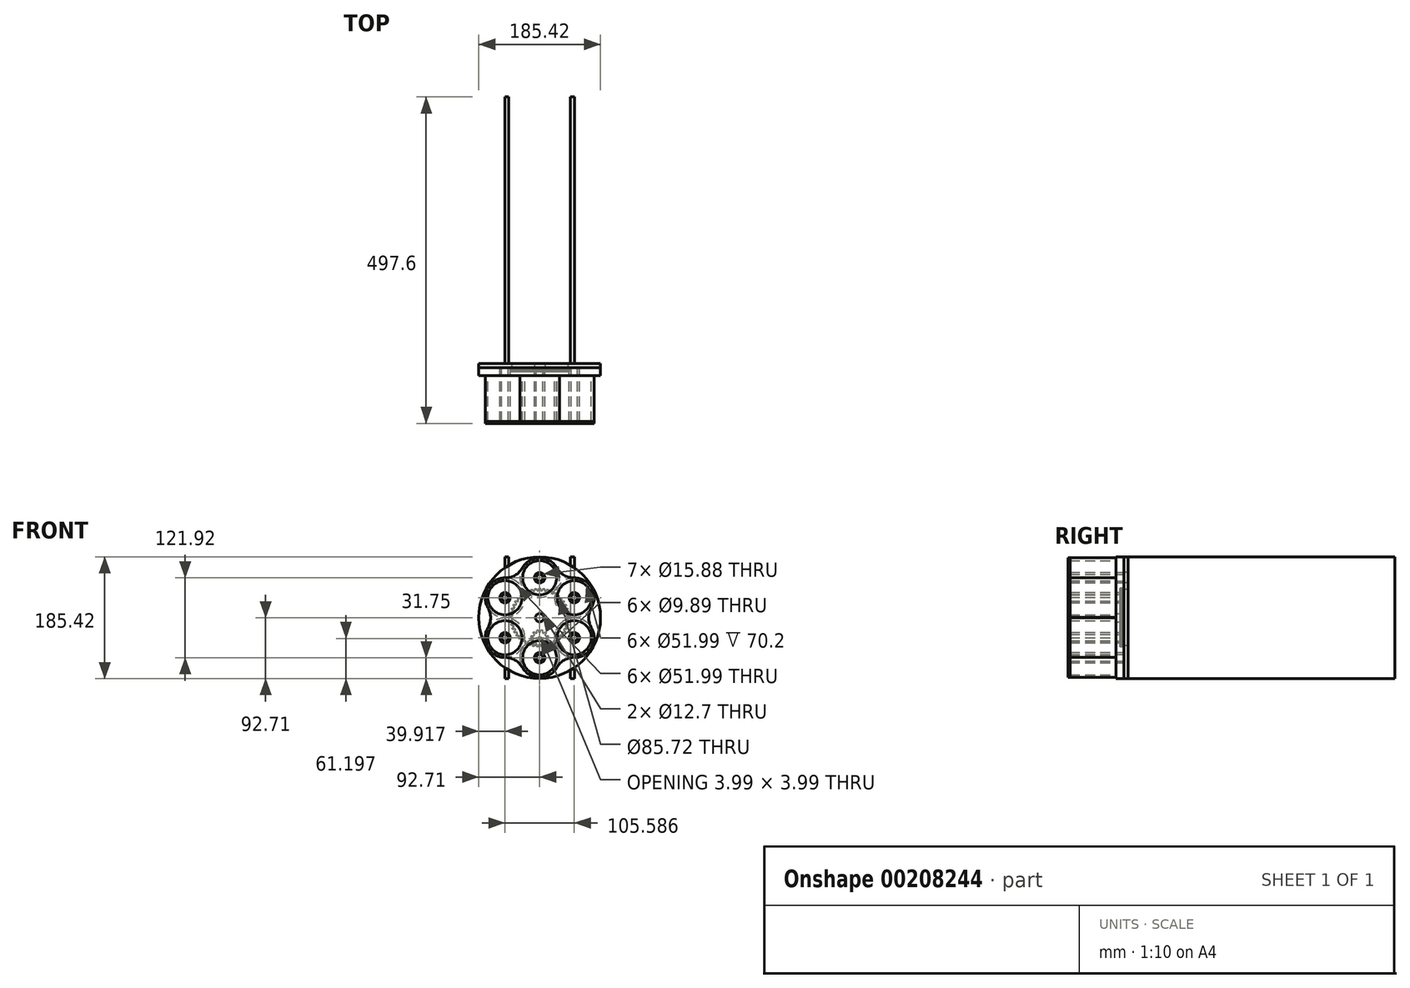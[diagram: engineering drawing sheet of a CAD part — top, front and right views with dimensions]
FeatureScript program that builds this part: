
annotation { "Feature Type Name" : "Feature", "Feature Type Description" : "" }
export const myFeature = defineFeature(function(context is Context, id is Id, definition is map)
    precondition{}
    {
        {
            var Q0;
            Q0=qCreatedBy(makeId("Front.planeOp"),FACE);
            var sketch = newSketch(context, id + "F0", { "sketchPlane" : qUnion([Q0])});
            skCircle(sketch, "E0", {"center": v(0, 0) * mm, "radius": 92.71 * mm});
            skCircle(sketch, "E1", {"center": v(0, 60.96) * mm, "radius": 26.67 * mm});
            skCircle(sketch, "E2", {"center": v(0, 60.96) * mm, "radius": 7.94 * mm});
            skCircle(sketch, "E3", {"center": v(0, 0) * mm, "radius": 60.96 * mm, "construction": true});
            skCircle(sketch, "E4.1.0", {"center": v(-52.8, 30.48) * mm, "radius": 26.67 * mm});
            skCircle(sketch, "E4.2.0", {"center": v(-52.8, -30.48) * mm, "radius": 26.67 * mm});
            skCircle(sketch, "E4.3.0", {"center": v(0, -60.96) * mm, "radius": 26.67 * mm});
            skCircle(sketch, "E4.4.0", {"center": v(52.8, -30.48) * mm, "radius": 26.67 * mm});
            skCircle(sketch, "E4.5.0", {"center": v(52.8, 30.48) * mm, "radius": 26.67 * mm});
            skCircle(sketch, "E5", {"center": v(0, 0) * mm, "radius": 6.35 * mm});
            skCircle(sketch, "E6.1.0", {"center": v(-52.8, 30.48) * mm, "radius": 7.94 * mm});
            skCircle(sketch, "E6.2.0", {"center": v(-52.8, -30.48) * mm, "radius": 7.94 * mm});
            skCircle(sketch, "E6.3.0", {"center": v(0, -60.96) * mm, "radius": 7.94 * mm});
            skCircle(sketch, "E6.4.0", {"center": v(52.8, -30.48) * mm, "radius": 7.94 * mm});
            skCircle(sketch, "E6.5.0", {"center": v(52.8, 30.48) * mm, "radius": 7.94 * mm});
            skSolve(sketch);
        }
        {
            var Q0;
            Q0=qCreatedBy(makeId("Front.planeOp"),FACE);
            var sketch = newSketch(context, id + "F1", { "sketchPlane" : qUnion([Q0])});
            skCircle(sketch, "E7.0", {"center": v(0, 0) * mm, "radius": 92.71 * mm});
            skCircle(sketch, "E8.0", {"center": v(0, 60.96) * mm, "radius": 7.94 * mm});
            skCircle(sketch, "E9.0", {"center": v(0, 0) * mm, "radius": 6.35 * mm});
            skCircle(sketch, "E10.0", {"center": v(52.8, 30.48) * mm, "radius": 7.94 * mm});
            skCircle(sketch, "E10.1", {"center": v(52.8, -30.48) * mm, "radius": 7.94 * mm});
            skCircle(sketch, "E10.2", {"center": v(0, -60.96) * mm, "radius": 7.94 * mm});
            skCircle(sketch, "E10.3", {"center": v(-52.8, -30.48) * mm, "radius": 7.94 * mm});
            skCircle(sketch, "E10.4", {"center": v(-52.8, 30.48) * mm, "radius": 7.94 * mm});
            skSolve(sketch);
        }
        {
            var Q0;
            Q0 = qSketchRegion(id + "F1", true);
            extrude(context, id + "F2", {"entities" : qUnion([Q0]), "depth" : 6 * mm});
        }
        {
            var Q0;
            Q0=qCreatedBy(makeId("Front.planeOp"),FACE);
            var sketch = newSketch(context, id + "F3", { "sketchPlane" : qUnion([Q0])});
            skLineSegment(sketch, "E11", {"start": v(0, 52.57) * mm, "end": v(-10.93, 51.42) * mm});
            skLineSegment(sketch, "E12", {"start": v(-10.93, 51.42) * mm, "end": v(-21.38, 48.03) * mm});
            skLineSegment(sketch, "E13", {"start": v(-21.38, 48.03) * mm, "end": v(-30.9, 42.53) * mm});
            skLineSegment(sketch, "E14", {"start": v(-30.9, 42.53) * mm, "end": v(-39.07, 35.18) * mm});
            skLineSegment(sketch, "E15", {"start": v(-39.07, 35.18) * mm, "end": v(-45.53, 26.29) * mm});
            skLineSegment(sketch, "E16", {"start": v(-45.53, 26.29) * mm, "end": v(-50, 16.25) * mm});
            skLineSegment(sketch, "E17", {"start": v(-50, 16.25) * mm, "end": v(-52.28, 5.5) * mm});
            skLineSegment(sketch, "E18", {"start": v(-52.28, 5.5) * mm, "end": v(-52.28, -5.5) * mm});
            skLineSegment(sketch, "E19", {"start": v(-52.28, -5.5) * mm, "end": v(-50, -16.25) * mm});
            skLineSegment(sketch, "E20", {"start": v(-50, -16.25) * mm, "end": v(-45.53, -26.29) * mm});
            skLineSegment(sketch, "E21", {"start": v(-45.53, -26.29) * mm, "end": v(-39.07, -35.18) * mm});
            skLineSegment(sketch, "E22", {"start": v(-39.07, -35.18) * mm, "end": v(-30.9, -42.53) * mm});
            skLineSegment(sketch, "E23", {"start": v(-30.9, -42.53) * mm, "end": v(-21.38, -48.03) * mm});
            skLineSegment(sketch, "E24", {"start": v(-21.38, -48.03) * mm, "end": v(-10.93, -51.42) * mm});
            skLineSegment(sketch, "E25", {"start": v(-10.93, -51.42) * mm, "end": v(0, -52.57) * mm});
            skLineSegment(sketch, "E26", {"start": v(0, -52.57) * mm, "end": v(10.93, -51.42) * mm});
            skLineSegment(sketch, "E27", {"start": v(10.93, -51.42) * mm, "end": v(21.38, -48.03) * mm});
            skLineSegment(sketch, "E28", {"start": v(21.38, -48.03) * mm, "end": v(30.9, -42.53) * mm});
            skLineSegment(sketch, "E29", {"start": v(30.9, -42.53) * mm, "end": v(39.07, -35.18) * mm});
            skLineSegment(sketch, "E30", {"start": v(39.07, -35.18) * mm, "end": v(45.53, -26.29) * mm});
            skLineSegment(sketch, "E31", {"start": v(45.53, -26.29) * mm, "end": v(50, -16.25) * mm});
            skLineSegment(sketch, "E32", {"start": v(50, -16.25) * mm, "end": v(52.28, -5.5) * mm});
            skLineSegment(sketch, "E33", {"start": v(52.28, -5.5) * mm, "end": v(52.28, 5.5) * mm});
            skLineSegment(sketch, "E34", {"start": v(52.28, 5.5) * mm, "end": v(50, 16.25) * mm});
            skLineSegment(sketch, "E35", {"start": v(50, 16.25) * mm, "end": v(45.53, 26.29) * mm});
            skLineSegment(sketch, "E36", {"start": v(45.53, 26.29) * mm, "end": v(39.07, 35.18) * mm});
            skLineSegment(sketch, "E37", {"start": v(39.07, 35.18) * mm, "end": v(30.9, 42.53) * mm});
            skLineSegment(sketch, "E38", {"start": v(30.9, 42.53) * mm, "end": v(21.38, 48.03) * mm});
            skLineSegment(sketch, "E39", {"start": v(21.38, 48.03) * mm, "end": v(10.93, 51.42) * mm});
            skLineSegment(sketch, "E40", {"start": v(10.93, 51.42) * mm, "end": v(0, 52.57) * mm});
            skLineSegment(sketch, "E41", {"start": v(-3, -44.75) * mm, "end": v(-3.13, -44.73) * mm});
            skLineSegment(sketch, "E42", {"start": v(-3.13, -44.73) * mm, "end": v(-3.25, -44.73) * mm});
            skLineSegment(sketch, "E43", {"start": v(-3.25, -44.73) * mm, "end": v(-3.7, -44.68) * mm});
            skLineSegment(sketch, "E44", {"start": v(-3.7, -44.68) * mm, "end": v(-3.92, -44.58) * mm});
            skLineSegment(sketch, "E45", {"start": v(-3.92, -44.58) * mm, "end": v(-4.13, -44.16) * mm});
            skLineSegment(sketch, "E46", {"start": v(-4.13, -44.16) * mm, "end": v(-4.38, -43.31) * mm});
            skLineSegment(sketch, "E47", {"start": v(-4.38, -43.31) * mm, "end": v(-4.43, -43.13) * mm});
            skLineSegment(sketch, "E48", {"start": v(-4.43, -43.13) * mm, "end": v(-4.55, -42.6) * mm});
            skLineSegment(sketch, "E49", {"start": v(-4.55, -42.6) * mm, "end": v(-4.56, -42.54) * mm});
            skLineSegment(sketch, "E50", {"start": v(-4.56, -42.54) * mm, "end": v(-4.64, -42.15) * mm});
            skLineSegment(sketch, "E51", {"start": v(-4.64, -42.15) * mm, "end": v(-4.64, -42.07) * mm});
            skLineSegment(sketch, "E52", {"start": v(-4.64, -42.07) * mm, "end": v(-4.69, -41.85) * mm});
            skLineSegment(sketch, "E53", {"start": v(-4.69, -41.85) * mm, "end": v(-4.7, -41.78) * mm});
            skLineSegment(sketch, "E54", {"start": v(-4.7, -41.78) * mm, "end": v(-4.7, -41.66) * mm});
            skLineSegment(sketch, "E55", {"start": v(-4.7, -41.66) * mm, "end": v(-4.8, -41.02) * mm});
            skLineSegment(sketch, "E56", {"start": v(-4.8, -41.02) * mm, "end": v(-4.84, -40.92) * mm});
            skLineSegment(sketch, "E57", {"start": v(-4.84, -40.92) * mm, "end": v(-4.86, -40.88) * mm});
            skLineSegment(sketch, "E58", {"start": v(-4.86, -40.88) * mm, "end": v(-4.9, -40.83) * mm});
            skLineSegment(sketch, "E59", {"start": v(-4.9, -40.83) * mm, "end": v(-6.54, -40.6) * mm});
            skLineSegment(sketch, "E60", {"start": v(-6.54, -40.6) * mm, "end": v(-6.6, -40.63) * mm});
            skLineSegment(sketch, "E61", {"start": v(-6.6, -40.63) * mm, "end": v(-6.63, -40.67) * mm});
            skLineSegment(sketch, "E62", {"start": v(-6.63, -40.67) * mm, "end": v(-6.69, -40.75) * mm});
            skLineSegment(sketch, "E63", {"start": v(-6.69, -40.75) * mm, "end": v(-6.97, -41.34) * mm});
            skLineSegment(sketch, "E64", {"start": v(-6.97, -41.34) * mm, "end": v(-7, -41.45) * mm});
            skLineSegment(sketch, "E65", {"start": v(-7, -41.45) * mm, "end": v(-7.03, -41.52) * mm});
            skLineSegment(sketch, "E66", {"start": v(-7.03, -41.52) * mm, "end": v(-7.14, -41.72) * mm});
            skLineSegment(sketch, "E67", {"start": v(-7.14, -41.72) * mm, "end": v(-7.16, -41.8) * mm});
            skLineSegment(sketch, "E68", {"start": v(-7.16, -41.8) * mm, "end": v(-7.34, -42.15) * mm});
            skLineSegment(sketch, "E69", {"start": v(-7.34, -42.15) * mm, "end": v(-7.37, -42.2) * mm});
            skLineSegment(sketch, "E70", {"start": v(-7.37, -42.2) * mm, "end": v(-7.63, -42.68) * mm});
            skLineSegment(sketch, "E71", {"start": v(-7.63, -42.68) * mm, "end": v(-7.73, -42.84) * mm});
            skLineSegment(sketch, "E72", {"start": v(-7.73, -42.84) * mm, "end": v(-8.2, -43.59) * mm});
            skLineSegment(sketch, "E73", {"start": v(-8.2, -43.59) * mm, "end": v(-8.51, -43.93) * mm});
            skLineSegment(sketch, "E74", {"start": v(-8.51, -43.93) * mm, "end": v(-8.76, -43.97) * mm});
            skLineSegment(sketch, "E75", {"start": v(-8.76, -43.97) * mm, "end": v(-9.2, -43.9) * mm});
            skLineSegment(sketch, "E76", {"start": v(-9.2, -43.9) * mm, "end": v(-9.32, -43.86) * mm});
            skLineSegment(sketch, "E77", {"start": v(-9.32, -43.86) * mm, "end": v(-9.44, -43.84) * mm});
            skLineSegment(sketch, "E78", {"start": v(-9.44, -43.84) * mm, "end": v(-9.88, -43.73) * mm});
            skLineSegment(sketch, "E79", {"start": v(-9.88, -43.73) * mm, "end": v(-10.1, -43.6) * mm});
            skLineSegment(sketch, "E80", {"start": v(-10.1, -43.6) * mm, "end": v(-10.24, -43.15) * mm});
            skLineSegment(sketch, "E81", {"start": v(-10.24, -43.15) * mm, "end": v(-10.36, -42.28) * mm});
            skLineSegment(sketch, "E82", {"start": v(-10.36, -42.28) * mm, "end": v(-10.39, -42.1) * mm});
            skLineSegment(sketch, "E83", {"start": v(-10.39, -42.1) * mm, "end": v(-10.44, -41.55) * mm});
            skLineSegment(sketch, "E84", {"start": v(-10.44, -41.55) * mm, "end": v(-10.44, -41.5) * mm});
            skLineSegment(sketch, "E85", {"start": v(-10.44, -41.5) * mm, "end": v(-10.46, -41.1) * mm});
            skLineSegment(sketch, "E86", {"start": v(-10.46, -41.1) * mm, "end": v(-10.45, -41.02) * mm});
            skLineSegment(sketch, "E87", {"start": v(-10.45, -41.02) * mm, "end": v(-10.47, -40.8) * mm});
            skLineSegment(sketch, "E88", {"start": v(-10.47, -40.8) * mm, "end": v(-10.47, -40.72) * mm});
            skLineSegment(sketch, "E89", {"start": v(-10.47, -40.72) * mm, "end": v(-10.45, -40.6) * mm});
            skLineSegment(sketch, "E90", {"start": v(-10.45, -40.6) * mm, "end": v(-10.47, -39.95) * mm});
            skLineSegment(sketch, "E91", {"start": v(-10.47, -39.95) * mm, "end": v(-10.48, -39.85) * mm});
            skLineSegment(sketch, "E92", {"start": v(-10.48, -39.85) * mm, "end": v(-10.5, -39.8) * mm});
            skLineSegment(sketch, "E93", {"start": v(-10.5, -39.8) * mm, "end": v(-10.54, -39.75) * mm});
            skLineSegment(sketch, "E94", {"start": v(-10.54, -39.75) * mm, "end": v(-12.13, -39.3) * mm});
            skLineSegment(sketch, "E95", {"start": v(-12.13, -39.3) * mm, "end": v(-12.18, -39.32) * mm});
            skLineSegment(sketch, "E96", {"start": v(-12.18, -39.32) * mm, "end": v(-12.23, -39.35) * mm});
            skLineSegment(sketch, "E97", {"start": v(-12.23, -39.35) * mm, "end": v(-12.3, -39.43) * mm});
            skLineSegment(sketch, "E98", {"start": v(-12.3, -39.43) * mm, "end": v(-12.65, -39.97) * mm});
            skLineSegment(sketch, "E99", {"start": v(-12.65, -39.97) * mm, "end": v(-12.7, -40.08) * mm});
            skLineSegment(sketch, "E100", {"start": v(-12.7, -40.08) * mm, "end": v(-12.74, -40.14) * mm});
            skLineSegment(sketch, "E101", {"start": v(-12.74, -40.14) * mm, "end": v(-12.87, -40.32) * mm});
            skLineSegment(sketch, "E102", {"start": v(-12.87, -40.32) * mm, "end": v(-12.9, -40.39) * mm});
            skLineSegment(sketch, "E103", {"start": v(-12.9, -40.39) * mm, "end": v(-13.14, -40.72) * mm});
            skLineSegment(sketch, "E104", {"start": v(-13.14, -40.72) * mm, "end": v(-13.17, -40.77) * mm});
            skLineSegment(sketch, "E105", {"start": v(-13.17, -40.77) * mm, "end": v(-13.5, -41.2) * mm});
            skLineSegment(sketch, "E106", {"start": v(-13.5, -41.2) * mm, "end": v(-13.62, -41.35) * mm});
            skLineSegment(sketch, "E107", {"start": v(-13.62, -41.35) * mm, "end": v(-14.19, -42.02) * mm});
            skLineSegment(sketch, "E108", {"start": v(-14.19, -42.02) * mm, "end": v(-14.55, -42.32) * mm});
            skLineSegment(sketch, "E109", {"start": v(-14.55, -42.32) * mm, "end": v(-14.8, -42.32) * mm});
            skLineSegment(sketch, "E110", {"start": v(-14.8, -42.32) * mm, "end": v(-15.22, -42.18) * mm});
            skLineSegment(sketch, "E111", {"start": v(-15.22, -42.18) * mm, "end": v(-15.34, -42.14) * mm});
            skLineSegment(sketch, "E112", {"start": v(-15.34, -42.14) * mm, "end": v(-15.45, -42.1) * mm});
            skLineSegment(sketch, "E113", {"start": v(-15.45, -42.1) * mm, "end": v(-15.87, -41.93) * mm});
            skLineSegment(sketch, "E114", {"start": v(-15.87, -41.93) * mm, "end": v(-16.06, -41.77) * mm});
            skLineSegment(sketch, "E115", {"start": v(-16.06, -41.77) * mm, "end": v(-16.14, -41.3) * mm});
            skLineSegment(sketch, "E116", {"start": v(-16.14, -41.3) * mm, "end": v(-16.15, -40.43) * mm});
            skLineSegment(sketch, "E117", {"start": v(-16.15, -40.43) * mm, "end": v(-16.15, -40.24) * mm});
            skLineSegment(sketch, "E118", {"start": v(-16.15, -40.24) * mm, "end": v(-16.12, -39.7) * mm});
            skLineSegment(sketch, "E119", {"start": v(-16.12, -39.7) * mm, "end": v(-16.11, -39.64) * mm});
            skLineSegment(sketch, "E120", {"start": v(-16.11, -39.64) * mm, "end": v(-16.08, -39.23) * mm});
            skLineSegment(sketch, "E121", {"start": v(-16.08, -39.23) * mm, "end": v(-16.06, -39.16) * mm});
            skLineSegment(sketch, "E122", {"start": v(-16.06, -39.16) * mm, "end": v(-16.04, -38.94) * mm});
            skLineSegment(sketch, "E123", {"start": v(-16.04, -38.94) * mm, "end": v(-16.03, -38.86) * mm});
            skLineSegment(sketch, "E124", {"start": v(-16.03, -38.86) * mm, "end": v(-16, -38.75) * mm});
            skLineSegment(sketch, "E125", {"start": v(-16, -38.75) * mm, "end": v(-15.93, -38.1) * mm});
            skLineSegment(sketch, "E126", {"start": v(-15.93, -38.1) * mm, "end": v(-15.93, -38) * mm});
            skLineSegment(sketch, "E127", {"start": v(-15.93, -38) * mm, "end": v(-15.94, -37.95) * mm});
            skLineSegment(sketch, "E128", {"start": v(-15.94, -37.95) * mm, "end": v(-15.97, -37.9) * mm});
            skLineSegment(sketch, "E129", {"start": v(-15.97, -37.9) * mm, "end": v(-17.48, -37.22) * mm});
            skLineSegment(sketch, "E130", {"start": v(-17.48, -37.22) * mm, "end": v(-17.54, -37.24) * mm});
            skLineSegment(sketch, "E131", {"start": v(-17.54, -37.24) * mm, "end": v(-17.58, -37.26) * mm});
            skLineSegment(sketch, "E132", {"start": v(-17.58, -37.26) * mm, "end": v(-17.66, -37.33) * mm});
            skLineSegment(sketch, "E133", {"start": v(-17.66, -37.33) * mm, "end": v(-18.1, -37.81) * mm});
            skLineSegment(sketch, "E134", {"start": v(-18.1, -37.81) * mm, "end": v(-18.15, -37.92) * mm});
            skLineSegment(sketch, "E135", {"start": v(-18.15, -37.92) * mm, "end": v(-18.2, -37.98) * mm});
            skLineSegment(sketch, "E136", {"start": v(-18.2, -37.98) * mm, "end": v(-18.36, -38.14) * mm});
            skLineSegment(sketch, "E137", {"start": v(-18.36, -38.14) * mm, "end": v(-18.4, -38.2) * mm});
            skLineSegment(sketch, "E138", {"start": v(-18.4, -38.2) * mm, "end": v(-18.68, -38.5) * mm});
            skLineSegment(sketch, "E139", {"start": v(-18.68, -38.5) * mm, "end": v(-18.71, -38.54) * mm});
            skLineSegment(sketch, "E140", {"start": v(-18.71, -38.54) * mm, "end": v(-19.1, -38.93) * mm});
            skLineSegment(sketch, "E141", {"start": v(-19.1, -38.93) * mm, "end": v(-19.24, -39.05) * mm});
            skLineSegment(sketch, "E142", {"start": v(-19.24, -39.05) * mm, "end": v(-19.9, -39.64) * mm});
            skLineSegment(sketch, "E143", {"start": v(-19.9, -39.64) * mm, "end": v(-20.3, -39.88) * mm});
            skLineSegment(sketch, "E144", {"start": v(-20.3, -39.88) * mm, "end": v(-20.54, -39.85) * mm});
            skLineSegment(sketch, "E145", {"start": v(-20.54, -39.85) * mm, "end": v(-20.95, -39.65) * mm});
            skLineSegment(sketch, "E146", {"start": v(-20.95, -39.65) * mm, "end": v(-21.05, -39.6) * mm});
            skLineSegment(sketch, "E147", {"start": v(-21.05, -39.6) * mm, "end": v(-21.16, -39.54) * mm});
            skLineSegment(sketch, "E148", {"start": v(-21.16, -39.54) * mm, "end": v(-21.55, -39.31) * mm});
            skLineSegment(sketch, "E149", {"start": v(-21.55, -39.31) * mm, "end": v(-21.72, -39.13) * mm});
            skLineSegment(sketch, "E150", {"start": v(-21.72, -39.13) * mm, "end": v(-21.73, -38.66) * mm});
            skLineSegment(sketch, "E151", {"start": v(-21.73, -38.66) * mm, "end": v(-21.62, -37.79) * mm});
            skLineSegment(sketch, "E152", {"start": v(-21.62, -37.79) * mm, "end": v(-21.59, -37.6) * mm});
            skLineSegment(sketch, "E153", {"start": v(-21.59, -37.6) * mm, "end": v(-21.48, -37.06) * mm});
            skLineSegment(sketch, "E154", {"start": v(-21.48, -37.06) * mm, "end": v(-21.47, -37) * mm});
            skLineSegment(sketch, "E155", {"start": v(-21.47, -37) * mm, "end": v(-21.38, -36.62) * mm});
            skLineSegment(sketch, "E156", {"start": v(-21.38, -36.62) * mm, "end": v(-21.35, -36.55) * mm});
            skLineSegment(sketch, "E157", {"start": v(-21.35, -36.55) * mm, "end": v(-21.3, -36.33) * mm});
            skLineSegment(sketch, "E158", {"start": v(-21.3, -36.33) * mm, "end": v(-21.28, -36.25) * mm});
            skLineSegment(sketch, "E159", {"start": v(-21.28, -36.25) * mm, "end": v(-21.23, -36.15) * mm});
            skLineSegment(sketch, "E160", {"start": v(-21.23, -36.15) * mm, "end": v(-21.07, -35.52) * mm});
            skLineSegment(sketch, "E161", {"start": v(-21.07, -35.52) * mm, "end": v(-21.06, -35.41) * mm});
            skLineSegment(sketch, "E162", {"start": v(-21.06, -35.41) * mm, "end": v(-21.07, -35.36) * mm});
            skLineSegment(sketch, "E163", {"start": v(-21.07, -35.36) * mm, "end": v(-21.08, -35.3) * mm});
            skLineSegment(sketch, "E164", {"start": v(-21.08, -35.3) * mm, "end": v(-22.49, -34.43) * mm});
            skLineSegment(sketch, "E165", {"start": v(-22.49, -34.43) * mm, "end": v(-22.55, -34.44) * mm});
            skLineSegment(sketch, "E166", {"start": v(-22.55, -34.44) * mm, "end": v(-22.6, -34.45) * mm});
            skLineSegment(sketch, "E167", {"start": v(-22.6, -34.45) * mm, "end": v(-22.68, -34.51) * mm});
            skLineSegment(sketch, "E168", {"start": v(-22.68, -34.51) * mm, "end": v(-23.18, -34.93) * mm});
            skLineSegment(sketch, "E169", {"start": v(-23.18, -34.93) * mm, "end": v(-23.26, -35.02) * mm});
            skLineSegment(sketch, "E170", {"start": v(-23.26, -35.02) * mm, "end": v(-23.31, -35.07) * mm});
            skLineSegment(sketch, "E171", {"start": v(-23.31, -35.07) * mm, "end": v(-23.49, -35.21) * mm});
            skLineSegment(sketch, "E172", {"start": v(-23.49, -35.21) * mm, "end": v(-23.54, -35.27) * mm});
            skLineSegment(sketch, "E173", {"start": v(-23.54, -35.27) * mm, "end": v(-23.85, -35.52) * mm});
            skLineSegment(sketch, "E174", {"start": v(-23.85, -35.52) * mm, "end": v(-23.9, -35.56) * mm});
            skLineSegment(sketch, "E175", {"start": v(-23.9, -35.56) * mm, "end": v(-24.33, -35.89) * mm});
            skLineSegment(sketch, "E176", {"start": v(-24.33, -35.89) * mm, "end": v(-24.49, -36) * mm});
            skLineSegment(sketch, "E177", {"start": v(-24.49, -36) * mm, "end": v(-25.22, -36.48) * mm});
            skLineSegment(sketch, "E178", {"start": v(-25.22, -36.48) * mm, "end": v(-25.65, -36.67) * mm});
            skLineSegment(sketch, "E179", {"start": v(-25.65, -36.67) * mm, "end": v(-25.89, -36.6) * mm});
            skLineSegment(sketch, "E180", {"start": v(-25.89, -36.6) * mm, "end": v(-26.26, -36.35) * mm});
            skLineSegment(sketch, "E181", {"start": v(-26.26, -36.35) * mm, "end": v(-26.36, -36.28) * mm});
            skLineSegment(sketch, "E182", {"start": v(-26.36, -36.28) * mm, "end": v(-26.46, -36.2) * mm});
            skLineSegment(sketch, "E183", {"start": v(-26.46, -36.2) * mm, "end": v(-26.81, -35.93) * mm});
            skLineSegment(sketch, "E184", {"start": v(-26.81, -35.93) * mm, "end": v(-26.95, -35.72) * mm});
            skLineSegment(sketch, "E185", {"start": v(-26.95, -35.72) * mm, "end": v(-26.9, -35.26) * mm});
            skLineSegment(sketch, "E186", {"start": v(-26.9, -35.26) * mm, "end": v(-26.67, -34.41) * mm});
            skLineSegment(sketch, "E187", {"start": v(-26.67, -34.41) * mm, "end": v(-26.61, -34.23) * mm});
            skLineSegment(sketch, "E188", {"start": v(-26.61, -34.23) * mm, "end": v(-26.43, -33.71) * mm});
            skLineSegment(sketch, "E189", {"start": v(-26.43, -33.71) * mm, "end": v(-26.41, -33.66) * mm});
            skLineSegment(sketch, "E190", {"start": v(-26.41, -33.66) * mm, "end": v(-26.27, -33.28) * mm});
            skLineSegment(sketch, "E191", {"start": v(-26.27, -33.28) * mm, "end": v(-26.23, -33.22) * mm});
            skLineSegment(sketch, "E192", {"start": v(-26.23, -33.22) * mm, "end": v(-26.15, -33) * mm});
            skLineSegment(sketch, "E193", {"start": v(-26.15, -33) * mm, "end": v(-26.12, -32.94) * mm});
            skLineSegment(sketch, "E194", {"start": v(-26.12, -32.94) * mm, "end": v(-26.06, -32.84) * mm});
            skLineSegment(sketch, "E195", {"start": v(-26.06, -32.84) * mm, "end": v(-25.81, -32.24) * mm});
            skLineSegment(sketch, "E196", {"start": v(-25.81, -32.24) * mm, "end": v(-25.79, -32.14) * mm});
            skLineSegment(sketch, "E197", {"start": v(-25.79, -32.14) * mm, "end": v(-25.78, -32.09) * mm});
            skLineSegment(sketch, "E198", {"start": v(-25.78, -32.09) * mm, "end": v(-25.8, -32.03) * mm});
            skLineSegment(sketch, "E199", {"start": v(-25.8, -32.03) * mm, "end": v(-27.06, -30.96) * mm});
            skLineSegment(sketch, "E200", {"start": v(-27.06, -30.96) * mm, "end": v(-27.12, -30.97) * mm});
            skLineSegment(sketch, "E201", {"start": v(-27.12, -30.97) * mm, "end": v(-27.17, -30.97) * mm});
            skLineSegment(sketch, "E202", {"start": v(-27.17, -30.97) * mm, "end": v(-27.27, -31.02) * mm});
            skLineSegment(sketch, "E203", {"start": v(-27.27, -31.02) * mm, "end": v(-27.82, -31.36) * mm});
            skLineSegment(sketch, "E204", {"start": v(-27.82, -31.36) * mm, "end": v(-27.9, -31.45) * mm});
            skLineSegment(sketch, "E205", {"start": v(-27.9, -31.45) * mm, "end": v(-27.96, -31.49) * mm});
            skLineSegment(sketch, "E206", {"start": v(-27.96, -31.49) * mm, "end": v(-28.16, -31.6) * mm});
            skLineSegment(sketch, "E207", {"start": v(-28.16, -31.6) * mm, "end": v(-28.22, -31.65) * mm});
            skLineSegment(sketch, "E208", {"start": v(-28.22, -31.65) * mm, "end": v(-28.56, -31.86) * mm});
            skLineSegment(sketch, "E209", {"start": v(-28.56, -31.86) * mm, "end": v(-28.61, -31.89) * mm});
            skLineSegment(sketch, "E210", {"start": v(-28.61, -31.89) * mm, "end": v(-29.1, -32.15) * mm});
            skLineSegment(sketch, "E211", {"start": v(-29.1, -32.15) * mm, "end": v(-29.26, -32.24) * mm});
            skLineSegment(sketch, "E212", {"start": v(-29.26, -32.24) * mm, "end": v(-30.05, -32.62) * mm});
            skLineSegment(sketch, "E213", {"start": v(-30.05, -32.62) * mm, "end": v(-30.5, -32.74) * mm});
            skLineSegment(sketch, "E214", {"start": v(-30.5, -32.74) * mm, "end": v(-30.73, -32.64) * mm});
            skLineSegment(sketch, "E215", {"start": v(-30.73, -32.64) * mm, "end": v(-31.06, -32.34) * mm});
            skLineSegment(sketch, "E216", {"start": v(-31.06, -32.34) * mm, "end": v(-31.15, -32.26) * mm});
            skLineSegment(sketch, "E217", {"start": v(-31.15, -32.26) * mm, "end": v(-31.24, -32.17) * mm});
            skLineSegment(sketch, "E218", {"start": v(-31.24, -32.17) * mm, "end": v(-31.55, -31.85) * mm});
            skLineSegment(sketch, "E219", {"start": v(-31.55, -31.85) * mm, "end": v(-31.66, -31.62) * mm});
            skLineSegment(sketch, "E220", {"start": v(-31.66, -31.62) * mm, "end": v(-31.55, -31.17) * mm});
            skLineSegment(sketch, "E221", {"start": v(-31.55, -31.17) * mm, "end": v(-31.2, -30.37) * mm});
            skLineSegment(sketch, "E222", {"start": v(-31.2, -30.37) * mm, "end": v(-31.12, -30.2) * mm});
            skLineSegment(sketch, "E223", {"start": v(-31.12, -30.2) * mm, "end": v(-30.87, -29.7) * mm});
            skLineSegment(sketch, "E224", {"start": v(-30.87, -29.7) * mm, "end": v(-30.84, -29.66) * mm});
            skLineSegment(sketch, "E225", {"start": v(-30.84, -29.66) * mm, "end": v(-30.64, -29.3) * mm});
            skLineSegment(sketch, "E226", {"start": v(-30.64, -29.3) * mm, "end": v(-30.6, -29.25) * mm});
            skLineSegment(sketch, "E227", {"start": v(-30.6, -29.25) * mm, "end": v(-30.5, -29.05) * mm});
            skLineSegment(sketch, "E228", {"start": v(-30.5, -29.05) * mm, "end": v(-30.45, -28.98) * mm});
            skLineSegment(sketch, "E229", {"start": v(-30.45, -28.98) * mm, "end": v(-30.37, -28.9) * mm});
            skLineSegment(sketch, "E230", {"start": v(-30.37, -28.9) * mm, "end": v(-30.05, -28.33) * mm});
            skLineSegment(sketch, "E231", {"start": v(-30.05, -28.33) * mm, "end": v(-30, -28.24) * mm});
            skLineSegment(sketch, "E232", {"start": v(-30, -28.24) * mm, "end": v(-30, -28.19) * mm});
            skLineSegment(sketch, "E233", {"start": v(-30, -28.19) * mm, "end": v(-30, -28.12) * mm});
            skLineSegment(sketch, "E234", {"start": v(-30, -28.12) * mm, "end": v(-31.1, -26.9) * mm});
            skLineSegment(sketch, "E235", {"start": v(-31.1, -26.9) * mm, "end": v(-31.17, -26.89) * mm});
            skLineSegment(sketch, "E236", {"start": v(-31.17, -26.89) * mm, "end": v(-31.22, -26.9) * mm});
            skLineSegment(sketch, "E237", {"start": v(-31.22, -26.9) * mm, "end": v(-31.32, -26.92) * mm});
            skLineSegment(sketch, "E238", {"start": v(-31.32, -26.92) * mm, "end": v(-31.9, -27.19) * mm});
            skLineSegment(sketch, "E239", {"start": v(-31.9, -27.19) * mm, "end": v(-32, -27.26) * mm});
            skLineSegment(sketch, "E240", {"start": v(-32, -27.26) * mm, "end": v(-32.07, -27.29) * mm});
            skLineSegment(sketch, "E241", {"start": v(-32.07, -27.29) * mm, "end": v(-32.28, -27.37) * mm});
            skLineSegment(sketch, "E242", {"start": v(-32.28, -27.37) * mm, "end": v(-32.35, -27.41) * mm});
            skLineSegment(sketch, "E243", {"start": v(-32.35, -27.41) * mm, "end": v(-32.72, -27.57) * mm});
            skLineSegment(sketch, "E244", {"start": v(-32.72, -27.57) * mm, "end": v(-32.77, -27.6) * mm});
            skLineSegment(sketch, "E245", {"start": v(-32.77, -27.6) * mm, "end": v(-33.28, -27.8) * mm});
            skLineSegment(sketch, "E246", {"start": v(-33.28, -27.8) * mm, "end": v(-33.46, -27.85) * mm});
            skLineSegment(sketch, "E247", {"start": v(-33.46, -27.85) * mm, "end": v(-34.3, -28.12) * mm});
            skLineSegment(sketch, "E248", {"start": v(-34.3, -28.12) * mm, "end": v(-34.76, -28.18) * mm});
            skLineSegment(sketch, "E249", {"start": v(-34.76, -28.18) * mm, "end": v(-34.98, -28.05) * mm});
            skLineSegment(sketch, "E250", {"start": v(-34.98, -28.05) * mm, "end": v(-35.26, -27.7) * mm});
            skLineSegment(sketch, "E251", {"start": v(-35.26, -27.7) * mm, "end": v(-35.34, -27.6) * mm});
            skLineSegment(sketch, "E252", {"start": v(-35.34, -27.6) * mm, "end": v(-35.41, -27.51) * mm});
            skLineSegment(sketch, "E253", {"start": v(-35.41, -27.51) * mm, "end": v(-35.68, -27.15) * mm});
            skLineSegment(sketch, "E254", {"start": v(-35.68, -27.15) * mm, "end": v(-35.75, -26.91) * mm});
            skLineSegment(sketch, "E255", {"start": v(-35.75, -26.91) * mm, "end": v(-35.58, -26.48) * mm});
            skLineSegment(sketch, "E256", {"start": v(-35.58, -26.48) * mm, "end": v(-35.12, -25.73) * mm});
            skLineSegment(sketch, "E257", {"start": v(-35.12, -25.73) * mm, "end": v(-35.02, -25.57) * mm});
            skLineSegment(sketch, "E258", {"start": v(-35.02, -25.57) * mm, "end": v(-34.7, -25.12) * mm});
            skLineSegment(sketch, "E259", {"start": v(-34.7, -25.12) * mm, "end": v(-34.67, -25.08) * mm});
            skLineSegment(sketch, "E260", {"start": v(-34.67, -25.08) * mm, "end": v(-34.42, -24.75) * mm});
            skLineSegment(sketch, "E261", {"start": v(-34.42, -24.75) * mm, "end": v(-34.37, -24.7) * mm});
            skLineSegment(sketch, "E262", {"start": v(-34.37, -24.7) * mm, "end": v(-34.24, -24.52) * mm});
            skLineSegment(sketch, "E263", {"start": v(-34.24, -24.52) * mm, "end": v(-34.2, -24.46) * mm});
            skLineSegment(sketch, "E264", {"start": v(-34.2, -24.46) * mm, "end": v(-34.1, -24.39) * mm});
            skLineSegment(sketch, "E265", {"start": v(-34.1, -24.39) * mm, "end": v(-33.7, -23.87) * mm});
            skLineSegment(sketch, "E266", {"start": v(-33.7, -23.87) * mm, "end": v(-33.64, -23.79) * mm});
            skLineSegment(sketch, "E267", {"start": v(-33.64, -23.79) * mm, "end": v(-33.63, -23.74) * mm});
            skLineSegment(sketch, "E268", {"start": v(-33.63, -23.74) * mm, "end": v(-33.62, -23.68) * mm});
            skLineSegment(sketch, "E269", {"start": v(-33.62, -23.68) * mm, "end": v(-34.55, -22.3) * mm});
            skLineSegment(sketch, "E270", {"start": v(-34.55, -22.3) * mm, "end": v(-34.6, -22.29) * mm});
            skLineSegment(sketch, "E271", {"start": v(-34.6, -22.29) * mm, "end": v(-34.66, -22.28) * mm});
            skLineSegment(sketch, "E272", {"start": v(-34.66, -22.28) * mm, "end": v(-34.76, -22.3) * mm});
            skLineSegment(sketch, "E273", {"start": v(-34.76, -22.3) * mm, "end": v(-35.38, -22.48) * mm});
            skLineSegment(sketch, "E274", {"start": v(-35.38, -22.48) * mm, "end": v(-35.5, -22.54) * mm});
            skLineSegment(sketch, "E275", {"start": v(-35.5, -22.54) * mm, "end": v(-35.56, -22.56) * mm});
            skLineSegment(sketch, "E276", {"start": v(-35.56, -22.56) * mm, "end": v(-35.78, -22.61) * mm});
            skLineSegment(sketch, "E277", {"start": v(-35.78, -22.61) * mm, "end": v(-35.85, -22.65) * mm});
            skLineSegment(sketch, "E278", {"start": v(-35.85, -22.65) * mm, "end": v(-36.24, -22.75) * mm});
            skLineSegment(sketch, "E279", {"start": v(-36.24, -22.75) * mm, "end": v(-36.3, -22.77) * mm});
            skLineSegment(sketch, "E280", {"start": v(-36.3, -22.77) * mm, "end": v(-36.83, -22.89) * mm});
            skLineSegment(sketch, "E281", {"start": v(-36.83, -22.89) * mm, "end": v(-37.01, -22.92) * mm});
            skLineSegment(sketch, "E282", {"start": v(-37.01, -22.92) * mm, "end": v(-37.88, -23.07) * mm});
            skLineSegment(sketch, "E283", {"start": v(-37.88, -23.07) * mm, "end": v(-38.34, -23.07) * mm});
            skLineSegment(sketch, "E284", {"start": v(-38.34, -23.07) * mm, "end": v(-38.54, -22.9) * mm});
            skLineSegment(sketch, "E285", {"start": v(-38.54, -22.9) * mm, "end": v(-38.78, -22.53) * mm});
            skLineSegment(sketch, "E286", {"start": v(-38.78, -22.53) * mm, "end": v(-38.84, -22.42) * mm});
            skLineSegment(sketch, "E287", {"start": v(-38.84, -22.42) * mm, "end": v(-38.9, -22.32) * mm});
            skLineSegment(sketch, "E288", {"start": v(-38.9, -22.32) * mm, "end": v(-39.1, -21.92) * mm});
            skLineSegment(sketch, "E289", {"start": v(-39.1, -21.92) * mm, "end": v(-39.15, -21.67) * mm});
            skLineSegment(sketch, "E290", {"start": v(-39.15, -21.67) * mm, "end": v(-38.92, -21.27) * mm});
            skLineSegment(sketch, "E291", {"start": v(-38.92, -21.27) * mm, "end": v(-38.36, -20.6) * mm});
            skLineSegment(sketch, "E292", {"start": v(-38.36, -20.6) * mm, "end": v(-38.24, -20.45) * mm});
            skLineSegment(sketch, "E293", {"start": v(-38.24, -20.45) * mm, "end": v(-37.86, -20.05) * mm});
            skLineSegment(sketch, "E294", {"start": v(-37.86, -20.05) * mm, "end": v(-37.82, -20) * mm});
            skLineSegment(sketch, "E295", {"start": v(-37.82, -20) * mm, "end": v(-37.53, -19.72) * mm});
            skLineSegment(sketch, "E296", {"start": v(-37.53, -19.72) * mm, "end": v(-37.47, -19.68) * mm});
            skLineSegment(sketch, "E297", {"start": v(-37.47, -19.68) * mm, "end": v(-37.32, -19.52) * mm});
            skLineSegment(sketch, "E298", {"start": v(-37.32, -19.52) * mm, "end": v(-37.26, -19.47) * mm});
            skLineSegment(sketch, "E299", {"start": v(-37.26, -19.47) * mm, "end": v(-37.16, -19.4) * mm});
            skLineSegment(sketch, "E300", {"start": v(-37.16, -19.4) * mm, "end": v(-36.7, -18.95) * mm});
            skLineSegment(sketch, "E301", {"start": v(-36.7, -18.95) * mm, "end": v(-36.63, -18.87) * mm});
            skLineSegment(sketch, "E302", {"start": v(-36.63, -18.87) * mm, "end": v(-36.6, -18.83) * mm});
            skLineSegment(sketch, "E303", {"start": v(-36.6, -18.83) * mm, "end": v(-36.59, -18.77) * mm});
            skLineSegment(sketch, "E304", {"start": v(-36.59, -18.77) * mm, "end": v(-37.31, -17.28) * mm});
            skLineSegment(sketch, "E305", {"start": v(-37.31, -17.28) * mm, "end": v(-37.37, -17.26) * mm});
            skLineSegment(sketch, "E306", {"start": v(-37.37, -17.26) * mm, "end": v(-37.42, -17.24) * mm});
            skLineSegment(sketch, "E307", {"start": v(-37.42, -17.24) * mm, "end": v(-37.53, -17.25) * mm});
            skLineSegment(sketch, "E308", {"start": v(-37.53, -17.25) * mm, "end": v(-38.17, -17.34) * mm});
            skLineSegment(sketch, "E309", {"start": v(-38.17, -17.34) * mm, "end": v(-38.28, -17.38) * mm});
            skLineSegment(sketch, "E310", {"start": v(-38.28, -17.38) * mm, "end": v(-38.35, -17.4) * mm});
            skLineSegment(sketch, "E311", {"start": v(-38.35, -17.4) * mm, "end": v(-38.58, -17.41) * mm});
            skLineSegment(sketch, "E312", {"start": v(-38.58, -17.41) * mm, "end": v(-38.65, -17.44) * mm});
            skLineSegment(sketch, "E313", {"start": v(-38.65, -17.44) * mm, "end": v(-39.05, -17.49) * mm});
            skLineSegment(sketch, "E314", {"start": v(-39.05, -17.49) * mm, "end": v(-39.1, -17.5) * mm});
            skLineSegment(sketch, "E315", {"start": v(-39.1, -17.5) * mm, "end": v(-39.65, -17.54) * mm});
            skLineSegment(sketch, "E316", {"start": v(-39.65, -17.54) * mm, "end": v(-39.84, -17.55) * mm});
            skLineSegment(sketch, "E317", {"start": v(-39.84, -17.55) * mm, "end": v(-40.72, -17.57) * mm});
            skLineSegment(sketch, "E318", {"start": v(-40.72, -17.57) * mm, "end": v(-41.18, -17.5) * mm});
            skLineSegment(sketch, "E319", {"start": v(-41.18, -17.5) * mm, "end": v(-41.35, -17.32) * mm});
            skLineSegment(sketch, "E320", {"start": v(-41.35, -17.32) * mm, "end": v(-41.53, -16.91) * mm});
            skLineSegment(sketch, "E321", {"start": v(-41.53, -16.91) * mm, "end": v(-41.58, -16.8) * mm});
            skLineSegment(sketch, "E322", {"start": v(-41.58, -16.8) * mm, "end": v(-41.63, -16.69) * mm});
            skLineSegment(sketch, "E323", {"start": v(-41.63, -16.69) * mm, "end": v(-41.78, -16.27) * mm});
            skLineSegment(sketch, "E324", {"start": v(-41.78, -16.27) * mm, "end": v(-41.79, -16.01) * mm});
            skLineSegment(sketch, "E325", {"start": v(-41.79, -16.01) * mm, "end": v(-41.5, -15.65) * mm});
            skLineSegment(sketch, "E326", {"start": v(-41.5, -15.65) * mm, "end": v(-40.85, -15.05) * mm});
            skLineSegment(sketch, "E327", {"start": v(-40.85, -15.05) * mm, "end": v(-40.7, -14.93) * mm});
            skLineSegment(sketch, "E328", {"start": v(-40.7, -14.93) * mm, "end": v(-40.28, -14.58) * mm});
            skLineSegment(sketch, "E329", {"start": v(-40.28, -14.58) * mm, "end": v(-40.24, -14.55) * mm});
            skLineSegment(sketch, "E330", {"start": v(-40.24, -14.55) * mm, "end": v(-39.91, -14.3) * mm});
            skLineSegment(sketch, "E331", {"start": v(-39.91, -14.3) * mm, "end": v(-39.85, -14.27) * mm});
            skLineSegment(sketch, "E332", {"start": v(-39.85, -14.27) * mm, "end": v(-39.67, -14.13) * mm});
            skLineSegment(sketch, "E333", {"start": v(-39.67, -14.13) * mm, "end": v(-39.6, -14.1) * mm});
            skLineSegment(sketch, "E334", {"start": v(-39.6, -14.1) * mm, "end": v(-39.5, -14.04) * mm});
            skLineSegment(sketch, "E335", {"start": v(-39.5, -14.04) * mm, "end": v(-38.97, -13.66) * mm});
            skLineSegment(sketch, "E336", {"start": v(-38.97, -13.66) * mm, "end": v(-38.9, -13.6) * mm});
            skLineSegment(sketch, "E337", {"start": v(-38.9, -13.6) * mm, "end": v(-38.87, -13.55) * mm});
            skLineSegment(sketch, "E338", {"start": v(-38.87, -13.55) * mm, "end": v(-38.84, -13.5) * mm});
            skLineSegment(sketch, "E339", {"start": v(-38.84, -13.5) * mm, "end": v(-39.36, -11.92) * mm});
            skLineSegment(sketch, "E340", {"start": v(-39.36, -11.92) * mm, "end": v(-39.4, -11.89) * mm});
            skLineSegment(sketch, "E341", {"start": v(-39.4, -11.89) * mm, "end": v(-39.46, -11.87) * mm});
            skLineSegment(sketch, "E342", {"start": v(-39.46, -11.87) * mm, "end": v(-39.56, -11.86) * mm});
            skLineSegment(sketch, "E343", {"start": v(-39.56, -11.86) * mm, "end": v(-40.2, -11.86) * mm});
            skLineSegment(sketch, "E344", {"start": v(-40.2, -11.86) * mm, "end": v(-40.33, -11.88) * mm});
            skLineSegment(sketch, "E345", {"start": v(-40.33, -11.88) * mm, "end": v(-40.4, -11.88) * mm});
            skLineSegment(sketch, "E346", {"start": v(-40.4, -11.88) * mm, "end": v(-40.63, -11.88) * mm});
            skLineSegment(sketch, "E347", {"start": v(-40.63, -11.88) * mm, "end": v(-40.7, -11.89) * mm});
            skLineSegment(sketch, "E348", {"start": v(-40.7, -11.89) * mm, "end": v(-41.1, -11.88) * mm});
            skLineSegment(sketch, "E349", {"start": v(-41.1, -11.88) * mm, "end": v(-41.16, -11.88) * mm});
            skLineSegment(sketch, "E350", {"start": v(-41.16, -11.88) * mm, "end": v(-41.7, -11.85) * mm});
            skLineSegment(sketch, "E351", {"start": v(-41.7, -11.85) * mm, "end": v(-41.9, -11.83) * mm});
            skLineSegment(sketch, "E352", {"start": v(-41.9, -11.83) * mm, "end": v(-42.77, -11.74) * mm});
            skLineSegment(sketch, "E353", {"start": v(-42.77, -11.74) * mm, "end": v(-43.22, -11.6) * mm});
            skLineSegment(sketch, "E354", {"start": v(-43.22, -11.6) * mm, "end": v(-43.36, -11.4) * mm});
            skLineSegment(sketch, "E355", {"start": v(-43.36, -11.4) * mm, "end": v(-43.48, -10.97) * mm});
            skLineSegment(sketch, "E356", {"start": v(-43.48, -10.97) * mm, "end": v(-43.51, -10.85) * mm});
            skLineSegment(sketch, "E357", {"start": v(-43.51, -10.85) * mm, "end": v(-43.54, -10.73) * mm});
            skLineSegment(sketch, "E358", {"start": v(-43.54, -10.73) * mm, "end": v(-43.64, -10.3) * mm});
            skLineSegment(sketch, "E359", {"start": v(-43.64, -10.3) * mm, "end": v(-43.6, -10.04) * mm});
            skLineSegment(sketch, "E360", {"start": v(-43.6, -10.04) * mm, "end": v(-43.27, -9.72) * mm});
            skLineSegment(sketch, "E361", {"start": v(-43.27, -9.72) * mm, "end": v(-42.55, -9.22) * mm});
            skLineSegment(sketch, "E362", {"start": v(-42.55, -9.22) * mm, "end": v(-42.4, -9.12) * mm});
            skLineSegment(sketch, "E363", {"start": v(-42.4, -9.12) * mm, "end": v(-41.92, -8.83) * mm});
            skLineSegment(sketch, "E364", {"start": v(-41.92, -8.83) * mm, "end": v(-41.87, -8.8) * mm});
            skLineSegment(sketch, "E365", {"start": v(-41.87, -8.8) * mm, "end": v(-41.52, -8.61) * mm});
            skLineSegment(sketch, "E366", {"start": v(-41.52, -8.61) * mm, "end": v(-41.45, -8.59) * mm});
            skLineSegment(sketch, "E367", {"start": v(-41.45, -8.59) * mm, "end": v(-41.25, -8.47) * mm});
            skLineSegment(sketch, "E368", {"start": v(-41.25, -8.47) * mm, "end": v(-41.19, -8.44) * mm});
            skLineSegment(sketch, "E369", {"start": v(-41.19, -8.44) * mm, "end": v(-41.07, -8.4) * mm});
            skLineSegment(sketch, "E370", {"start": v(-41.07, -8.4) * mm, "end": v(-40.5, -8.1) * mm});
            skLineSegment(sketch, "E371", {"start": v(-40.5, -8.1) * mm, "end": v(-40.41, -8.05) * mm});
            skLineSegment(sketch, "E372", {"start": v(-40.41, -8.05) * mm, "end": v(-40.38, -8) * mm});
            skLineSegment(sketch, "E373", {"start": v(-40.38, -8) * mm, "end": v(-40.34, -7.95) * mm});
            skLineSegment(sketch, "E374", {"start": v(-40.34, -7.95) * mm, "end": v(-40.63, -6.32) * mm});
            skLineSegment(sketch, "E375", {"start": v(-40.63, -6.32) * mm, "end": v(-40.68, -6.29) * mm});
            skLineSegment(sketch, "E376", {"start": v(-40.68, -6.29) * mm, "end": v(-40.73, -6.26) * mm});
            skLineSegment(sketch, "E377", {"start": v(-40.73, -6.26) * mm, "end": v(-40.83, -6.23) * mm});
            skLineSegment(sketch, "E378", {"start": v(-40.83, -6.23) * mm, "end": v(-41.47, -6.15) * mm});
            skLineSegment(sketch, "E379", {"start": v(-41.47, -6.15) * mm, "end": v(-41.59, -6.15) * mm});
            skLineSegment(sketch, "E380", {"start": v(-41.59, -6.15) * mm, "end": v(-41.66, -6.15) * mm});
            skLineSegment(sketch, "E381", {"start": v(-41.66, -6.15) * mm, "end": v(-41.88, -6.1) * mm});
            skLineSegment(sketch, "E382", {"start": v(-41.88, -6.1) * mm, "end": v(-41.96, -6.1) * mm});
            skLineSegment(sketch, "E383", {"start": v(-41.96, -6.1) * mm, "end": v(-42.36, -6.04) * mm});
            skLineSegment(sketch, "E384", {"start": v(-42.36, -6.04) * mm, "end": v(-42.41, -6.04) * mm});
            skLineSegment(sketch, "E385", {"start": v(-42.41, -6.04) * mm, "end": v(-42.95, -5.93) * mm});
            skLineSegment(sketch, "E386", {"start": v(-42.95, -5.93) * mm, "end": v(-43.13, -5.89) * mm});
            skLineSegment(sketch, "E387", {"start": v(-43.13, -5.89) * mm, "end": v(-43.99, -5.67) * mm});
            skLineSegment(sketch, "E388", {"start": v(-43.99, -5.67) * mm, "end": v(-44.41, -5.48) * mm});
            skLineSegment(sketch, "E389", {"start": v(-44.41, -5.48) * mm, "end": v(-44.52, -5.25) * mm});
            skLineSegment(sketch, "E390", {"start": v(-44.52, -5.25) * mm, "end": v(-44.59, -4.8) * mm});
            skLineSegment(sketch, "E391", {"start": v(-44.59, -4.8) * mm, "end": v(-44.6, -4.69) * mm});
            skLineSegment(sketch, "E392", {"start": v(-44.6, -4.69) * mm, "end": v(-44.61, -4.57) * mm});
            skLineSegment(sketch, "E393", {"start": v(-44.61, -4.57) * mm, "end": v(-44.64, -4.12) * mm});
            skLineSegment(sketch, "E394", {"start": v(-44.64, -4.12) * mm, "end": v(-44.58, -3.88) * mm});
            skLineSegment(sketch, "E395", {"start": v(-44.58, -3.88) * mm, "end": v(-44.2, -3.6) * mm});
            skLineSegment(sketch, "E396", {"start": v(-44.2, -3.6) * mm, "end": v(-43.42, -3.2) * mm});
            skLineSegment(sketch, "E397", {"start": v(-43.42, -3.2) * mm, "end": v(-43.25, -3.13) * mm});
            skLineSegment(sketch, "E398", {"start": v(-43.25, -3.13) * mm, "end": v(-42.74, -2.91) * mm});
            skLineSegment(sketch, "E399", {"start": v(-42.74, -2.91) * mm, "end": v(-42.69, -2.9) * mm});
            skLineSegment(sketch, "E400", {"start": v(-42.69, -2.9) * mm, "end": v(-42.31, -2.75) * mm});
            skLineSegment(sketch, "E401", {"start": v(-42.31, -2.75) * mm, "end": v(-42.24, -2.74) * mm});
            skLineSegment(sketch, "E402", {"start": v(-42.24, -2.74) * mm, "end": v(-42.03, -2.65) * mm});
            skLineSegment(sketch, "E403", {"start": v(-42.03, -2.65) * mm, "end": v(-41.96, -2.63) * mm});
            skLineSegment(sketch, "E404", {"start": v(-41.96, -2.63) * mm, "end": v(-41.84, -2.61) * mm});
            skLineSegment(sketch, "E405", {"start": v(-41.84, -2.61) * mm, "end": v(-41.23, -2.4) * mm});
            skLineSegment(sketch, "E406", {"start": v(-41.23, -2.4) * mm, "end": v(-41.14, -2.34) * mm});
            skLineSegment(sketch, "E407", {"start": v(-41.14, -2.34) * mm, "end": v(-41.1, -2.3) * mm});
            skLineSegment(sketch, "E408", {"start": v(-41.1, -2.3) * mm, "end": v(-41.06, -2.26) * mm});
            skLineSegment(sketch, "E409", {"start": v(-41.06, -2.26) * mm, "end": v(-41.12, -0.6) * mm});
            skLineSegment(sketch, "E410", {"start": v(-41.12, -0.6) * mm, "end": v(-41.16, -0.56) * mm});
            skLineSegment(sketch, "E411", {"start": v(-41.16, -0.56) * mm, "end": v(-41.2, -0.53) * mm});
            skLineSegment(sketch, "E412", {"start": v(-41.2, -0.53) * mm, "end": v(-41.3, -0.5) * mm});
            skLineSegment(sketch, "E413", {"start": v(-41.3, -0.5) * mm, "end": v(-41.92, -0.31) * mm});
            skLineSegment(sketch, "E414", {"start": v(-41.92, -0.31) * mm, "end": v(-42.04, -0.3) * mm});
            skLineSegment(sketch, "E415", {"start": v(-42.04, -0.3) * mm, "end": v(-42.11, -0.29) * mm});
            skLineSegment(sketch, "E416", {"start": v(-42.11, -0.29) * mm, "end": v(-42.33, -0.22) * mm});
            skLineSegment(sketch, "E417", {"start": v(-42.33, -0.22) * mm, "end": v(-42.4, -0.2) * mm});
            skLineSegment(sketch, "E418", {"start": v(-42.4, -0.2) * mm, "end": v(-42.79, -0.1) * mm});
            skLineSegment(sketch, "E419", {"start": v(-42.79, -0.1) * mm, "end": v(-42.84, -0.07) * mm});
            skLineSegment(sketch, "E420", {"start": v(-42.84, -0.07) * mm, "end": v(-43.36, 0.1) * mm});
            skLineSegment(sketch, "E421", {"start": v(-43.36, 0.1) * mm, "end": v(-43.53, 0.17) * mm});
            skLineSegment(sketch, "E422", {"start": v(-43.53, 0.17) * mm, "end": v(-44.35, 0.5) * mm});
            skLineSegment(sketch, "E423", {"start": v(-44.35, 0.5) * mm, "end": v(-44.74, 0.76) * mm});
            skLineSegment(sketch, "E424", {"start": v(-44.74, 0.76) * mm, "end": v(-44.82, 1) * mm});
            skLineSegment(sketch, "E425", {"start": v(-44.82, 1) * mm, "end": v(-44.82, 1.44) * mm});
            skLineSegment(sketch, "E426", {"start": v(-44.82, 1.44) * mm, "end": v(-44.82, 1.56) * mm});
            skLineSegment(sketch, "E427", {"start": v(-44.82, 1.56) * mm, "end": v(-44.81, 1.69) * mm});
            skLineSegment(sketch, "E428", {"start": v(-44.81, 1.69) * mm, "end": v(-44.78, 2.13) * mm});
            skLineSegment(sketch, "E429", {"start": v(-44.78, 2.13) * mm, "end": v(-44.69, 2.37) * mm});
            skLineSegment(sketch, "E430", {"start": v(-44.69, 2.37) * mm, "end": v(-44.28, 2.59) * mm});
            skLineSegment(sketch, "E431", {"start": v(-44.28, 2.59) * mm, "end": v(-43.44, 2.87) * mm});
            skLineSegment(sketch, "E432", {"start": v(-43.44, 2.87) * mm, "end": v(-43.26, 2.92) * mm});
            skLineSegment(sketch, "E433", {"start": v(-43.26, 2.92) * mm, "end": v(-42.73, 3.06) * mm});
            skLineSegment(sketch, "E434", {"start": v(-42.73, 3.06) * mm, "end": v(-42.68, 3.08) * mm});
            skLineSegment(sketch, "E435", {"start": v(-42.68, 3.08) * mm, "end": v(-42.28, 3.17) * mm});
            skLineSegment(sketch, "E436", {"start": v(-42.28, 3.17) * mm, "end": v(-42.2, 3.17) * mm});
            skLineSegment(sketch, "E437", {"start": v(-42.2, 3.17) * mm, "end": v(-41.99, 3.22) * mm});
            skLineSegment(sketch, "E438", {"start": v(-41.99, 3.22) * mm, "end": v(-41.92, 3.24) * mm});
            skLineSegment(sketch, "E439", {"start": v(-41.92, 3.24) * mm, "end": v(-41.8, 3.24) * mm});
            skLineSegment(sketch, "E440", {"start": v(-41.8, 3.24) * mm, "end": v(-41.16, 3.37) * mm});
            skLineSegment(sketch, "E441", {"start": v(-41.16, 3.37) * mm, "end": v(-41.06, 3.4) * mm});
            skLineSegment(sketch, "E442", {"start": v(-41.06, 3.4) * mm, "end": v(-41.02, 3.43) * mm});
            skLineSegment(sketch, "E443", {"start": v(-41.02, 3.43) * mm, "end": v(-40.97, 3.48) * mm});
            skLineSegment(sketch, "E444", {"start": v(-40.97, 3.48) * mm, "end": v(-40.8, 5.12) * mm});
            skLineSegment(sketch, "E445", {"start": v(-40.8, 5.12) * mm, "end": v(-40.84, 5.17) * mm});
            skLineSegment(sketch, "E446", {"start": v(-40.84, 5.17) * mm, "end": v(-40.87, 5.2) * mm});
            skLineSegment(sketch, "E447", {"start": v(-40.87, 5.2) * mm, "end": v(-40.96, 5.26) * mm});
            skLineSegment(sketch, "E448", {"start": v(-40.96, 5.26) * mm, "end": v(-41.56, 5.52) * mm});
            skLineSegment(sketch, "E449", {"start": v(-41.56, 5.52) * mm, "end": v(-41.67, 5.55) * mm});
            skLineSegment(sketch, "E450", {"start": v(-41.67, 5.55) * mm, "end": v(-41.74, 5.58) * mm});
            skLineSegment(sketch, "E451", {"start": v(-41.74, 5.58) * mm, "end": v(-41.94, 5.68) * mm});
            skLineSegment(sketch, "E452", {"start": v(-41.94, 5.68) * mm, "end": v(-42.02, 5.7) * mm});
            skLineSegment(sketch, "E453", {"start": v(-42.02, 5.7) * mm, "end": v(-42.38, 5.86) * mm});
            skLineSegment(sketch, "E454", {"start": v(-42.38, 5.86) * mm, "end": v(-42.43, 5.89) * mm});
            skLineSegment(sketch, "E455", {"start": v(-42.43, 5.89) * mm, "end": v(-42.92, 6.14) * mm});
            skLineSegment(sketch, "E456", {"start": v(-42.92, 6.14) * mm, "end": v(-43.09, 6.23) * mm});
            skLineSegment(sketch, "E457", {"start": v(-43.09, 6.23) * mm, "end": v(-43.85, 6.68) * mm});
            skLineSegment(sketch, "E458", {"start": v(-43.85, 6.68) * mm, "end": v(-44.2, 6.98) * mm});
            skLineSegment(sketch, "E459", {"start": v(-44.2, 6.98) * mm, "end": v(-44.25, 7.22) * mm});
            skLineSegment(sketch, "E460", {"start": v(-44.25, 7.22) * mm, "end": v(-44.19, 7.67) * mm});
            skLineSegment(sketch, "E461", {"start": v(-44.19, 7.67) * mm, "end": v(-44.16, 7.79) * mm});
            skLineSegment(sketch, "E462", {"start": v(-44.16, 7.79) * mm, "end": v(-44.14, 7.9) * mm});
            skLineSegment(sketch, "E463", {"start": v(-44.14, 7.9) * mm, "end": v(-44.05, 8.35) * mm});
            skLineSegment(sketch, "E464", {"start": v(-44.05, 8.35) * mm, "end": v(-43.92, 8.56) * mm});
            skLineSegment(sketch, "E465", {"start": v(-43.92, 8.56) * mm, "end": v(-43.48, 8.72) * mm});
            skLineSegment(sketch, "E466", {"start": v(-43.48, 8.72) * mm, "end": v(-42.62, 8.88) * mm});
            skLineSegment(sketch, "E467", {"start": v(-42.62, 8.88) * mm, "end": v(-42.43, 8.91) * mm});
            skLineSegment(sketch, "E468", {"start": v(-42.43, 8.91) * mm, "end": v(-41.89, 8.98) * mm});
            skLineSegment(sketch, "E469", {"start": v(-41.89, 8.98) * mm, "end": v(-41.83, 8.98) * mm});
            skLineSegment(sketch, "E470", {"start": v(-41.83, 8.98) * mm, "end": v(-41.43, 9.02) * mm});
            skLineSegment(sketch, "E471", {"start": v(-41.43, 9.02) * mm, "end": v(-41.36, 9.01) * mm});
            skLineSegment(sketch, "E472", {"start": v(-41.36, 9.01) * mm, "end": v(-41.13, 9.04) * mm});
            skLineSegment(sketch, "E473", {"start": v(-41.13, 9.04) * mm, "end": v(-41.06, 9.04) * mm});
            skLineSegment(sketch, "E474", {"start": v(-41.06, 9.04) * mm, "end": v(-40.94, 9.02) * mm});
            skLineSegment(sketch, "E475", {"start": v(-40.94, 9.02) * mm, "end": v(-40.3, 9.07) * mm});
            skLineSegment(sketch, "E476", {"start": v(-40.3, 9.07) * mm, "end": v(-40.19, 9.09) * mm});
            skLineSegment(sketch, "E477", {"start": v(-40.19, 9.09) * mm, "end": v(-40.14, 9.1) * mm});
            skLineSegment(sketch, "E478", {"start": v(-40.14, 9.1) * mm, "end": v(-40.1, 9.14) * mm});
            skLineSegment(sketch, "E479", {"start": v(-40.1, 9.14) * mm, "end": v(-39.7, 10.75) * mm});
            skLineSegment(sketch, "E480", {"start": v(-39.7, 10.75) * mm, "end": v(-39.72, 10.8) * mm});
            skLineSegment(sketch, "E481", {"start": v(-39.72, 10.8) * mm, "end": v(-39.75, 10.84) * mm});
            skLineSegment(sketch, "E482", {"start": v(-39.75, 10.84) * mm, "end": v(-39.83, 10.9) * mm});
            skLineSegment(sketch, "E483", {"start": v(-39.83, 10.9) * mm, "end": v(-40.38, 11.25) * mm});
            skLineSegment(sketch, "E484", {"start": v(-40.38, 11.25) * mm, "end": v(-40.5, 11.3) * mm});
            skLineSegment(sketch, "E485", {"start": v(-40.5, 11.3) * mm, "end": v(-40.56, 11.33) * mm});
            skLineSegment(sketch, "E486", {"start": v(-40.56, 11.33) * mm, "end": v(-40.75, 11.46) * mm});
            skLineSegment(sketch, "E487", {"start": v(-40.75, 11.46) * mm, "end": v(-40.81, 11.49) * mm});
            skLineSegment(sketch, "E488", {"start": v(-40.81, 11.49) * mm, "end": v(-41.15, 11.7) * mm});
            skLineSegment(sketch, "E489", {"start": v(-41.15, 11.7) * mm, "end": v(-41.2, 11.74) * mm});
            skLineSegment(sketch, "E490", {"start": v(-41.2, 11.74) * mm, "end": v(-41.65, 12.05) * mm});
            skLineSegment(sketch, "E491", {"start": v(-41.65, 12.05) * mm, "end": v(-41.8, 12.17) * mm});
            skLineSegment(sketch, "E492", {"start": v(-41.8, 12.17) * mm, "end": v(-42.5, 12.71) * mm});
            skLineSegment(sketch, "E493", {"start": v(-42.5, 12.71) * mm, "end": v(-42.8, 13.06) * mm});
            skLineSegment(sketch, "E494", {"start": v(-42.8, 13.06) * mm, "end": v(-42.81, 13.31) * mm});
            skLineSegment(sketch, "E495", {"start": v(-42.81, 13.31) * mm, "end": v(-42.69, 13.74) * mm});
            skLineSegment(sketch, "E496", {"start": v(-42.69, 13.74) * mm, "end": v(-42.65, 13.86) * mm});
            skLineSegment(sketch, "E497", {"start": v(-42.65, 13.86) * mm, "end": v(-42.61, 13.97) * mm});
            skLineSegment(sketch, "E498", {"start": v(-42.61, 13.97) * mm, "end": v(-42.46, 14.4) * mm});
            skLineSegment(sketch, "E499", {"start": v(-42.46, 14.4) * mm, "end": v(-42.3, 14.6) * mm});
            skLineSegment(sketch, "E500", {"start": v(-42.3, 14.6) * mm, "end": v(-41.85, 14.7) * mm});
            skLineSegment(sketch, "E501", {"start": v(-41.85, 14.7) * mm, "end": v(-40.97, 14.73) * mm});
            skLineSegment(sketch, "E502", {"start": v(-40.97, 14.73) * mm, "end": v(-40.78, 14.73) * mm});
            skLineSegment(sketch, "E503", {"start": v(-40.78, 14.73) * mm, "end": v(-40.23, 14.72) * mm});
            skLineSegment(sketch, "E504", {"start": v(-40.23, 14.72) * mm, "end": v(-40.18, 14.72) * mm});
            skLineSegment(sketch, "E505", {"start": v(-40.18, 14.72) * mm, "end": v(-39.77, 14.7) * mm});
            skLineSegment(sketch, "E506", {"start": v(-39.77, 14.7) * mm, "end": v(-39.7, 14.68) * mm});
            skLineSegment(sketch, "E507", {"start": v(-39.7, 14.68) * mm, "end": v(-39.47, 14.67) * mm});
            skLineSegment(sketch, "E508", {"start": v(-39.47, 14.67) * mm, "end": v(-39.4, 14.67) * mm});
            skLineSegment(sketch, "E509", {"start": v(-39.4, 14.67) * mm, "end": v(-39.28, 14.63) * mm});
            skLineSegment(sketch, "E510", {"start": v(-39.28, 14.63) * mm, "end": v(-38.64, 14.59) * mm});
            skLineSegment(sketch, "E511", {"start": v(-38.64, 14.59) * mm, "end": v(-38.53, 14.6) * mm});
            skLineSegment(sketch, "E512", {"start": v(-38.53, 14.6) * mm, "end": v(-38.48, 14.6) * mm});
            skLineSegment(sketch, "E513", {"start": v(-38.48, 14.6) * mm, "end": v(-38.43, 14.63) * mm});
            skLineSegment(sketch, "E514", {"start": v(-38.43, 14.63) * mm, "end": v(-37.8, 16.17) * mm});
            skLineSegment(sketch, "E515", {"start": v(-37.8, 16.17) * mm, "end": v(-37.83, 16.23) * mm});
            skLineSegment(sketch, "E516", {"start": v(-37.83, 16.23) * mm, "end": v(-37.86, 16.27) * mm});
            skLineSegment(sketch, "E517", {"start": v(-37.86, 16.27) * mm, "end": v(-37.93, 16.35) * mm});
            skLineSegment(sketch, "E518", {"start": v(-37.93, 16.35) * mm, "end": v(-38.42, 16.76) * mm});
            skLineSegment(sketch, "E519", {"start": v(-38.42, 16.76) * mm, "end": v(-38.53, 16.82) * mm});
            skLineSegment(sketch, "E520", {"start": v(-38.53, 16.82) * mm, "end": v(-38.59, 16.87) * mm});
            skLineSegment(sketch, "E521", {"start": v(-38.59, 16.87) * mm, "end": v(-38.76, 17.02) * mm});
            skLineSegment(sketch, "E522", {"start": v(-38.76, 17.02) * mm, "end": v(-38.82, 17.06) * mm});
            skLineSegment(sketch, "E523", {"start": v(-38.82, 17.06) * mm, "end": v(-39.13, 17.32) * mm});
            skLineSegment(sketch, "E524", {"start": v(-39.13, 17.32) * mm, "end": v(-39.17, 17.36) * mm});
            skLineSegment(sketch, "E525", {"start": v(-39.17, 17.36) * mm, "end": v(-39.57, 17.73) * mm});
            skLineSegment(sketch, "E526", {"start": v(-39.57, 17.73) * mm, "end": v(-39.7, 17.86) * mm});
            skLineSegment(sketch, "E527", {"start": v(-39.7, 17.86) * mm, "end": v(-40.3, 18.5) * mm});
            skLineSegment(sketch, "E528", {"start": v(-40.3, 18.5) * mm, "end": v(-40.57, 18.89) * mm});
            skLineSegment(sketch, "E529", {"start": v(-40.57, 18.89) * mm, "end": v(-40.54, 19.14) * mm});
            skLineSegment(sketch, "E530", {"start": v(-40.54, 19.14) * mm, "end": v(-40.36, 19.55) * mm});
            skLineSegment(sketch, "E531", {"start": v(-40.36, 19.55) * mm, "end": v(-40.3, 19.66) * mm});
            skLineSegment(sketch, "E532", {"start": v(-40.3, 19.66) * mm, "end": v(-40.25, 19.77) * mm});
            skLineSegment(sketch, "E533", {"start": v(-40.25, 19.77) * mm, "end": v(-40.04, 20.16) * mm});
            skLineSegment(sketch, "E534", {"start": v(-40.04, 20.16) * mm, "end": v(-39.86, 20.34) * mm});
            skLineSegment(sketch, "E535", {"start": v(-39.86, 20.34) * mm, "end": v(-39.4, 20.37) * mm});
            skLineSegment(sketch, "E536", {"start": v(-39.4, 20.37) * mm, "end": v(-38.52, 20.29) * mm});
            skLineSegment(sketch, "E537", {"start": v(-38.52, 20.29) * mm, "end": v(-38.33, 20.26) * mm});
            skLineSegment(sketch, "E538", {"start": v(-38.33, 20.26) * mm, "end": v(-37.8, 20.18) * mm});
            skLineSegment(sketch, "E539", {"start": v(-37.8, 20.18) * mm, "end": v(-37.74, 20.17) * mm});
            skLineSegment(sketch, "E540", {"start": v(-37.74, 20.17) * mm, "end": v(-37.34, 20.09) * mm});
            skLineSegment(sketch, "E541", {"start": v(-37.34, 20.09) * mm, "end": v(-37.27, 20.06) * mm});
            skLineSegment(sketch, "E542", {"start": v(-37.27, 20.06) * mm, "end": v(-37.05, 20.02) * mm});
            skLineSegment(sketch, "E543", {"start": v(-37.05, 20.02) * mm, "end": v(-36.98, 20) * mm});
            skLineSegment(sketch, "E544", {"start": v(-36.98, 20) * mm, "end": v(-36.86, 19.96) * mm});
            skLineSegment(sketch, "E545", {"start": v(-36.86, 19.96) * mm, "end": v(-36.23, 19.82) * mm});
            skLineSegment(sketch, "E546", {"start": v(-36.23, 19.82) * mm, "end": v(-36.13, 19.81) * mm});
            skLineSegment(sketch, "E547", {"start": v(-36.13, 19.81) * mm, "end": v(-36.08, 19.82) * mm});
            skLineSegment(sketch, "E548", {"start": v(-36.08, 19.82) * mm, "end": v(-36.02, 19.84) * mm});
            skLineSegment(sketch, "E549", {"start": v(-36.02, 19.84) * mm, "end": v(-35.2, 21.27) * mm});
            skLineSegment(sketch, "E550", {"start": v(-35.2, 21.27) * mm, "end": v(-35.2, 21.33) * mm});
            skLineSegment(sketch, "E551", {"start": v(-35.2, 21.33) * mm, "end": v(-35.22, 21.38) * mm});
            skLineSegment(sketch, "E552", {"start": v(-35.22, 21.38) * mm, "end": v(-35.28, 21.47) * mm});
            skLineSegment(sketch, "E553", {"start": v(-35.28, 21.47) * mm, "end": v(-35.72, 21.95) * mm});
            skLineSegment(sketch, "E554", {"start": v(-35.72, 21.95) * mm, "end": v(-35.81, 22.02) * mm});
            skLineSegment(sketch, "E555", {"start": v(-35.81, 22.02) * mm, "end": v(-35.87, 22.07) * mm});
            skLineSegment(sketch, "E556", {"start": v(-35.87, 22.07) * mm, "end": v(-36.01, 22.25) * mm});
            skLineSegment(sketch, "E557", {"start": v(-36.01, 22.25) * mm, "end": v(-36.07, 22.3) * mm});
            skLineSegment(sketch, "E558", {"start": v(-36.07, 22.3) * mm, "end": v(-36.33, 22.6) * mm});
            skLineSegment(sketch, "E559", {"start": v(-36.33, 22.6) * mm, "end": v(-36.37, 22.64) * mm});
            skLineSegment(sketch, "E560", {"start": v(-36.37, 22.64) * mm, "end": v(-36.72, 23.07) * mm});
            skLineSegment(sketch, "E561", {"start": v(-36.72, 23.07) * mm, "end": v(-36.83, 23.22) * mm});
            skLineSegment(sketch, "E562", {"start": v(-36.83, 23.22) * mm, "end": v(-37.34, 23.93) * mm});
            skLineSegment(sketch, "E563", {"start": v(-37.34, 23.93) * mm, "end": v(-37.54, 24.35) * mm});
            skLineSegment(sketch, "E564", {"start": v(-37.54, 24.35) * mm, "end": v(-37.48, 24.6) * mm});
            skLineSegment(sketch, "E565", {"start": v(-37.48, 24.6) * mm, "end": v(-37.25, 24.98) * mm});
            skLineSegment(sketch, "E566", {"start": v(-37.25, 24.98) * mm, "end": v(-37.18, 25.08) * mm});
            skLineSegment(sketch, "E567", {"start": v(-37.18, 25.08) * mm, "end": v(-37.11, 25.18) * mm});
            skLineSegment(sketch, "E568", {"start": v(-37.11, 25.18) * mm, "end": v(-36.85, 25.54) * mm});
            skLineSegment(sketch, "E569", {"start": v(-36.85, 25.54) * mm, "end": v(-36.64, 25.69) * mm});
            skLineSegment(sketch, "E570", {"start": v(-36.64, 25.69) * mm, "end": v(-36.18, 25.66) * mm});
            skLineSegment(sketch, "E571", {"start": v(-36.18, 25.66) * mm, "end": v(-35.32, 25.45) * mm});
            skLineSegment(sketch, "E572", {"start": v(-35.32, 25.45) * mm, "end": v(-35.14, 25.4) * mm});
            skLineSegment(sketch, "E573", {"start": v(-35.14, 25.4) * mm, "end": v(-34.62, 25.24) * mm});
            skLineSegment(sketch, "E574", {"start": v(-34.62, 25.24) * mm, "end": v(-34.56, 25.22) * mm});
            skLineSegment(sketch, "E575", {"start": v(-34.56, 25.22) * mm, "end": v(-34.18, 25.1) * mm});
            skLineSegment(sketch, "E576", {"start": v(-34.18, 25.1) * mm, "end": v(-34.12, 25.05) * mm});
            skLineSegment(sketch, "E577", {"start": v(-34.12, 25.05) * mm, "end": v(-33.9, 24.99) * mm});
            skLineSegment(sketch, "E578", {"start": v(-33.9, 24.99) * mm, "end": v(-33.83, 24.96) * mm});
            skLineSegment(sketch, "E579", {"start": v(-33.83, 24.96) * mm, "end": v(-33.73, 24.9) * mm});
            skLineSegment(sketch, "E580", {"start": v(-33.73, 24.9) * mm, "end": v(-33.12, 24.67) * mm});
            skLineSegment(sketch, "E581", {"start": v(-33.12, 24.67) * mm, "end": v(-33.02, 24.65) * mm});
            skLineSegment(sketch, "E582", {"start": v(-33.02, 24.65) * mm, "end": v(-32.97, 24.65) * mm});
            skLineSegment(sketch, "E583", {"start": v(-32.97, 24.65) * mm, "end": v(-32.9, 24.66) * mm});
            skLineSegment(sketch, "E584", {"start": v(-32.9, 24.66) * mm, "end": v(-31.89, 25.96) * mm});
            skLineSegment(sketch, "E585", {"start": v(-31.89, 25.96) * mm, "end": v(-31.9, 26.02) * mm});
            skLineSegment(sketch, "E586", {"start": v(-31.9, 26.02) * mm, "end": v(-31.9, 26.08) * mm});
            skLineSegment(sketch, "E587", {"start": v(-31.9, 26.08) * mm, "end": v(-31.95, 26.17) * mm});
            skLineSegment(sketch, "E588", {"start": v(-31.95, 26.17) * mm, "end": v(-32.31, 26.7) * mm});
            skLineSegment(sketch, "E589", {"start": v(-32.31, 26.7) * mm, "end": v(-32.4, 26.79) * mm});
            skLineSegment(sketch, "E590", {"start": v(-32.4, 26.79) * mm, "end": v(-32.44, 26.85) * mm});
            skLineSegment(sketch, "E591", {"start": v(-32.44, 26.85) * mm, "end": v(-32.56, 27.04) * mm});
            skLineSegment(sketch, "E592", {"start": v(-32.56, 27.04) * mm, "end": v(-32.61, 27.1) * mm});
            skLineSegment(sketch, "E593", {"start": v(-32.61, 27.1) * mm, "end": v(-32.84, 27.43) * mm});
            skLineSegment(sketch, "E594", {"start": v(-32.84, 27.43) * mm, "end": v(-32.87, 27.48) * mm});
            skLineSegment(sketch, "E595", {"start": v(-32.87, 27.48) * mm, "end": v(-33.15, 27.95) * mm});
            skLineSegment(sketch, "E596", {"start": v(-33.15, 27.95) * mm, "end": v(-33.24, 28.12) * mm});
            skLineSegment(sketch, "E597", {"start": v(-33.24, 28.12) * mm, "end": v(-33.65, 28.9) * mm});
            skLineSegment(sketch, "E598", {"start": v(-33.65, 28.9) * mm, "end": v(-33.79, 29.34) * mm});
            skLineSegment(sketch, "E599", {"start": v(-33.79, 29.34) * mm, "end": v(-33.7, 29.57) * mm});
            skLineSegment(sketch, "E600", {"start": v(-33.7, 29.57) * mm, "end": v(-33.4, 29.92) * mm});
            skLineSegment(sketch, "E601", {"start": v(-33.4, 29.92) * mm, "end": v(-33.32, 30) * mm});
            skLineSegment(sketch, "E602", {"start": v(-33.32, 30) * mm, "end": v(-33.25, 30.1) * mm});
            skLineSegment(sketch, "E603", {"start": v(-33.25, 30.1) * mm, "end": v(-32.93, 30.42) * mm});
            skLineSegment(sketch, "E604", {"start": v(-32.93, 30.42) * mm, "end": v(-32.71, 30.54) * mm});
            skLineSegment(sketch, "E605", {"start": v(-32.71, 30.54) * mm, "end": v(-32.25, 30.44) * mm});
            skLineSegment(sketch, "E606", {"start": v(-32.25, 30.44) * mm, "end": v(-31.44, 30.12) * mm});
            skLineSegment(sketch, "E607", {"start": v(-31.44, 30.12) * mm, "end": v(-31.26, 30.05) * mm});
            skLineSegment(sketch, "E608", {"start": v(-31.26, 30.05) * mm, "end": v(-30.77, 29.81) * mm});
            skLineSegment(sketch, "E609", {"start": v(-30.77, 29.81) * mm, "end": v(-30.72, 29.79) * mm});
            skLineSegment(sketch, "E610", {"start": v(-30.72, 29.79) * mm, "end": v(-30.36, 29.6) * mm});
            skLineSegment(sketch, "E611", {"start": v(-30.36, 29.6) * mm, "end": v(-30.3, 29.56) * mm});
            skLineSegment(sketch, "E612", {"start": v(-30.3, 29.56) * mm, "end": v(-30.1, 29.46) * mm});
            skLineSegment(sketch, "E613", {"start": v(-30.1, 29.46) * mm, "end": v(-30.03, 29.42) * mm});
            skLineSegment(sketch, "E614", {"start": v(-30.03, 29.42) * mm, "end": v(-29.94, 29.35) * mm});
            skLineSegment(sketch, "E615", {"start": v(-29.94, 29.35) * mm, "end": v(-29.36, 29.04) * mm});
            skLineSegment(sketch, "E616", {"start": v(-29.36, 29.04) * mm, "end": v(-29.27, 29) * mm});
            skLineSegment(sketch, "E617", {"start": v(-29.27, 29) * mm, "end": v(-29.22, 29) * mm});
            skLineSegment(sketch, "E618", {"start": v(-29.22, 29) * mm, "end": v(-29.15, 29) * mm});
            skLineSegment(sketch, "E619", {"start": v(-29.15, 29) * mm, "end": v(-27.96, 30.15) * mm});
            skLineSegment(sketch, "E620", {"start": v(-27.96, 30.15) * mm, "end": v(-27.96, 30.21) * mm});
            skLineSegment(sketch, "E621", {"start": v(-27.96, 30.21) * mm, "end": v(-27.96, 30.26) * mm});
            skLineSegment(sketch, "E622", {"start": v(-27.96, 30.26) * mm, "end": v(-28, 30.36) * mm});
            skLineSegment(sketch, "E623", {"start": v(-28, 30.36) * mm, "end": v(-28.28, 30.94) * mm});
            skLineSegment(sketch, "E624", {"start": v(-28.28, 30.94) * mm, "end": v(-28.36, 31.04) * mm});
            skLineSegment(sketch, "E625", {"start": v(-28.36, 31.04) * mm, "end": v(-28.4, 31.1) * mm});
            skLineSegment(sketch, "E626", {"start": v(-28.4, 31.1) * mm, "end": v(-28.48, 31.3) * mm});
            skLineSegment(sketch, "E627", {"start": v(-28.48, 31.3) * mm, "end": v(-28.53, 31.37) * mm});
            skLineSegment(sketch, "E628", {"start": v(-28.53, 31.37) * mm, "end": v(-28.7, 31.74) * mm});
            skLineSegment(sketch, "E629", {"start": v(-28.7, 31.74) * mm, "end": v(-28.72, 31.79) * mm});
            skLineSegment(sketch, "E630", {"start": v(-28.72, 31.79) * mm, "end": v(-28.94, 32.3) * mm});
            skLineSegment(sketch, "E631", {"start": v(-28.94, 32.3) * mm, "end": v(-29, 32.47) * mm});
            skLineSegment(sketch, "E632", {"start": v(-29, 32.47) * mm, "end": v(-29.3, 33.3) * mm});
            skLineSegment(sketch, "E633", {"start": v(-29.3, 33.3) * mm, "end": v(-29.38, 33.76) * mm});
            skLineSegment(sketch, "E634", {"start": v(-29.38, 33.76) * mm, "end": v(-29.25, 33.98) * mm});
            skLineSegment(sketch, "E635", {"start": v(-29.25, 33.98) * mm, "end": v(-28.92, 34.28) * mm});
            skLineSegment(sketch, "E636", {"start": v(-28.92, 34.28) * mm, "end": v(-28.82, 34.35) * mm});
            skLineSegment(sketch, "E637", {"start": v(-28.82, 34.35) * mm, "end": v(-28.73, 34.43) * mm});
            skLineSegment(sketch, "E638", {"start": v(-28.73, 34.43) * mm, "end": v(-28.38, 34.7) * mm});
            skLineSegment(sketch, "E639", {"start": v(-28.38, 34.7) * mm, "end": v(-28.14, 34.8) * mm});
            skLineSegment(sketch, "E640", {"start": v(-28.14, 34.8) * mm, "end": v(-27.7, 34.63) * mm});
            skLineSegment(sketch, "E641", {"start": v(-27.7, 34.63) * mm, "end": v(-26.94, 34.2) * mm});
            skLineSegment(sketch, "E642", {"start": v(-26.94, 34.2) * mm, "end": v(-26.78, 34.1) * mm});
            skLineSegment(sketch, "E643", {"start": v(-26.78, 34.1) * mm, "end": v(-26.32, 33.8) * mm});
            skLineSegment(sketch, "E644", {"start": v(-26.32, 33.8) * mm, "end": v(-26.27, 33.77) * mm});
            skLineSegment(sketch, "E645", {"start": v(-26.27, 33.77) * mm, "end": v(-25.94, 33.54) * mm});
            skLineSegment(sketch, "E646", {"start": v(-25.94, 33.54) * mm, "end": v(-25.89, 33.49) * mm});
            skLineSegment(sketch, "E647", {"start": v(-25.89, 33.49) * mm, "end": v(-25.7, 33.36) * mm});
            skLineSegment(sketch, "E648", {"start": v(-25.7, 33.36) * mm, "end": v(-25.64, 33.32) * mm});
            skLineSegment(sketch, "E649", {"start": v(-25.64, 33.32) * mm, "end": v(-25.56, 33.23) * mm});
            skLineSegment(sketch, "E650", {"start": v(-25.56, 33.23) * mm, "end": v(-25.04, 32.84) * mm});
            skLineSegment(sketch, "E651", {"start": v(-25.04, 32.84) * mm, "end": v(-24.95, 32.8) * mm});
            skLineSegment(sketch, "E652", {"start": v(-24.95, 32.8) * mm, "end": v(-24.9, 32.78) * mm});
            skLineSegment(sketch, "E653", {"start": v(-24.9, 32.78) * mm, "end": v(-24.83, 32.77) * mm});
            skLineSegment(sketch, "E654", {"start": v(-24.83, 32.77) * mm, "end": v(-23.5, 33.75) * mm});
            skLineSegment(sketch, "E655", {"start": v(-23.5, 33.75) * mm, "end": v(-23.48, 33.8) * mm});
            skLineSegment(sketch, "E656", {"start": v(-23.48, 33.8) * mm, "end": v(-23.48, 33.86) * mm});
            skLineSegment(sketch, "E657", {"start": v(-23.48, 33.86) * mm, "end": v(-23.5, 33.96) * mm});
            skLineSegment(sketch, "E658", {"start": v(-23.5, 33.96) * mm, "end": v(-23.7, 34.58) * mm});
            skLineSegment(sketch, "E659", {"start": v(-23.7, 34.58) * mm, "end": v(-23.76, 34.68) * mm});
            skLineSegment(sketch, "E660", {"start": v(-23.76, 34.68) * mm, "end": v(-23.79, 34.75) * mm});
            skLineSegment(sketch, "E661", {"start": v(-23.79, 34.75) * mm, "end": v(-23.85, 34.97) * mm});
            skLineSegment(sketch, "E662", {"start": v(-23.85, 34.97) * mm, "end": v(-23.88, 35.03) * mm});
            skLineSegment(sketch, "E663", {"start": v(-23.88, 35.03) * mm, "end": v(-24, 35.42) * mm});
            skLineSegment(sketch, "E664", {"start": v(-24, 35.42) * mm, "end": v(-24.02, 35.48) * mm});
            skLineSegment(sketch, "E665", {"start": v(-24.02, 35.48) * mm, "end": v(-24.16, 36) * mm});
            skLineSegment(sketch, "E666", {"start": v(-24.16, 36) * mm, "end": v(-24.2, 36.19) * mm});
            skLineSegment(sketch, "E667", {"start": v(-24.2, 36.19) * mm, "end": v(-24.38, 37.05) * mm});
            skLineSegment(sketch, "E668", {"start": v(-24.38, 37.05) * mm, "end": v(-24.4, 37.52) * mm});
            skLineSegment(sketch, "E669", {"start": v(-24.4, 37.52) * mm, "end": v(-24.24, 37.72) * mm});
            skLineSegment(sketch, "E670", {"start": v(-24.24, 37.72) * mm, "end": v(-23.87, 37.97) * mm});
            skLineSegment(sketch, "E671", {"start": v(-23.87, 37.97) * mm, "end": v(-23.76, 38.03) * mm});
            skLineSegment(sketch, "E672", {"start": v(-23.76, 38.03) * mm, "end": v(-23.66, 38.1) * mm});
            skLineSegment(sketch, "E673", {"start": v(-23.66, 38.1) * mm, "end": v(-23.27, 38.32) * mm});
            skLineSegment(sketch, "E674", {"start": v(-23.27, 38.32) * mm, "end": v(-23.03, 38.37) * mm});
            skLineSegment(sketch, "E675", {"start": v(-23.03, 38.37) * mm, "end": v(-22.61, 38.15) * mm});
            skLineSegment(sketch, "E676", {"start": v(-22.61, 38.15) * mm, "end": v(-21.92, 37.62) * mm});
            skLineSegment(sketch, "E677", {"start": v(-21.92, 37.62) * mm, "end": v(-21.77, 37.5) * mm});
            skLineSegment(sketch, "E678", {"start": v(-21.77, 37.5) * mm, "end": v(-21.36, 37.14) * mm});
            skLineSegment(sketch, "E679", {"start": v(-21.36, 37.14) * mm, "end": v(-21.32, 37.1) * mm});
            skLineSegment(sketch, "E680", {"start": v(-21.32, 37.1) * mm, "end": v(-21.02, 36.82) * mm});
            skLineSegment(sketch, "E681", {"start": v(-21.02, 36.82) * mm, "end": v(-20.98, 36.76) * mm});
            skLineSegment(sketch, "E682", {"start": v(-20.98, 36.76) * mm, "end": v(-20.8, 36.61) * mm});
            skLineSegment(sketch, "E683", {"start": v(-20.8, 36.61) * mm, "end": v(-20.76, 36.56) * mm});
            skLineSegment(sketch, "E684", {"start": v(-20.76, 36.56) * mm, "end": v(-20.69, 36.46) * mm});
            skLineSegment(sketch, "E685", {"start": v(-20.69, 36.46) * mm, "end": v(-20.22, 36) * mm});
            skLineSegment(sketch, "E686", {"start": v(-20.22, 36) * mm, "end": v(-20.14, 35.95) * mm});
            skLineSegment(sketch, "E687", {"start": v(-20.14, 35.95) * mm, "end": v(-20.1, 35.93) * mm});
            skLineSegment(sketch, "E688", {"start": v(-20.1, 35.93) * mm, "end": v(-20.03, 35.91) * mm});
            skLineSegment(sketch, "E689", {"start": v(-20.03, 35.91) * mm, "end": v(-18.57, 36.69) * mm});
            skLineSegment(sketch, "E690", {"start": v(-18.57, 36.69) * mm, "end": v(-18.55, 36.75) * mm});
            skLineSegment(sketch, "E691", {"start": v(-18.55, 36.75) * mm, "end": v(-18.54, 36.8) * mm});
            skLineSegment(sketch, "E692", {"start": v(-18.54, 36.8) * mm, "end": v(-18.54, 36.9) * mm});
            skLineSegment(sketch, "E693", {"start": v(-18.54, 36.9) * mm, "end": v(-18.66, 37.54) * mm});
            skLineSegment(sketch, "E694", {"start": v(-18.66, 37.54) * mm, "end": v(-18.7, 37.65) * mm});
            skLineSegment(sketch, "E695", {"start": v(-18.7, 37.65) * mm, "end": v(-18.72, 37.72) * mm});
            skLineSegment(sketch, "E696", {"start": v(-18.72, 37.72) * mm, "end": v(-18.75, 37.95) * mm});
            skLineSegment(sketch, "E697", {"start": v(-18.75, 37.95) * mm, "end": v(-18.77, 38.02) * mm});
            skLineSegment(sketch, "E698", {"start": v(-18.77, 38.02) * mm, "end": v(-18.84, 38.42) * mm});
            skLineSegment(sketch, "E699", {"start": v(-18.84, 38.42) * mm, "end": v(-18.85, 38.47) * mm});
            skLineSegment(sketch, "E700", {"start": v(-18.85, 38.47) * mm, "end": v(-18.91, 39.02) * mm});
            skLineSegment(sketch, "E701", {"start": v(-18.91, 39.02) * mm, "end": v(-18.93, 39.2) * mm});
            skLineSegment(sketch, "E702", {"start": v(-18.93, 39.2) * mm, "end": v(-18.98, 40.08) * mm});
            skLineSegment(sketch, "E703", {"start": v(-18.98, 40.08) * mm, "end": v(-18.93, 40.55) * mm});
            skLineSegment(sketch, "E704", {"start": v(-18.93, 40.55) * mm, "end": v(-18.75, 40.72) * mm});
            skLineSegment(sketch, "E705", {"start": v(-18.75, 40.72) * mm, "end": v(-18.35, 40.92) * mm});
            skLineSegment(sketch, "E706", {"start": v(-18.35, 40.92) * mm, "end": v(-18.24, 40.97) * mm});
            skLineSegment(sketch, "E707", {"start": v(-18.24, 40.97) * mm, "end": v(-18.13, 41.02) * mm});
            skLineSegment(sketch, "E708", {"start": v(-18.13, 41.02) * mm, "end": v(-17.71, 41.19) * mm});
            skLineSegment(sketch, "E709", {"start": v(-17.71, 41.19) * mm, "end": v(-17.46, 41.2) * mm});
            skLineSegment(sketch, "E710", {"start": v(-17.46, 41.2) * mm, "end": v(-17.08, 40.93) * mm});
            skLineSegment(sketch, "E711", {"start": v(-17.08, 40.93) * mm, "end": v(-16.47, 40.3) * mm});
            skLineSegment(sketch, "E712", {"start": v(-16.47, 40.3) * mm, "end": v(-16.34, 40.16) * mm});
            skLineSegment(sketch, "E713", {"start": v(-16.34, 40.16) * mm, "end": v(-15.98, 39.75) * mm});
            skLineSegment(sketch, "E714", {"start": v(-15.98, 39.75) * mm, "end": v(-15.94, 39.7) * mm});
            skLineSegment(sketch, "E715", {"start": v(-15.94, 39.7) * mm, "end": v(-15.7, 39.4) * mm});
            skLineSegment(sketch, "E716", {"start": v(-15.7, 39.4) * mm, "end": v(-15.65, 39.33) * mm});
            skLineSegment(sketch, "E717", {"start": v(-15.65, 39.33) * mm, "end": v(-15.5, 39.15) * mm});
            skLineSegment(sketch, "E718", {"start": v(-15.5, 39.15) * mm, "end": v(-15.46, 39.1) * mm});
            skLineSegment(sketch, "E719", {"start": v(-15.46, 39.1) * mm, "end": v(-15.41, 38.98) * mm});
            skLineSegment(sketch, "E720", {"start": v(-15.41, 38.98) * mm, "end": v(-15.01, 38.47) * mm});
            skLineSegment(sketch, "E721", {"start": v(-15.01, 38.47) * mm, "end": v(-14.94, 38.4) * mm});
            skLineSegment(sketch, "E722", {"start": v(-14.94, 38.4) * mm, "end": v(-14.9, 38.37) * mm});
            skLineSegment(sketch, "E723", {"start": v(-14.9, 38.37) * mm, "end": v(-14.84, 38.35) * mm});
            skLineSegment(sketch, "E724", {"start": v(-14.84, 38.35) * mm, "end": v(-13.28, 38.92) * mm});
            skLineSegment(sketch, "E725", {"start": v(-13.28, 38.92) * mm, "end": v(-13.26, 38.97) * mm});
            skLineSegment(sketch, "E726", {"start": v(-13.26, 38.97) * mm, "end": v(-13.24, 39.02) * mm});
            skLineSegment(sketch, "E727", {"start": v(-13.24, 39.02) * mm, "end": v(-13.23, 39.12) * mm});
            skLineSegment(sketch, "E728", {"start": v(-13.23, 39.12) * mm, "end": v(-13.25, 39.77) * mm});
            skLineSegment(sketch, "E729", {"start": v(-13.25, 39.77) * mm, "end": v(-13.28, 39.89) * mm});
            skLineSegment(sketch, "E730", {"start": v(-13.28, 39.89) * mm, "end": v(-13.29, 39.96) * mm});
            skLineSegment(sketch, "E731", {"start": v(-13.29, 39.96) * mm, "end": v(-13.29, 40.19) * mm});
            skLineSegment(sketch, "E732", {"start": v(-13.29, 40.19) * mm, "end": v(-13.3, 40.26) * mm});
            skLineSegment(sketch, "E733", {"start": v(-13.3, 40.26) * mm, "end": v(-13.3, 40.67) * mm});
            skLineSegment(sketch, "E734", {"start": v(-13.3, 40.67) * mm, "end": v(-13.3, 40.72) * mm});
            skLineSegment(sketch, "E735", {"start": v(-13.3, 40.72) * mm, "end": v(-13.3, 41.27) * mm});
            skLineSegment(sketch, "E736", {"start": v(-13.3, 41.27) * mm, "end": v(-13.29, 41.46) * mm});
            skLineSegment(sketch, "E737", {"start": v(-13.29, 41.46) * mm, "end": v(-13.22, 42.33) * mm});
            skLineSegment(sketch, "E738", {"start": v(-13.22, 42.33) * mm, "end": v(-13.1, 42.79) * mm});
            skLineSegment(sketch, "E739", {"start": v(-13.1, 42.79) * mm, "end": v(-12.9, 42.94) * mm});
            skLineSegment(sketch, "E740", {"start": v(-12.9, 42.94) * mm, "end": v(-12.48, 43.07) * mm});
            skLineSegment(sketch, "E741", {"start": v(-12.48, 43.07) * mm, "end": v(-12.36, 43.1) * mm});
            skLineSegment(sketch, "E742", {"start": v(-12.36, 43.1) * mm, "end": v(-12.24, 43.14) * mm});
            skLineSegment(sketch, "E743", {"start": v(-12.24, 43.14) * mm, "end": v(-11.8, 43.25) * mm});
            skLineSegment(sketch, "E744", {"start": v(-11.8, 43.25) * mm, "end": v(-11.56, 43.23) * mm});
            skLineSegment(sketch, "E745", {"start": v(-11.56, 43.23) * mm, "end": v(-11.22, 42.9) * mm});
            skLineSegment(sketch, "E746", {"start": v(-11.22, 42.9) * mm, "end": v(-10.7, 42.2) * mm});
            skLineSegment(sketch, "E747", {"start": v(-10.7, 42.2) * mm, "end": v(-10.6, 42.05) * mm});
            skLineSegment(sketch, "E748", {"start": v(-10.6, 42.05) * mm, "end": v(-10.3, 41.59) * mm});
            skLineSegment(sketch, "E749", {"start": v(-10.3, 41.59) * mm, "end": v(-10.26, 41.54) * mm});
            skLineSegment(sketch, "E750", {"start": v(-10.26, 41.54) * mm, "end": v(-10.06, 41.2) * mm});
            skLineSegment(sketch, "E751", {"start": v(-10.06, 41.2) * mm, "end": v(-10.03, 41.12) * mm});
            skLineSegment(sketch, "E752", {"start": v(-10.03, 41.12) * mm, "end": v(-9.9, 40.93) * mm});
            skLineSegment(sketch, "E753", {"start": v(-9.9, 40.93) * mm, "end": v(-9.87, 40.87) * mm});
            skLineSegment(sketch, "E754", {"start": v(-9.87, 40.87) * mm, "end": v(-9.84, 40.75) * mm});
            skLineSegment(sketch, "E755", {"start": v(-9.84, 40.75) * mm, "end": v(-9.51, 40.19) * mm});
            skLineSegment(sketch, "E756", {"start": v(-9.51, 40.19) * mm, "end": v(-9.45, 40.1) * mm});
            skLineSegment(sketch, "E757", {"start": v(-9.45, 40.1) * mm, "end": v(-9.41, 40.07) * mm});
            skLineSegment(sketch, "E758", {"start": v(-9.41, 40.07) * mm, "end": v(-9.36, 40.04) * mm});
            skLineSegment(sketch, "E759", {"start": v(-9.36, 40.04) * mm, "end": v(-7.74, 40.39) * mm});
            skLineSegment(sketch, "E760", {"start": v(-7.74, 40.39) * mm, "end": v(-7.7, 40.44) * mm});
            skLineSegment(sketch, "E761", {"start": v(-7.7, 40.44) * mm, "end": v(-7.68, 40.48) * mm});
            skLineSegment(sketch, "E762", {"start": v(-7.68, 40.48) * mm, "end": v(-7.66, 40.58) * mm});
            skLineSegment(sketch, "E763", {"start": v(-7.66, 40.58) * mm, "end": v(-7.59, 41.23) * mm});
            skLineSegment(sketch, "E764", {"start": v(-7.59, 41.23) * mm, "end": v(-7.6, 41.35) * mm});
            skLineSegment(sketch, "E765", {"start": v(-7.6, 41.35) * mm, "end": v(-7.6, 41.42) * mm});
            skLineSegment(sketch, "E766", {"start": v(-7.6, 41.42) * mm, "end": v(-7.56, 41.65) * mm});
            skLineSegment(sketch, "E767", {"start": v(-7.56, 41.65) * mm, "end": v(-7.57, 41.72) * mm});
            skLineSegment(sketch, "E768", {"start": v(-7.57, 41.72) * mm, "end": v(-7.52, 42.12) * mm});
            skLineSegment(sketch, "E769", {"start": v(-7.52, 42.12) * mm, "end": v(-7.51, 42.18) * mm});
            skLineSegment(sketch, "E770", {"start": v(-7.51, 42.18) * mm, "end": v(-7.43, 42.72) * mm});
            skLineSegment(sketch, "E771", {"start": v(-7.43, 42.72) * mm, "end": v(-7.4, 42.9) * mm});
            skLineSegment(sketch, "E772", {"start": v(-7.4, 42.9) * mm, "end": v(-7.2, 43.76) * mm});
            skLineSegment(sketch, "E773", {"start": v(-7.2, 43.76) * mm, "end": v(-7.02, 44.2) * mm});
            skLineSegment(sketch, "E774", {"start": v(-7.02, 44.2) * mm, "end": v(-6.8, 44.31) * mm});
            skLineSegment(sketch, "E775", {"start": v(-6.8, 44.31) * mm, "end": v(-6.36, 44.4) * mm});
            skLineSegment(sketch, "E776", {"start": v(-6.36, 44.4) * mm, "end": v(-6.24, 44.4) * mm});
            skLineSegment(sketch, "E777", {"start": v(-6.24, 44.4) * mm, "end": v(-6.12, 44.43) * mm});
            skLineSegment(sketch, "E778", {"start": v(-6.12, 44.43) * mm, "end": v(-5.67, 44.47) * mm});
            skLineSegment(sketch, "E779", {"start": v(-5.67, 44.47) * mm, "end": v(-5.43, 44.42) * mm});
            skLineSegment(sketch, "E780", {"start": v(-5.43, 44.42) * mm, "end": v(-5.14, 44.05) * mm});
            skLineSegment(sketch, "E781", {"start": v(-5.14, 44.05) * mm, "end": v(-4.72, 43.28) * mm});
            skLineSegment(sketch, "E782", {"start": v(-4.72, 43.28) * mm, "end": v(-4.64, 43.11) * mm});
            skLineSegment(sketch, "E783", {"start": v(-4.64, 43.11) * mm, "end": v(-4.4, 42.61) * mm});
            skLineSegment(sketch, "E784", {"start": v(-4.4, 42.61) * mm, "end": v(-4.38, 42.56) * mm});
            skLineSegment(sketch, "E785", {"start": v(-4.38, 42.56) * mm, "end": v(-4.22, 42.19) * mm});
            skLineSegment(sketch, "E786", {"start": v(-4.22, 42.19) * mm, "end": v(-4.2, 42.12) * mm});
            skLineSegment(sketch, "E787", {"start": v(-4.2, 42.12) * mm, "end": v(-4.12, 41.91) * mm});
            skLineSegment(sketch, "E788", {"start": v(-4.12, 41.91) * mm, "end": v(-4.1, 41.84) * mm});
            skLineSegment(sketch, "E789", {"start": v(-4.1, 41.84) * mm, "end": v(-4.07, 41.72) * mm});
            skLineSegment(sketch, "E790", {"start": v(-4.07, 41.72) * mm, "end": v(-3.83, 41.12) * mm});
            skLineSegment(sketch, "E791", {"start": v(-3.83, 41.12) * mm, "end": v(-3.78, 41.03) * mm});
            skLineSegment(sketch, "E792", {"start": v(-3.78, 41.03) * mm, "end": v(-3.74, 41) * mm});
            skLineSegment(sketch, "E793", {"start": v(-3.74, 41) * mm, "end": v(-3.7, 40.95) * mm});
            skLineSegment(sketch, "E794", {"start": v(-3.7, 40.95) * mm, "end": v(-2.04, 41.07) * mm});
            skLineSegment(sketch, "E795", {"start": v(-2.04, 41.07) * mm, "end": v(-2, 41.12) * mm});
            skLineSegment(sketch, "E796", {"start": v(-2, 41.12) * mm, "end": v(-1.97, 41.16) * mm});
            skLineSegment(sketch, "E797", {"start": v(-1.97, 41.16) * mm, "end": v(-1.93, 41.25) * mm});
            skLineSegment(sketch, "E798", {"start": v(-1.93, 41.25) * mm, "end": v(-1.78, 41.88) * mm});
            skLineSegment(sketch, "E799", {"start": v(-1.78, 41.88) * mm, "end": v(-1.77, 42) * mm});
            skLineSegment(sketch, "E800", {"start": v(-1.77, 42) * mm, "end": v(-1.76, 42.08) * mm});
            skLineSegment(sketch, "E801", {"start": v(-1.76, 42.08) * mm, "end": v(-1.7, 42.3) * mm});
            skLineSegment(sketch, "E802", {"start": v(-1.7, 42.3) * mm, "end": v(-1.69, 42.37) * mm});
            skLineSegment(sketch, "E803", {"start": v(-1.69, 42.37) * mm, "end": v(-1.58, 42.76) * mm});
            skLineSegment(sketch, "E804", {"start": v(-1.58, 42.76) * mm, "end": v(-1.57, 42.81) * mm});
            skLineSegment(sketch, "E805", {"start": v(-1.57, 42.81) * mm, "end": v(-1.4, 43.34) * mm});
            skLineSegment(sketch, "E806", {"start": v(-1.4, 43.34) * mm, "end": v(-1.35, 43.51) * mm});
            skLineSegment(sketch, "E807", {"start": v(-1.35, 43.51) * mm, "end": v(-1.04, 44.34) * mm});
            skLineSegment(sketch, "E808", {"start": v(-1.04, 44.34) * mm, "end": v(-0.8, 44.74) * mm});
            skLineSegment(sketch, "E809", {"start": v(-0.8, 44.74) * mm, "end": v(-0.57, 44.83) * mm});
            skLineSegment(sketch, "E810", {"start": v(-0.57, 44.83) * mm, "end": v(-0.12, 44.85) * mm});
            skLineSegment(sketch, "E811", {"start": v(-0.12, 44.85) * mm, "end": v(0, 44.84) * mm});
            skLineSegment(sketch, "E812", {"start": v(0, 44.84) * mm, "end": v(0.12, 44.85) * mm});
            skLineSegment(sketch, "E813", {"start": v(0.12, 44.85) * mm, "end": v(0.57, 44.83) * mm});
            skLineSegment(sketch, "E814", {"start": v(0.57, 44.83) * mm, "end": v(0.8, 44.74) * mm});
            skLineSegment(sketch, "E815", {"start": v(0.8, 44.74) * mm, "end": v(1.04, 44.34) * mm});
            skLineSegment(sketch, "E816", {"start": v(1.04, 44.34) * mm, "end": v(1.35, 43.51) * mm});
            skLineSegment(sketch, "E817", {"start": v(1.35, 43.51) * mm, "end": v(1.4, 43.34) * mm});
            skLineSegment(sketch, "E818", {"start": v(1.4, 43.34) * mm, "end": v(1.57, 42.81) * mm});
            skLineSegment(sketch, "E819", {"start": v(1.57, 42.81) * mm, "end": v(1.58, 42.76) * mm});
            skLineSegment(sketch, "E820", {"start": v(1.58, 42.76) * mm, "end": v(1.69, 42.37) * mm});
            skLineSegment(sketch, "E821", {"start": v(1.69, 42.37) * mm, "end": v(1.7, 42.3) * mm});
            skLineSegment(sketch, "E822", {"start": v(1.7, 42.3) * mm, "end": v(1.76, 42.08) * mm});
            skLineSegment(sketch, "E823", {"start": v(1.76, 42.08) * mm, "end": v(1.77, 42) * mm});
            skLineSegment(sketch, "E824", {"start": v(1.77, 42) * mm, "end": v(1.78, 41.88) * mm});
            skLineSegment(sketch, "E825", {"start": v(1.78, 41.88) * mm, "end": v(1.93, 41.25) * mm});
            skLineSegment(sketch, "E826", {"start": v(1.93, 41.25) * mm, "end": v(1.97, 41.16) * mm});
            skLineSegment(sketch, "E827", {"start": v(1.97, 41.16) * mm, "end": v(2, 41.12) * mm});
            skLineSegment(sketch, "E828", {"start": v(2, 41.12) * mm, "end": v(2.04, 41.07) * mm});
            skLineSegment(sketch, "E829", {"start": v(2.04, 41.07) * mm, "end": v(3.7, 40.95) * mm});
            skLineSegment(sketch, "E830", {"start": v(3.7, 40.95) * mm, "end": v(3.74, 41) * mm});
            skLineSegment(sketch, "E831", {"start": v(3.74, 41) * mm, "end": v(3.78, 41.03) * mm});
            skLineSegment(sketch, "E832", {"start": v(3.78, 41.03) * mm, "end": v(3.83, 41.12) * mm});
            skLineSegment(sketch, "E833", {"start": v(3.83, 41.12) * mm, "end": v(4.07, 41.72) * mm});
            skLineSegment(sketch, "E834", {"start": v(4.07, 41.72) * mm, "end": v(4.1, 41.84) * mm});
            skLineSegment(sketch, "E835", {"start": v(4.1, 41.84) * mm, "end": v(4.12, 41.91) * mm});
            skLineSegment(sketch, "E836", {"start": v(4.12, 41.91) * mm, "end": v(4.2, 42.12) * mm});
            skLineSegment(sketch, "E837", {"start": v(4.2, 42.12) * mm, "end": v(4.22, 42.19) * mm});
            skLineSegment(sketch, "E838", {"start": v(4.22, 42.19) * mm, "end": v(4.38, 42.56) * mm});
            skLineSegment(sketch, "E839", {"start": v(4.38, 42.56) * mm, "end": v(4.4, 42.61) * mm});
            skLineSegment(sketch, "E840", {"start": v(4.4, 42.61) * mm, "end": v(4.64, 43.11) * mm});
            skLineSegment(sketch, "E841", {"start": v(4.64, 43.11) * mm, "end": v(4.72, 43.28) * mm});
            skLineSegment(sketch, "E842", {"start": v(4.72, 43.28) * mm, "end": v(5.14, 44.05) * mm});
            skLineSegment(sketch, "E843", {"start": v(5.14, 44.05) * mm, "end": v(5.43, 44.42) * mm});
            skLineSegment(sketch, "E844", {"start": v(5.43, 44.42) * mm, "end": v(5.67, 44.47) * mm});
            skLineSegment(sketch, "E845", {"start": v(5.67, 44.47) * mm, "end": v(6.12, 44.43) * mm});
            skLineSegment(sketch, "E846", {"start": v(6.12, 44.43) * mm, "end": v(6.24, 44.4) * mm});
            skLineSegment(sketch, "E847", {"start": v(6.24, 44.4) * mm, "end": v(6.36, 44.4) * mm});
            skLineSegment(sketch, "E848", {"start": v(6.36, 44.4) * mm, "end": v(6.8, 44.31) * mm});
            skLineSegment(sketch, "E849", {"start": v(6.8, 44.31) * mm, "end": v(7.02, 44.2) * mm});
            skLineSegment(sketch, "E850", {"start": v(7.02, 44.2) * mm, "end": v(7.2, 43.76) * mm});
            skLineSegment(sketch, "E851", {"start": v(7.2, 43.76) * mm, "end": v(7.4, 42.9) * mm});
            skLineSegment(sketch, "E852", {"start": v(7.4, 42.9) * mm, "end": v(7.43, 42.72) * mm});
            skLineSegment(sketch, "E853", {"start": v(7.43, 42.72) * mm, "end": v(7.51, 42.18) * mm});
            skLineSegment(sketch, "E854", {"start": v(7.51, 42.18) * mm, "end": v(7.52, 42.12) * mm});
            skLineSegment(sketch, "E855", {"start": v(7.52, 42.12) * mm, "end": v(7.57, 41.72) * mm});
            skLineSegment(sketch, "E856", {"start": v(7.57, 41.72) * mm, "end": v(7.56, 41.65) * mm});
            skLineSegment(sketch, "E857", {"start": v(7.56, 41.65) * mm, "end": v(7.6, 41.42) * mm});
            skLineSegment(sketch, "E858", {"start": v(7.6, 41.42) * mm, "end": v(7.6, 41.35) * mm});
            skLineSegment(sketch, "E859", {"start": v(7.6, 41.35) * mm, "end": v(7.59, 41.23) * mm});
            skLineSegment(sketch, "E860", {"start": v(7.59, 41.23) * mm, "end": v(7.66, 40.58) * mm});
            skLineSegment(sketch, "E861", {"start": v(7.66, 40.58) * mm, "end": v(7.68, 40.48) * mm});
            skLineSegment(sketch, "E862", {"start": v(7.68, 40.48) * mm, "end": v(7.7, 40.44) * mm});
            skLineSegment(sketch, "E863", {"start": v(7.7, 40.44) * mm, "end": v(7.74, 40.39) * mm});
            skLineSegment(sketch, "E864", {"start": v(7.74, 40.39) * mm, "end": v(9.36, 40.04) * mm});
            skLineSegment(sketch, "E865", {"start": v(9.36, 40.04) * mm, "end": v(9.41, 40.07) * mm});
            skLineSegment(sketch, "E866", {"start": v(9.41, 40.07) * mm, "end": v(9.45, 40.1) * mm});
            skLineSegment(sketch, "E867", {"start": v(9.45, 40.1) * mm, "end": v(9.51, 40.19) * mm});
            skLineSegment(sketch, "E868", {"start": v(9.51, 40.19) * mm, "end": v(9.84, 40.75) * mm});
            skLineSegment(sketch, "E869", {"start": v(9.84, 40.75) * mm, "end": v(9.87, 40.87) * mm});
            skLineSegment(sketch, "E870", {"start": v(9.87, 40.87) * mm, "end": v(9.9, 40.93) * mm});
            skLineSegment(sketch, "E871", {"start": v(9.9, 40.93) * mm, "end": v(10.03, 41.12) * mm});
            skLineSegment(sketch, "E872", {"start": v(10.03, 41.12) * mm, "end": v(10.06, 41.2) * mm});
            skLineSegment(sketch, "E873", {"start": v(10.06, 41.2) * mm, "end": v(10.26, 41.54) * mm});
            skLineSegment(sketch, "E874", {"start": v(10.26, 41.54) * mm, "end": v(10.3, 41.59) * mm});
            skLineSegment(sketch, "E875", {"start": v(10.3, 41.59) * mm, "end": v(10.6, 42.05) * mm});
            skLineSegment(sketch, "E876", {"start": v(10.6, 42.05) * mm, "end": v(10.7, 42.2) * mm});
            skLineSegment(sketch, "E877", {"start": v(10.7, 42.2) * mm, "end": v(11.22, 42.9) * mm});
            skLineSegment(sketch, "E878", {"start": v(11.22, 42.9) * mm, "end": v(11.56, 43.23) * mm});
            skLineSegment(sketch, "E879", {"start": v(11.56, 43.23) * mm, "end": v(11.8, 43.25) * mm});
            skLineSegment(sketch, "E880", {"start": v(11.8, 43.25) * mm, "end": v(12.24, 43.14) * mm});
            skLineSegment(sketch, "E881", {"start": v(12.24, 43.14) * mm, "end": v(12.36, 43.1) * mm});
            skLineSegment(sketch, "E882", {"start": v(12.36, 43.1) * mm, "end": v(12.48, 43.07) * mm});
            skLineSegment(sketch, "E883", {"start": v(12.48, 43.07) * mm, "end": v(12.9, 42.94) * mm});
            skLineSegment(sketch, "E884", {"start": v(12.9, 42.94) * mm, "end": v(13.1, 42.79) * mm});
            skLineSegment(sketch, "E885", {"start": v(13.1, 42.79) * mm, "end": v(13.22, 42.33) * mm});
            skLineSegment(sketch, "E886", {"start": v(13.22, 42.33) * mm, "end": v(13.29, 41.46) * mm});
            skLineSegment(sketch, "E887", {"start": v(13.29, 41.46) * mm, "end": v(13.3, 41.27) * mm});
            skLineSegment(sketch, "E888", {"start": v(13.3, 41.27) * mm, "end": v(13.3, 40.72) * mm});
            skLineSegment(sketch, "E889", {"start": v(13.3, 40.72) * mm, "end": v(13.3, 40.67) * mm});
            skLineSegment(sketch, "E890", {"start": v(13.3, 40.67) * mm, "end": v(13.3, 40.26) * mm});
            skLineSegment(sketch, "E891", {"start": v(13.3, 40.26) * mm, "end": v(13.29, 40.19) * mm});
            skLineSegment(sketch, "E892", {"start": v(13.29, 40.19) * mm, "end": v(13.29, 39.96) * mm});
            skLineSegment(sketch, "E893", {"start": v(13.29, 39.96) * mm, "end": v(13.28, 39.89) * mm});
            skLineSegment(sketch, "E894", {"start": v(13.28, 39.89) * mm, "end": v(13.25, 39.77) * mm});
            skLineSegment(sketch, "E895", {"start": v(13.25, 39.77) * mm, "end": v(13.23, 39.12) * mm});
            skLineSegment(sketch, "E896", {"start": v(13.23, 39.12) * mm, "end": v(13.24, 39.02) * mm});
            skLineSegment(sketch, "E897", {"start": v(13.24, 39.02) * mm, "end": v(13.26, 38.97) * mm});
            skLineSegment(sketch, "E898", {"start": v(13.26, 38.97) * mm, "end": v(13.28, 38.92) * mm});
            skLineSegment(sketch, "E899", {"start": v(13.28, 38.92) * mm, "end": v(14.84, 38.35) * mm});
            skLineSegment(sketch, "E900", {"start": v(14.84, 38.35) * mm, "end": v(14.9, 38.37) * mm});
            skLineSegment(sketch, "E901", {"start": v(14.9, 38.37) * mm, "end": v(14.94, 38.4) * mm});
            skLineSegment(sketch, "E902", {"start": v(14.94, 38.4) * mm, "end": v(15.01, 38.47) * mm});
            skLineSegment(sketch, "E903", {"start": v(15.01, 38.47) * mm, "end": v(15.41, 38.98) * mm});
            skLineSegment(sketch, "E904", {"start": v(15.41, 38.98) * mm, "end": v(15.46, 39.1) * mm});
            skLineSegment(sketch, "E905", {"start": v(15.46, 39.1) * mm, "end": v(15.5, 39.15) * mm});
            skLineSegment(sketch, "E906", {"start": v(15.5, 39.15) * mm, "end": v(15.65, 39.33) * mm});
            skLineSegment(sketch, "E907", {"start": v(15.65, 39.33) * mm, "end": v(15.7, 39.4) * mm});
            skLineSegment(sketch, "E908", {"start": v(15.7, 39.4) * mm, "end": v(15.94, 39.7) * mm});
            skLineSegment(sketch, "E909", {"start": v(15.94, 39.7) * mm, "end": v(15.98, 39.75) * mm});
            skLineSegment(sketch, "E910", {"start": v(15.98, 39.75) * mm, "end": v(16.34, 40.16) * mm});
            skLineSegment(sketch, "E911", {"start": v(16.34, 40.16) * mm, "end": v(16.47, 40.3) * mm});
            skLineSegment(sketch, "E912", {"start": v(16.47, 40.3) * mm, "end": v(17.08, 40.93) * mm});
            skLineSegment(sketch, "E913", {"start": v(17.08, 40.93) * mm, "end": v(17.46, 41.2) * mm});
            skLineSegment(sketch, "E914", {"start": v(17.46, 41.2) * mm, "end": v(17.71, 41.19) * mm});
            skLineSegment(sketch, "E915", {"start": v(17.71, 41.19) * mm, "end": v(18.13, 41.02) * mm});
            skLineSegment(sketch, "E916", {"start": v(18.13, 41.02) * mm, "end": v(18.24, 40.97) * mm});
            skLineSegment(sketch, "E917", {"start": v(18.24, 40.97) * mm, "end": v(18.35, 40.92) * mm});
            skLineSegment(sketch, "E918", {"start": v(18.35, 40.92) * mm, "end": v(18.75, 40.72) * mm});
            skLineSegment(sketch, "E919", {"start": v(18.75, 40.72) * mm, "end": v(18.93, 40.55) * mm});
            skLineSegment(sketch, "E920", {"start": v(18.93, 40.55) * mm, "end": v(18.98, 40.08) * mm});
            skLineSegment(sketch, "E921", {"start": v(18.98, 40.08) * mm, "end": v(18.93, 39.2) * mm});
            skLineSegment(sketch, "E922", {"start": v(18.93, 39.2) * mm, "end": v(18.91, 39.02) * mm});
            skLineSegment(sketch, "E923", {"start": v(18.91, 39.02) * mm, "end": v(18.85, 38.47) * mm});
            skLineSegment(sketch, "E924", {"start": v(18.85, 38.47) * mm, "end": v(18.84, 38.42) * mm});
            skLineSegment(sketch, "E925", {"start": v(18.84, 38.42) * mm, "end": v(18.77, 38.02) * mm});
            skLineSegment(sketch, "E926", {"start": v(18.77, 38.02) * mm, "end": v(18.75, 37.95) * mm});
            skLineSegment(sketch, "E927", {"start": v(18.75, 37.95) * mm, "end": v(18.72, 37.72) * mm});
            skLineSegment(sketch, "E928", {"start": v(18.72, 37.72) * mm, "end": v(18.7, 37.65) * mm});
            skLineSegment(sketch, "E929", {"start": v(18.7, 37.65) * mm, "end": v(18.66, 37.54) * mm});
            skLineSegment(sketch, "E930", {"start": v(18.66, 37.54) * mm, "end": v(18.54, 36.9) * mm});
            skLineSegment(sketch, "E931", {"start": v(18.54, 36.9) * mm, "end": v(18.54, 36.8) * mm});
            skLineSegment(sketch, "E932", {"start": v(18.54, 36.8) * mm, "end": v(18.55, 36.75) * mm});
            skLineSegment(sketch, "E933", {"start": v(18.55, 36.75) * mm, "end": v(18.57, 36.69) * mm});
            skLineSegment(sketch, "E934", {"start": v(18.57, 36.69) * mm, "end": v(20.03, 35.91) * mm});
            skLineSegment(sketch, "E935", {"start": v(20.03, 35.91) * mm, "end": v(20.1, 35.93) * mm});
            skLineSegment(sketch, "E936", {"start": v(20.1, 35.93) * mm, "end": v(20.14, 35.95) * mm});
            skLineSegment(sketch, "E937", {"start": v(20.14, 35.95) * mm, "end": v(20.22, 36) * mm});
            skLineSegment(sketch, "E938", {"start": v(20.22, 36) * mm, "end": v(20.69, 36.46) * mm});
            skLineSegment(sketch, "E939", {"start": v(20.69, 36.46) * mm, "end": v(20.76, 36.56) * mm});
            skLineSegment(sketch, "E940", {"start": v(20.76, 36.56) * mm, "end": v(20.8, 36.61) * mm});
            skLineSegment(sketch, "E941", {"start": v(20.8, 36.61) * mm, "end": v(20.98, 36.76) * mm});
            skLineSegment(sketch, "E942", {"start": v(20.98, 36.76) * mm, "end": v(21.02, 36.82) * mm});
            skLineSegment(sketch, "E943", {"start": v(21.02, 36.82) * mm, "end": v(21.32, 37.1) * mm});
            skLineSegment(sketch, "E944", {"start": v(21.32, 37.1) * mm, "end": v(21.36, 37.14) * mm});
            skLineSegment(sketch, "E945", {"start": v(21.36, 37.14) * mm, "end": v(21.77, 37.5) * mm});
            skLineSegment(sketch, "E946", {"start": v(21.77, 37.5) * mm, "end": v(21.92, 37.62) * mm});
            skLineSegment(sketch, "E947", {"start": v(21.92, 37.62) * mm, "end": v(22.61, 38.15) * mm});
            skLineSegment(sketch, "E948", {"start": v(22.61, 38.15) * mm, "end": v(23.03, 38.37) * mm});
            skLineSegment(sketch, "E949", {"start": v(23.03, 38.37) * mm, "end": v(23.27, 38.32) * mm});
            skLineSegment(sketch, "E950", {"start": v(23.27, 38.32) * mm, "end": v(23.66, 38.1) * mm});
            skLineSegment(sketch, "E951", {"start": v(23.66, 38.1) * mm, "end": v(23.76, 38.03) * mm});
            skLineSegment(sketch, "E952", {"start": v(23.76, 38.03) * mm, "end": v(23.87, 37.97) * mm});
            skLineSegment(sketch, "E953", {"start": v(23.87, 37.97) * mm, "end": v(24.24, 37.72) * mm});
            skLineSegment(sketch, "E954", {"start": v(24.24, 37.72) * mm, "end": v(24.4, 37.52) * mm});
            skLineSegment(sketch, "E955", {"start": v(24.4, 37.52) * mm, "end": v(24.38, 37.05) * mm});
            skLineSegment(sketch, "E956", {"start": v(24.38, 37.05) * mm, "end": v(24.2, 36.19) * mm});
            skLineSegment(sketch, "E957", {"start": v(24.2, 36.19) * mm, "end": v(24.16, 36) * mm});
            skLineSegment(sketch, "E958", {"start": v(24.16, 36) * mm, "end": v(24.02, 35.48) * mm});
            skLineSegment(sketch, "E959", {"start": v(24.02, 35.48) * mm, "end": v(24, 35.42) * mm});
            skLineSegment(sketch, "E960", {"start": v(24, 35.42) * mm, "end": v(23.88, 35.03) * mm});
            skLineSegment(sketch, "E961", {"start": v(23.88, 35.03) * mm, "end": v(23.85, 34.97) * mm});
            skLineSegment(sketch, "E962", {"start": v(23.85, 34.97) * mm, "end": v(23.79, 34.75) * mm});
            skLineSegment(sketch, "E963", {"start": v(23.79, 34.75) * mm, "end": v(23.76, 34.68) * mm});
            skLineSegment(sketch, "E964", {"start": v(23.76, 34.68) * mm, "end": v(23.7, 34.58) * mm});
            skLineSegment(sketch, "E965", {"start": v(23.7, 34.58) * mm, "end": v(23.5, 33.96) * mm});
            skLineSegment(sketch, "E966", {"start": v(23.5, 33.96) * mm, "end": v(23.48, 33.86) * mm});
            skLineSegment(sketch, "E967", {"start": v(23.48, 33.86) * mm, "end": v(23.48, 33.8) * mm});
            skLineSegment(sketch, "E968", {"start": v(23.48, 33.8) * mm, "end": v(23.5, 33.75) * mm});
            skLineSegment(sketch, "E969", {"start": v(23.5, 33.75) * mm, "end": v(24.83, 32.77) * mm});
            skLineSegment(sketch, "E970", {"start": v(24.83, 32.77) * mm, "end": v(24.9, 32.78) * mm});
            skLineSegment(sketch, "E971", {"start": v(24.9, 32.78) * mm, "end": v(24.95, 32.8) * mm});
            skLineSegment(sketch, "E972", {"start": v(24.95, 32.8) * mm, "end": v(25.04, 32.84) * mm});
            skLineSegment(sketch, "E973", {"start": v(25.04, 32.84) * mm, "end": v(25.56, 33.23) * mm});
            skLineSegment(sketch, "E974", {"start": v(25.56, 33.23) * mm, "end": v(25.64, 33.32) * mm});
            skLineSegment(sketch, "E975", {"start": v(25.64, 33.32) * mm, "end": v(25.7, 33.36) * mm});
            skLineSegment(sketch, "E976", {"start": v(25.7, 33.36) * mm, "end": v(25.89, 33.49) * mm});
            skLineSegment(sketch, "E977", {"start": v(25.89, 33.49) * mm, "end": v(25.94, 33.54) * mm});
            skLineSegment(sketch, "E978", {"start": v(25.94, 33.54) * mm, "end": v(26.27, 33.77) * mm});
            skLineSegment(sketch, "E979", {"start": v(26.27, 33.77) * mm, "end": v(26.32, 33.8) * mm});
            skLineSegment(sketch, "E980", {"start": v(26.32, 33.8) * mm, "end": v(26.78, 34.1) * mm});
            skLineSegment(sketch, "E981", {"start": v(26.78, 34.1) * mm, "end": v(26.94, 34.2) * mm});
            skLineSegment(sketch, "E982", {"start": v(26.94, 34.2) * mm, "end": v(27.7, 34.63) * mm});
            skLineSegment(sketch, "E983", {"start": v(27.7, 34.63) * mm, "end": v(28.14, 34.8) * mm});
            skLineSegment(sketch, "E984", {"start": v(28.14, 34.8) * mm, "end": v(28.38, 34.7) * mm});
            skLineSegment(sketch, "E985", {"start": v(28.38, 34.7) * mm, "end": v(28.73, 34.43) * mm});
            skLineSegment(sketch, "E986", {"start": v(28.73, 34.43) * mm, "end": v(28.82, 34.35) * mm});
            skLineSegment(sketch, "E987", {"start": v(28.82, 34.35) * mm, "end": v(28.92, 34.28) * mm});
            skLineSegment(sketch, "E988", {"start": v(28.92, 34.28) * mm, "end": v(29.25, 33.98) * mm});
            skLineSegment(sketch, "E989", {"start": v(29.25, 33.98) * mm, "end": v(29.38, 33.76) * mm});
            skLineSegment(sketch, "E990", {"start": v(29.38, 33.76) * mm, "end": v(29.3, 33.3) * mm});
            skLineSegment(sketch, "E991", {"start": v(29.3, 33.3) * mm, "end": v(29, 32.47) * mm});
            skLineSegment(sketch, "E992", {"start": v(29, 32.47) * mm, "end": v(28.94, 32.3) * mm});
            skLineSegment(sketch, "E993", {"start": v(28.94, 32.3) * mm, "end": v(28.72, 31.79) * mm});
            skLineSegment(sketch, "E994", {"start": v(28.72, 31.79) * mm, "end": v(28.7, 31.74) * mm});
            skLineSegment(sketch, "E995", {"start": v(28.7, 31.74) * mm, "end": v(28.53, 31.37) * mm});
            skLineSegment(sketch, "E996", {"start": v(28.53, 31.37) * mm, "end": v(28.48, 31.3) * mm});
            skLineSegment(sketch, "E997", {"start": v(28.48, 31.3) * mm, "end": v(28.4, 31.1) * mm});
            skLineSegment(sketch, "E998", {"start": v(28.4, 31.1) * mm, "end": v(28.36, 31.04) * mm});
            skLineSegment(sketch, "E999", {"start": v(28.36, 31.04) * mm, "end": v(28.28, 30.94) * mm});
            skLineSegment(sketch, "E1000", {"start": v(28.28, 30.94) * mm, "end": v(28, 30.36) * mm});
            skLineSegment(sketch, "E1001", {"start": v(28, 30.36) * mm, "end": v(27.96, 30.26) * mm});
            skLineSegment(sketch, "E1002", {"start": v(27.96, 30.26) * mm, "end": v(27.96, 30.21) * mm});
            skLineSegment(sketch, "E1003", {"start": v(27.96, 30.21) * mm, "end": v(27.96, 30.15) * mm});
            skLineSegment(sketch, "E1004", {"start": v(27.96, 30.15) * mm, "end": v(29.15, 29) * mm});
            skLineSegment(sketch, "E1005", {"start": v(29.15, 29) * mm, "end": v(29.22, 29) * mm});
            skLineSegment(sketch, "E1006", {"start": v(29.22, 29) * mm, "end": v(29.27, 29) * mm});
            skLineSegment(sketch, "E1007", {"start": v(29.27, 29) * mm, "end": v(29.36, 29.04) * mm});
            skLineSegment(sketch, "E1008", {"start": v(29.36, 29.04) * mm, "end": v(29.94, 29.35) * mm});
            skLineSegment(sketch, "E1009", {"start": v(29.94, 29.35) * mm, "end": v(30.03, 29.42) * mm});
            skLineSegment(sketch, "E1010", {"start": v(30.03, 29.42) * mm, "end": v(30.1, 29.46) * mm});
            skLineSegment(sketch, "E1011", {"start": v(30.1, 29.46) * mm, "end": v(30.3, 29.56) * mm});
            skLineSegment(sketch, "E1012", {"start": v(30.3, 29.56) * mm, "end": v(30.36, 29.6) * mm});
            skLineSegment(sketch, "E1013", {"start": v(30.36, 29.6) * mm, "end": v(30.72, 29.79) * mm});
            skLineSegment(sketch, "E1014", {"start": v(30.72, 29.79) * mm, "end": v(30.77, 29.81) * mm});
            skLineSegment(sketch, "E1015", {"start": v(30.77, 29.81) * mm, "end": v(31.26, 30.05) * mm});
            skLineSegment(sketch, "E1016", {"start": v(31.26, 30.05) * mm, "end": v(31.44, 30.12) * mm});
            skLineSegment(sketch, "E1017", {"start": v(31.44, 30.12) * mm, "end": v(32.25, 30.44) * mm});
            skLineSegment(sketch, "E1018", {"start": v(32.25, 30.44) * mm, "end": v(32.71, 30.54) * mm});
            skLineSegment(sketch, "E1019", {"start": v(32.71, 30.54) * mm, "end": v(32.93, 30.42) * mm});
            skLineSegment(sketch, "E1020", {"start": v(32.93, 30.42) * mm, "end": v(33.25, 30.1) * mm});
            skLineSegment(sketch, "E1021", {"start": v(33.25, 30.1) * mm, "end": v(33.32, 30) * mm});
            skLineSegment(sketch, "E1022", {"start": v(33.32, 30) * mm, "end": v(33.4, 29.92) * mm});
            skLineSegment(sketch, "E1023", {"start": v(33.4, 29.92) * mm, "end": v(33.7, 29.57) * mm});
            skLineSegment(sketch, "E1024", {"start": v(33.7, 29.57) * mm, "end": v(33.79, 29.34) * mm});
            skLineSegment(sketch, "E1025", {"start": v(33.79, 29.34) * mm, "end": v(33.65, 28.9) * mm});
            skLineSegment(sketch, "E1026", {"start": v(33.65, 28.9) * mm, "end": v(33.24, 28.12) * mm});
            skLineSegment(sketch, "E1027", {"start": v(33.24, 28.12) * mm, "end": v(33.15, 27.95) * mm});
            skLineSegment(sketch, "E1028", {"start": v(33.15, 27.95) * mm, "end": v(32.87, 27.48) * mm});
            skLineSegment(sketch, "E1029", {"start": v(32.87, 27.48) * mm, "end": v(32.84, 27.43) * mm});
            skLineSegment(sketch, "E1030", {"start": v(32.84, 27.43) * mm, "end": v(32.61, 27.1) * mm});
            skLineSegment(sketch, "E1031", {"start": v(32.61, 27.1) * mm, "end": v(32.56, 27.04) * mm});
            skLineSegment(sketch, "E1032", {"start": v(32.56, 27.04) * mm, "end": v(32.44, 26.85) * mm});
            skLineSegment(sketch, "E1033", {"start": v(32.44, 26.85) * mm, "end": v(32.4, 26.79) * mm});
            skLineSegment(sketch, "E1034", {"start": v(32.4, 26.79) * mm, "end": v(32.31, 26.7) * mm});
            skLineSegment(sketch, "E1035", {"start": v(32.31, 26.7) * mm, "end": v(31.95, 26.17) * mm});
            skLineSegment(sketch, "E1036", {"start": v(31.95, 26.17) * mm, "end": v(31.9, 26.08) * mm});
            skLineSegment(sketch, "E1037", {"start": v(31.9, 26.08) * mm, "end": v(31.9, 26.02) * mm});
            skLineSegment(sketch, "E1038", {"start": v(31.9, 26.02) * mm, "end": v(31.89, 25.96) * mm});
            skLineSegment(sketch, "E1039", {"start": v(31.89, 25.96) * mm, "end": v(32.9, 24.66) * mm});
            skLineSegment(sketch, "E1040", {"start": v(32.9, 24.66) * mm, "end": v(32.97, 24.65) * mm});
            skLineSegment(sketch, "E1041", {"start": v(32.97, 24.65) * mm, "end": v(33.02, 24.65) * mm});
            skLineSegment(sketch, "E1042", {"start": v(33.02, 24.65) * mm, "end": v(33.12, 24.67) * mm});
            skLineSegment(sketch, "E1043", {"start": v(33.12, 24.67) * mm, "end": v(33.73, 24.9) * mm});
            skLineSegment(sketch, "E1044", {"start": v(33.73, 24.9) * mm, "end": v(33.83, 24.96) * mm});
            skLineSegment(sketch, "E1045", {"start": v(33.83, 24.96) * mm, "end": v(33.9, 24.99) * mm});
            skLineSegment(sketch, "E1046", {"start": v(33.9, 24.99) * mm, "end": v(34.12, 25.05) * mm});
            skLineSegment(sketch, "E1047", {"start": v(34.12, 25.05) * mm, "end": v(34.18, 25.1) * mm});
            skLineSegment(sketch, "E1048", {"start": v(34.18, 25.1) * mm, "end": v(34.56, 25.22) * mm});
            skLineSegment(sketch, "E1049", {"start": v(34.56, 25.22) * mm, "end": v(34.62, 25.24) * mm});
            skLineSegment(sketch, "E1050", {"start": v(34.62, 25.24) * mm, "end": v(35.14, 25.4) * mm});
            skLineSegment(sketch, "E1051", {"start": v(35.14, 25.4) * mm, "end": v(35.32, 25.45) * mm});
            skLineSegment(sketch, "E1052", {"start": v(35.32, 25.45) * mm, "end": v(36.18, 25.66) * mm});
            skLineSegment(sketch, "E1053", {"start": v(36.18, 25.66) * mm, "end": v(36.64, 25.69) * mm});
            skLineSegment(sketch, "E1054", {"start": v(36.64, 25.69) * mm, "end": v(36.85, 25.54) * mm});
            skLineSegment(sketch, "E1055", {"start": v(36.85, 25.54) * mm, "end": v(37.11, 25.18) * mm});
            skLineSegment(sketch, "E1056", {"start": v(37.11, 25.18) * mm, "end": v(37.18, 25.08) * mm});
            skLineSegment(sketch, "E1057", {"start": v(37.18, 25.08) * mm, "end": v(37.25, 24.98) * mm});
            skLineSegment(sketch, "E1058", {"start": v(37.25, 24.98) * mm, "end": v(37.48, 24.6) * mm});
            skLineSegment(sketch, "E1059", {"start": v(37.48, 24.6) * mm, "end": v(37.54, 24.35) * mm});
            skLineSegment(sketch, "E1060", {"start": v(37.54, 24.35) * mm, "end": v(37.34, 23.93) * mm});
            skLineSegment(sketch, "E1061", {"start": v(37.34, 23.93) * mm, "end": v(36.83, 23.22) * mm});
            skLineSegment(sketch, "E1062", {"start": v(36.83, 23.22) * mm, "end": v(36.72, 23.07) * mm});
            skLineSegment(sketch, "E1063", {"start": v(36.72, 23.07) * mm, "end": v(36.37, 22.64) * mm});
            skLineSegment(sketch, "E1064", {"start": v(36.37, 22.64) * mm, "end": v(36.33, 22.6) * mm});
            skLineSegment(sketch, "E1065", {"start": v(36.33, 22.6) * mm, "end": v(36.07, 22.3) * mm});
            skLineSegment(sketch, "E1066", {"start": v(36.07, 22.3) * mm, "end": v(36.01, 22.25) * mm});
            skLineSegment(sketch, "E1067", {"start": v(36.01, 22.25) * mm, "end": v(35.87, 22.07) * mm});
            skLineSegment(sketch, "E1068", {"start": v(35.87, 22.07) * mm, "end": v(35.81, 22.02) * mm});
            skLineSegment(sketch, "E1069", {"start": v(35.81, 22.02) * mm, "end": v(35.72, 21.95) * mm});
            skLineSegment(sketch, "E1070", {"start": v(35.72, 21.95) * mm, "end": v(35.28, 21.47) * mm});
            skLineSegment(sketch, "E1071", {"start": v(35.28, 21.47) * mm, "end": v(35.22, 21.38) * mm});
            skLineSegment(sketch, "E1072", {"start": v(35.22, 21.38) * mm, "end": v(35.2, 21.33) * mm});
            skLineSegment(sketch, "E1073", {"start": v(35.2, 21.33) * mm, "end": v(35.2, 21.27) * mm});
            skLineSegment(sketch, "E1074", {"start": v(35.2, 21.27) * mm, "end": v(36.02, 19.84) * mm});
            skLineSegment(sketch, "E1075", {"start": v(36.02, 19.84) * mm, "end": v(36.08, 19.82) * mm});
            skLineSegment(sketch, "E1076", {"start": v(36.08, 19.82) * mm, "end": v(36.13, 19.81) * mm});
            skLineSegment(sketch, "E1077", {"start": v(36.13, 19.81) * mm, "end": v(36.23, 19.82) * mm});
            skLineSegment(sketch, "E1078", {"start": v(36.23, 19.82) * mm, "end": v(36.86, 19.96) * mm});
            skLineSegment(sketch, "E1079", {"start": v(36.86, 19.96) * mm, "end": v(36.98, 20) * mm});
            skLineSegment(sketch, "E1080", {"start": v(36.98, 20) * mm, "end": v(37.05, 20.02) * mm});
            skLineSegment(sketch, "E1081", {"start": v(37.05, 20.02) * mm, "end": v(37.27, 20.06) * mm});
            skLineSegment(sketch, "E1082", {"start": v(37.27, 20.06) * mm, "end": v(37.34, 20.09) * mm});
            skLineSegment(sketch, "E1083", {"start": v(37.34, 20.09) * mm, "end": v(37.74, 20.17) * mm});
            skLineSegment(sketch, "E1084", {"start": v(37.74, 20.17) * mm, "end": v(37.8, 20.18) * mm});
            skLineSegment(sketch, "E1085", {"start": v(37.8, 20.18) * mm, "end": v(38.33, 20.26) * mm});
            skLineSegment(sketch, "E1086", {"start": v(38.33, 20.26) * mm, "end": v(38.52, 20.29) * mm});
            skLineSegment(sketch, "E1087", {"start": v(38.52, 20.29) * mm, "end": v(39.4, 20.37) * mm});
            skLineSegment(sketch, "E1088", {"start": v(39.4, 20.37) * mm, "end": v(39.86, 20.34) * mm});
            skLineSegment(sketch, "E1089", {"start": v(39.86, 20.34) * mm, "end": v(40.04, 20.16) * mm});
            skLineSegment(sketch, "E1090", {"start": v(40.04, 20.16) * mm, "end": v(40.25, 19.77) * mm});
            skLineSegment(sketch, "E1091", {"start": v(40.25, 19.77) * mm, "end": v(40.3, 19.66) * mm});
            skLineSegment(sketch, "E1092", {"start": v(40.3, 19.66) * mm, "end": v(40.36, 19.55) * mm});
            skLineSegment(sketch, "E1093", {"start": v(40.36, 19.55) * mm, "end": v(40.54, 19.14) * mm});
            skLineSegment(sketch, "E1094", {"start": v(40.54, 19.14) * mm, "end": v(40.57, 18.89) * mm});
            skLineSegment(sketch, "E1095", {"start": v(40.57, 18.89) * mm, "end": v(40.3, 18.5) * mm});
            skLineSegment(sketch, "E1096", {"start": v(40.3, 18.5) * mm, "end": v(39.7, 17.86) * mm});
            skLineSegment(sketch, "E1097", {"start": v(39.7, 17.86) * mm, "end": v(39.57, 17.73) * mm});
            skLineSegment(sketch, "E1098", {"start": v(39.57, 17.73) * mm, "end": v(39.17, 17.36) * mm});
            skLineSegment(sketch, "E1099", {"start": v(39.17, 17.36) * mm, "end": v(39.13, 17.32) * mm});
            skLineSegment(sketch, "E1100", {"start": v(39.13, 17.32) * mm, "end": v(38.82, 17.06) * mm});
            skLineSegment(sketch, "E1101", {"start": v(38.82, 17.06) * mm, "end": v(38.76, 17.02) * mm});
            skLineSegment(sketch, "E1102", {"start": v(38.76, 17.02) * mm, "end": v(38.59, 16.87) * mm});
            skLineSegment(sketch, "E1103", {"start": v(38.59, 16.87) * mm, "end": v(38.53, 16.82) * mm});
            skLineSegment(sketch, "E1104", {"start": v(38.53, 16.82) * mm, "end": v(38.42, 16.76) * mm});
            skLineSegment(sketch, "E1105", {"start": v(38.42, 16.76) * mm, "end": v(37.93, 16.35) * mm});
            skLineSegment(sketch, "E1106", {"start": v(37.93, 16.35) * mm, "end": v(37.86, 16.27) * mm});
            skLineSegment(sketch, "E1107", {"start": v(37.86, 16.27) * mm, "end": v(37.83, 16.23) * mm});
            skLineSegment(sketch, "E1108", {"start": v(37.83, 16.23) * mm, "end": v(37.8, 16.17) * mm});
            skLineSegment(sketch, "E1109", {"start": v(37.8, 16.17) * mm, "end": v(38.43, 14.63) * mm});
            skLineSegment(sketch, "E1110", {"start": v(38.43, 14.63) * mm, "end": v(38.48, 14.6) * mm});
            skLineSegment(sketch, "E1111", {"start": v(38.48, 14.6) * mm, "end": v(38.53, 14.6) * mm});
            skLineSegment(sketch, "E1112", {"start": v(38.53, 14.6) * mm, "end": v(38.64, 14.59) * mm});
            skLineSegment(sketch, "E1113", {"start": v(38.64, 14.59) * mm, "end": v(39.28, 14.63) * mm});
            skLineSegment(sketch, "E1114", {"start": v(39.28, 14.63) * mm, "end": v(39.4, 14.67) * mm});
            skLineSegment(sketch, "E1115", {"start": v(39.4, 14.67) * mm, "end": v(39.47, 14.67) * mm});
            skLineSegment(sketch, "E1116", {"start": v(39.47, 14.67) * mm, "end": v(39.7, 14.68) * mm});
            skLineSegment(sketch, "E1117", {"start": v(39.7, 14.68) * mm, "end": v(39.77, 14.7) * mm});
            skLineSegment(sketch, "E1118", {"start": v(39.77, 14.7) * mm, "end": v(40.18, 14.72) * mm});
            skLineSegment(sketch, "E1119", {"start": v(40.18, 14.72) * mm, "end": v(40.23, 14.72) * mm});
            skLineSegment(sketch, "E1120", {"start": v(40.23, 14.72) * mm, "end": v(40.78, 14.73) * mm});
            skLineSegment(sketch, "E1121", {"start": v(40.78, 14.73) * mm, "end": v(40.97, 14.73) * mm});
            skLineSegment(sketch, "E1122", {"start": v(40.97, 14.73) * mm, "end": v(41.85, 14.7) * mm});
            skLineSegment(sketch, "E1123", {"start": v(41.85, 14.7) * mm, "end": v(42.3, 14.6) * mm});
            skLineSegment(sketch, "E1124", {"start": v(42.3, 14.6) * mm, "end": v(42.46, 14.4) * mm});
            skLineSegment(sketch, "E1125", {"start": v(42.46, 14.4) * mm, "end": v(42.61, 13.97) * mm});
            skLineSegment(sketch, "E1126", {"start": v(42.61, 13.97) * mm, "end": v(42.65, 13.86) * mm});
            skLineSegment(sketch, "E1127", {"start": v(42.65, 13.86) * mm, "end": v(42.69, 13.74) * mm});
            skLineSegment(sketch, "E1128", {"start": v(42.69, 13.74) * mm, "end": v(42.81, 13.31) * mm});
            skLineSegment(sketch, "E1129", {"start": v(42.81, 13.31) * mm, "end": v(42.8, 13.06) * mm});
            skLineSegment(sketch, "E1130", {"start": v(42.8, 13.06) * mm, "end": v(42.5, 12.71) * mm});
            skLineSegment(sketch, "E1131", {"start": v(42.5, 12.71) * mm, "end": v(41.8, 12.17) * mm});
            skLineSegment(sketch, "E1132", {"start": v(41.8, 12.17) * mm, "end": v(41.65, 12.05) * mm});
            skLineSegment(sketch, "E1133", {"start": v(41.65, 12.05) * mm, "end": v(41.2, 11.74) * mm});
            skLineSegment(sketch, "E1134", {"start": v(41.2, 11.74) * mm, "end": v(41.15, 11.7) * mm});
            skLineSegment(sketch, "E1135", {"start": v(41.15, 11.7) * mm, "end": v(40.81, 11.49) * mm});
            skLineSegment(sketch, "E1136", {"start": v(40.81, 11.49) * mm, "end": v(40.75, 11.46) * mm});
            skLineSegment(sketch, "E1137", {"start": v(40.75, 11.46) * mm, "end": v(40.56, 11.33) * mm});
            skLineSegment(sketch, "E1138", {"start": v(40.56, 11.33) * mm, "end": v(40.5, 11.3) * mm});
            skLineSegment(sketch, "E1139", {"start": v(40.5, 11.3) * mm, "end": v(40.38, 11.25) * mm});
            skLineSegment(sketch, "E1140", {"start": v(40.38, 11.25) * mm, "end": v(39.83, 10.9) * mm});
            skLineSegment(sketch, "E1141", {"start": v(39.83, 10.9) * mm, "end": v(39.75, 10.84) * mm});
            skLineSegment(sketch, "E1142", {"start": v(39.75, 10.84) * mm, "end": v(39.72, 10.8) * mm});
            skLineSegment(sketch, "E1143", {"start": v(39.72, 10.8) * mm, "end": v(39.7, 10.75) * mm});
            skLineSegment(sketch, "E1144", {"start": v(39.7, 10.75) * mm, "end": v(40.1, 9.14) * mm});
            skLineSegment(sketch, "E1145", {"start": v(40.1, 9.14) * mm, "end": v(40.14, 9.1) * mm});
            skLineSegment(sketch, "E1146", {"start": v(40.14, 9.1) * mm, "end": v(40.19, 9.09) * mm});
            skLineSegment(sketch, "E1147", {"start": v(40.19, 9.09) * mm, "end": v(40.3, 9.07) * mm});
            skLineSegment(sketch, "E1148", {"start": v(40.3, 9.07) * mm, "end": v(40.94, 9.02) * mm});
            skLineSegment(sketch, "E1149", {"start": v(40.94, 9.02) * mm, "end": v(41.06, 9.04) * mm});
            skLineSegment(sketch, "E1150", {"start": v(41.06, 9.04) * mm, "end": v(41.13, 9.04) * mm});
            skLineSegment(sketch, "E1151", {"start": v(41.13, 9.04) * mm, "end": v(41.36, 9.01) * mm});
            skLineSegment(sketch, "E1152", {"start": v(41.36, 9.01) * mm, "end": v(41.43, 9.02) * mm});
            skLineSegment(sketch, "E1153", {"start": v(41.43, 9.02) * mm, "end": v(41.83, 8.98) * mm});
            skLineSegment(sketch, "E1154", {"start": v(41.83, 8.98) * mm, "end": v(41.89, 8.98) * mm});
            skLineSegment(sketch, "E1155", {"start": v(41.89, 8.98) * mm, "end": v(42.43, 8.91) * mm});
            skLineSegment(sketch, "E1156", {"start": v(42.43, 8.91) * mm, "end": v(42.62, 8.88) * mm});
            skLineSegment(sketch, "E1157", {"start": v(42.62, 8.88) * mm, "end": v(43.48, 8.72) * mm});
            skLineSegment(sketch, "E1158", {"start": v(43.48, 8.72) * mm, "end": v(43.92, 8.56) * mm});
            skLineSegment(sketch, "E1159", {"start": v(43.92, 8.56) * mm, "end": v(44.05, 8.35) * mm});
            skLineSegment(sketch, "E1160", {"start": v(44.05, 8.35) * mm, "end": v(44.14, 7.9) * mm});
            skLineSegment(sketch, "E1161", {"start": v(44.14, 7.9) * mm, "end": v(44.16, 7.79) * mm});
            skLineSegment(sketch, "E1162", {"start": v(44.16, 7.79) * mm, "end": v(44.19, 7.67) * mm});
            skLineSegment(sketch, "E1163", {"start": v(44.19, 7.67) * mm, "end": v(44.25, 7.22) * mm});
            skLineSegment(sketch, "E1164", {"start": v(44.25, 7.22) * mm, "end": v(44.2, 6.98) * mm});
            skLineSegment(sketch, "E1165", {"start": v(44.2, 6.98) * mm, "end": v(43.85, 6.68) * mm});
            skLineSegment(sketch, "E1166", {"start": v(43.85, 6.68) * mm, "end": v(43.09, 6.23) * mm});
            skLineSegment(sketch, "E1167", {"start": v(43.09, 6.23) * mm, "end": v(42.92, 6.14) * mm});
            skLineSegment(sketch, "E1168", {"start": v(42.92, 6.14) * mm, "end": v(42.43, 5.89) * mm});
            skLineSegment(sketch, "E1169", {"start": v(42.43, 5.89) * mm, "end": v(42.38, 5.86) * mm});
            skLineSegment(sketch, "E1170", {"start": v(42.38, 5.86) * mm, "end": v(42.02, 5.7) * mm});
            skLineSegment(sketch, "E1171", {"start": v(42.02, 5.7) * mm, "end": v(41.94, 5.68) * mm});
            skLineSegment(sketch, "E1172", {"start": v(41.94, 5.68) * mm, "end": v(41.74, 5.58) * mm});
            skLineSegment(sketch, "E1173", {"start": v(41.74, 5.58) * mm, "end": v(41.67, 5.55) * mm});
            skLineSegment(sketch, "E1174", {"start": v(41.67, 5.55) * mm, "end": v(41.56, 5.52) * mm});
            skLineSegment(sketch, "E1175", {"start": v(41.56, 5.52) * mm, "end": v(40.96, 5.26) * mm});
            skLineSegment(sketch, "E1176", {"start": v(40.96, 5.26) * mm, "end": v(40.87, 5.2) * mm});
            skLineSegment(sketch, "E1177", {"start": v(40.87, 5.2) * mm, "end": v(40.84, 5.17) * mm});
            skLineSegment(sketch, "E1178", {"start": v(40.84, 5.17) * mm, "end": v(40.8, 5.12) * mm});
            skLineSegment(sketch, "E1179", {"start": v(40.8, 5.12) * mm, "end": v(40.97, 3.48) * mm});
            skLineSegment(sketch, "E1180", {"start": v(40.97, 3.48) * mm, "end": v(41.02, 3.43) * mm});
            skLineSegment(sketch, "E1181", {"start": v(41.02, 3.43) * mm, "end": v(41.06, 3.4) * mm});
            skLineSegment(sketch, "E1182", {"start": v(41.06, 3.4) * mm, "end": v(41.16, 3.37) * mm});
            skLineSegment(sketch, "E1183", {"start": v(41.16, 3.37) * mm, "end": v(41.8, 3.24) * mm});
            skLineSegment(sketch, "E1184", {"start": v(41.8, 3.24) * mm, "end": v(41.92, 3.24) * mm});
            skLineSegment(sketch, "E1185", {"start": v(41.92, 3.24) * mm, "end": v(41.99, 3.22) * mm});
            skLineSegment(sketch, "E1186", {"start": v(41.99, 3.22) * mm, "end": v(42.2, 3.17) * mm});
            skLineSegment(sketch, "E1187", {"start": v(42.2, 3.17) * mm, "end": v(42.28, 3.17) * mm});
            skLineSegment(sketch, "E1188", {"start": v(42.28, 3.17) * mm, "end": v(42.68, 3.08) * mm});
            skLineSegment(sketch, "E1189", {"start": v(42.68, 3.08) * mm, "end": v(42.73, 3.06) * mm});
            skLineSegment(sketch, "E1190", {"start": v(42.73, 3.06) * mm, "end": v(43.26, 2.92) * mm});
            skLineSegment(sketch, "E1191", {"start": v(43.26, 2.92) * mm, "end": v(43.44, 2.87) * mm});
            skLineSegment(sketch, "E1192", {"start": v(43.44, 2.87) * mm, "end": v(44.28, 2.59) * mm});
            skLineSegment(sketch, "E1193", {"start": v(44.28, 2.59) * mm, "end": v(44.69, 2.37) * mm});
            skLineSegment(sketch, "E1194", {"start": v(44.69, 2.37) * mm, "end": v(44.78, 2.13) * mm});
            skLineSegment(sketch, "E1195", {"start": v(44.78, 2.13) * mm, "end": v(44.81, 1.69) * mm});
            skLineSegment(sketch, "E1196", {"start": v(44.81, 1.69) * mm, "end": v(44.82, 1.56) * mm});
            skLineSegment(sketch, "E1197", {"start": v(44.82, 1.56) * mm, "end": v(44.82, 1.44) * mm});
            skLineSegment(sketch, "E1198", {"start": v(44.82, 1.44) * mm, "end": v(44.82, 1) * mm});
            skLineSegment(sketch, "E1199", {"start": v(44.82, 1) * mm, "end": v(44.74, 0.76) * mm});
            skLineSegment(sketch, "E1200", {"start": v(44.74, 0.76) * mm, "end": v(44.35, 0.5) * mm});
            skLineSegment(sketch, "E1201", {"start": v(44.35, 0.5) * mm, "end": v(43.53, 0.17) * mm});
            skLineSegment(sketch, "E1202", {"start": v(43.53, 0.17) * mm, "end": v(43.36, 0.1) * mm});
            skLineSegment(sketch, "E1203", {"start": v(43.36, 0.1) * mm, "end": v(42.84, -0.07) * mm});
            skLineSegment(sketch, "E1204", {"start": v(42.84, -0.07) * mm, "end": v(42.79, -0.1) * mm});
            skLineSegment(sketch, "E1205", {"start": v(42.79, -0.1) * mm, "end": v(42.4, -0.2) * mm});
            skLineSegment(sketch, "E1206", {"start": v(42.4, -0.2) * mm, "end": v(42.33, -0.22) * mm});
            skLineSegment(sketch, "E1207", {"start": v(42.33, -0.22) * mm, "end": v(42.11, -0.29) * mm});
            skLineSegment(sketch, "E1208", {"start": v(42.11, -0.29) * mm, "end": v(42.04, -0.3) * mm});
            skLineSegment(sketch, "E1209", {"start": v(42.04, -0.3) * mm, "end": v(41.92, -0.31) * mm});
            skLineSegment(sketch, "E1210", {"start": v(41.92, -0.31) * mm, "end": v(41.3, -0.5) * mm});
            skLineSegment(sketch, "E1211", {"start": v(41.3, -0.5) * mm, "end": v(41.2, -0.53) * mm});
            skLineSegment(sketch, "E1212", {"start": v(41.2, -0.53) * mm, "end": v(41.16, -0.56) * mm});
            skLineSegment(sketch, "E1213", {"start": v(41.16, -0.56) * mm, "end": v(41.12, -0.6) * mm});
            skLineSegment(sketch, "E1214", {"start": v(41.12, -0.6) * mm, "end": v(41.06, -2.26) * mm});
            skLineSegment(sketch, "E1215", {"start": v(41.06, -2.26) * mm, "end": v(41.1, -2.3) * mm});
            skLineSegment(sketch, "E1216", {"start": v(41.1, -2.3) * mm, "end": v(41.14, -2.34) * mm});
            skLineSegment(sketch, "E1217", {"start": v(41.14, -2.34) * mm, "end": v(41.23, -2.4) * mm});
            skLineSegment(sketch, "E1218", {"start": v(41.23, -2.4) * mm, "end": v(41.84, -2.61) * mm});
            skLineSegment(sketch, "E1219", {"start": v(41.84, -2.61) * mm, "end": v(41.96, -2.63) * mm});
            skLineSegment(sketch, "E1220", {"start": v(41.96, -2.63) * mm, "end": v(42.03, -2.65) * mm});
            skLineSegment(sketch, "E1221", {"start": v(42.03, -2.65) * mm, "end": v(42.24, -2.74) * mm});
            skLineSegment(sketch, "E1222", {"start": v(42.24, -2.74) * mm, "end": v(42.31, -2.75) * mm});
            skLineSegment(sketch, "E1223", {"start": v(42.31, -2.75) * mm, "end": v(42.69, -2.9) * mm});
            skLineSegment(sketch, "E1224", {"start": v(42.69, -2.9) * mm, "end": v(42.74, -2.91) * mm});
            skLineSegment(sketch, "E1225", {"start": v(42.74, -2.91) * mm, "end": v(43.25, -3.13) * mm});
            skLineSegment(sketch, "E1226", {"start": v(43.25, -3.13) * mm, "end": v(43.42, -3.2) * mm});
            skLineSegment(sketch, "E1227", {"start": v(43.42, -3.2) * mm, "end": v(44.2, -3.6) * mm});
            skLineSegment(sketch, "E1228", {"start": v(44.2, -3.6) * mm, "end": v(44.58, -3.88) * mm});
            skLineSegment(sketch, "E1229", {"start": v(44.58, -3.88) * mm, "end": v(44.64, -4.12) * mm});
            skLineSegment(sketch, "E1230", {"start": v(44.64, -4.12) * mm, "end": v(44.61, -4.57) * mm});
            skLineSegment(sketch, "E1231", {"start": v(44.61, -4.57) * mm, "end": v(44.6, -4.69) * mm});
            skLineSegment(sketch, "E1232", {"start": v(44.6, -4.69) * mm, "end": v(44.59, -4.8) * mm});
            skLineSegment(sketch, "E1233", {"start": v(44.59, -4.8) * mm, "end": v(44.52, -5.25) * mm});
            skLineSegment(sketch, "E1234", {"start": v(44.52, -5.25) * mm, "end": v(44.41, -5.48) * mm});
            skLineSegment(sketch, "E1235", {"start": v(44.41, -5.48) * mm, "end": v(43.99, -5.67) * mm});
            skLineSegment(sketch, "E1236", {"start": v(43.99, -5.67) * mm, "end": v(43.13, -5.89) * mm});
            skLineSegment(sketch, "E1237", {"start": v(43.13, -5.89) * mm, "end": v(42.95, -5.93) * mm});
            skLineSegment(sketch, "E1238", {"start": v(42.95, -5.93) * mm, "end": v(42.41, -6.04) * mm});
            skLineSegment(sketch, "E1239", {"start": v(42.41, -6.04) * mm, "end": v(42.36, -6.04) * mm});
            skLineSegment(sketch, "E1240", {"start": v(42.36, -6.04) * mm, "end": v(41.96, -6.1) * mm});
            skLineSegment(sketch, "E1241", {"start": v(41.96, -6.1) * mm, "end": v(41.88, -6.1) * mm});
            skLineSegment(sketch, "E1242", {"start": v(41.88, -6.1) * mm, "end": v(41.66, -6.15) * mm});
            skLineSegment(sketch, "E1243", {"start": v(41.66, -6.15) * mm, "end": v(41.59, -6.15) * mm});
            skLineSegment(sketch, "E1244", {"start": v(41.59, -6.15) * mm, "end": v(41.47, -6.15) * mm});
            skLineSegment(sketch, "E1245", {"start": v(41.47, -6.15) * mm, "end": v(40.83, -6.23) * mm});
            skLineSegment(sketch, "E1246", {"start": v(40.83, -6.23) * mm, "end": v(40.73, -6.26) * mm});
            skLineSegment(sketch, "E1247", {"start": v(40.73, -6.26) * mm, "end": v(40.68, -6.29) * mm});
            skLineSegment(sketch, "E1248", {"start": v(40.68, -6.29) * mm, "end": v(40.63, -6.32) * mm});
            skLineSegment(sketch, "E1249", {"start": v(40.63, -6.32) * mm, "end": v(40.34, -7.95) * mm});
            skLineSegment(sketch, "E1250", {"start": v(40.34, -7.95) * mm, "end": v(40.38, -8) * mm});
            skLineSegment(sketch, "E1251", {"start": v(40.38, -8) * mm, "end": v(40.41, -8.05) * mm});
            skLineSegment(sketch, "E1252", {"start": v(40.41, -8.05) * mm, "end": v(40.5, -8.1) * mm});
            skLineSegment(sketch, "E1253", {"start": v(40.5, -8.1) * mm, "end": v(41.07, -8.4) * mm});
            skLineSegment(sketch, "E1254", {"start": v(41.07, -8.4) * mm, "end": v(41.19, -8.44) * mm});
            skLineSegment(sketch, "E1255", {"start": v(41.19, -8.44) * mm, "end": v(41.25, -8.47) * mm});
            skLineSegment(sketch, "E1256", {"start": v(41.25, -8.47) * mm, "end": v(41.45, -8.59) * mm});
            skLineSegment(sketch, "E1257", {"start": v(41.45, -8.59) * mm, "end": v(41.52, -8.61) * mm});
            skLineSegment(sketch, "E1258", {"start": v(41.52, -8.61) * mm, "end": v(41.87, -8.8) * mm});
            skLineSegment(sketch, "E1259", {"start": v(41.87, -8.8) * mm, "end": v(41.92, -8.83) * mm});
            skLineSegment(sketch, "E1260", {"start": v(41.92, -8.83) * mm, "end": v(42.4, -9.12) * mm});
            skLineSegment(sketch, "E1261", {"start": v(42.4, -9.12) * mm, "end": v(42.55, -9.22) * mm});
            skLineSegment(sketch, "E1262", {"start": v(42.55, -9.22) * mm, "end": v(43.27, -9.72) * mm});
            skLineSegment(sketch, "E1263", {"start": v(43.27, -9.72) * mm, "end": v(43.6, -10.04) * mm});
            skLineSegment(sketch, "E1264", {"start": v(43.6, -10.04) * mm, "end": v(43.64, -10.3) * mm});
            skLineSegment(sketch, "E1265", {"start": v(43.64, -10.3) * mm, "end": v(43.54, -10.73) * mm});
            skLineSegment(sketch, "E1266", {"start": v(43.54, -10.73) * mm, "end": v(43.51, -10.85) * mm});
            skLineSegment(sketch, "E1267", {"start": v(43.51, -10.85) * mm, "end": v(43.48, -10.97) * mm});
            skLineSegment(sketch, "E1268", {"start": v(43.48, -10.97) * mm, "end": v(43.36, -11.4) * mm});
            skLineSegment(sketch, "E1269", {"start": v(43.36, -11.4) * mm, "end": v(43.22, -11.6) * mm});
            skLineSegment(sketch, "E1270", {"start": v(43.22, -11.6) * mm, "end": v(42.77, -11.74) * mm});
            skLineSegment(sketch, "E1271", {"start": v(42.77, -11.74) * mm, "end": v(41.9, -11.83) * mm});
            skLineSegment(sketch, "E1272", {"start": v(41.9, -11.83) * mm, "end": v(41.7, -11.85) * mm});
            skLineSegment(sketch, "E1273", {"start": v(41.7, -11.85) * mm, "end": v(41.16, -11.88) * mm});
            skLineSegment(sketch, "E1274", {"start": v(41.16, -11.88) * mm, "end": v(41.1, -11.88) * mm});
            skLineSegment(sketch, "E1275", {"start": v(41.1, -11.88) * mm, "end": v(40.7, -11.89) * mm});
            skLineSegment(sketch, "E1276", {"start": v(40.7, -11.89) * mm, "end": v(40.63, -11.88) * mm});
            skLineSegment(sketch, "E1277", {"start": v(40.63, -11.88) * mm, "end": v(40.4, -11.88) * mm});
            skLineSegment(sketch, "E1278", {"start": v(40.4, -11.88) * mm, "end": v(40.33, -11.88) * mm});
            skLineSegment(sketch, "E1279", {"start": v(40.33, -11.88) * mm, "end": v(40.2, -11.86) * mm});
            skLineSegment(sketch, "E1280", {"start": v(40.2, -11.86) * mm, "end": v(39.56, -11.86) * mm});
            skLineSegment(sketch, "E1281", {"start": v(39.56, -11.86) * mm, "end": v(39.46, -11.87) * mm});
            skLineSegment(sketch, "E1282", {"start": v(39.46, -11.87) * mm, "end": v(39.4, -11.89) * mm});
            skLineSegment(sketch, "E1283", {"start": v(39.4, -11.89) * mm, "end": v(39.36, -11.92) * mm});
            skLineSegment(sketch, "E1284", {"start": v(39.36, -11.92) * mm, "end": v(38.84, -13.5) * mm});
            skLineSegment(sketch, "E1285", {"start": v(38.84, -13.5) * mm, "end": v(38.87, -13.55) * mm});
            skLineSegment(sketch, "E1286", {"start": v(38.87, -13.55) * mm, "end": v(38.9, -13.6) * mm});
            skLineSegment(sketch, "E1287", {"start": v(38.9, -13.6) * mm, "end": v(38.97, -13.66) * mm});
            skLineSegment(sketch, "E1288", {"start": v(38.97, -13.66) * mm, "end": v(39.5, -14.04) * mm});
            skLineSegment(sketch, "E1289", {"start": v(39.5, -14.04) * mm, "end": v(39.6, -14.1) * mm});
            skLineSegment(sketch, "E1290", {"start": v(39.6, -14.1) * mm, "end": v(39.67, -14.13) * mm});
            skLineSegment(sketch, "E1291", {"start": v(39.67, -14.13) * mm, "end": v(39.85, -14.27) * mm});
            skLineSegment(sketch, "E1292", {"start": v(39.85, -14.27) * mm, "end": v(39.91, -14.3) * mm});
            skLineSegment(sketch, "E1293", {"start": v(39.91, -14.3) * mm, "end": v(40.24, -14.55) * mm});
            skLineSegment(sketch, "E1294", {"start": v(40.24, -14.55) * mm, "end": v(40.28, -14.58) * mm});
            skLineSegment(sketch, "E1295", {"start": v(40.28, -14.58) * mm, "end": v(40.7, -14.93) * mm});
            skLineSegment(sketch, "E1296", {"start": v(40.7, -14.93) * mm, "end": v(40.85, -15.05) * mm});
            skLineSegment(sketch, "E1297", {"start": v(40.85, -15.05) * mm, "end": v(41.5, -15.65) * mm});
            skLineSegment(sketch, "E1298", {"start": v(41.5, -15.65) * mm, "end": v(41.79, -16.01) * mm});
            skLineSegment(sketch, "E1299", {"start": v(41.79, -16.01) * mm, "end": v(41.78, -16.27) * mm});
            skLineSegment(sketch, "E1300", {"start": v(41.78, -16.27) * mm, "end": v(41.63, -16.69) * mm});
            skLineSegment(sketch, "E1301", {"start": v(41.63, -16.69) * mm, "end": v(41.58, -16.8) * mm});
            skLineSegment(sketch, "E1302", {"start": v(41.58, -16.8) * mm, "end": v(41.53, -16.91) * mm});
            skLineSegment(sketch, "E1303", {"start": v(41.53, -16.91) * mm, "end": v(41.35, -17.32) * mm});
            skLineSegment(sketch, "E1304", {"start": v(41.35, -17.32) * mm, "end": v(41.18, -17.5) * mm});
            skLineSegment(sketch, "E1305", {"start": v(41.18, -17.5) * mm, "end": v(40.72, -17.57) * mm});
            skLineSegment(sketch, "E1306", {"start": v(40.72, -17.57) * mm, "end": v(39.84, -17.55) * mm});
            skLineSegment(sketch, "E1307", {"start": v(39.84, -17.55) * mm, "end": v(39.65, -17.54) * mm});
            skLineSegment(sketch, "E1308", {"start": v(39.65, -17.54) * mm, "end": v(39.1, -17.5) * mm});
            skLineSegment(sketch, "E1309", {"start": v(39.1, -17.5) * mm, "end": v(39.05, -17.49) * mm});
            skLineSegment(sketch, "E1310", {"start": v(39.05, -17.49) * mm, "end": v(38.65, -17.44) * mm});
            skLineSegment(sketch, "E1311", {"start": v(38.65, -17.44) * mm, "end": v(38.58, -17.41) * mm});
            skLineSegment(sketch, "E1312", {"start": v(38.58, -17.41) * mm, "end": v(38.35, -17.4) * mm});
            skLineSegment(sketch, "E1313", {"start": v(38.35, -17.4) * mm, "end": v(38.28, -17.38) * mm});
            skLineSegment(sketch, "E1314", {"start": v(38.28, -17.38) * mm, "end": v(38.17, -17.34) * mm});
            skLineSegment(sketch, "E1315", {"start": v(38.17, -17.34) * mm, "end": v(37.53, -17.25) * mm});
            skLineSegment(sketch, "E1316", {"start": v(37.53, -17.25) * mm, "end": v(37.42, -17.24) * mm});
            skLineSegment(sketch, "E1317", {"start": v(37.42, -17.24) * mm, "end": v(37.37, -17.26) * mm});
            skLineSegment(sketch, "E1318", {"start": v(37.37, -17.26) * mm, "end": v(37.31, -17.28) * mm});
            skLineSegment(sketch, "E1319", {"start": v(37.31, -17.28) * mm, "end": v(36.59, -18.77) * mm});
            skLineSegment(sketch, "E1320", {"start": v(36.59, -18.77) * mm, "end": v(36.6, -18.83) * mm});
            skLineSegment(sketch, "E1321", {"start": v(36.6, -18.83) * mm, "end": v(36.63, -18.87) * mm});
            skLineSegment(sketch, "E1322", {"start": v(36.63, -18.87) * mm, "end": v(36.7, -18.95) * mm});
            skLineSegment(sketch, "E1323", {"start": v(36.7, -18.95) * mm, "end": v(37.16, -19.4) * mm});
            skLineSegment(sketch, "E1324", {"start": v(37.16, -19.4) * mm, "end": v(37.26, -19.47) * mm});
            skLineSegment(sketch, "E1325", {"start": v(37.26, -19.47) * mm, "end": v(37.32, -19.52) * mm});
            skLineSegment(sketch, "E1326", {"start": v(37.32, -19.52) * mm, "end": v(37.47, -19.68) * mm});
            skLineSegment(sketch, "E1327", {"start": v(37.47, -19.68) * mm, "end": v(37.53, -19.72) * mm});
            skLineSegment(sketch, "E1328", {"start": v(37.53, -19.72) * mm, "end": v(37.82, -20) * mm});
            skLineSegment(sketch, "E1329", {"start": v(37.82, -20) * mm, "end": v(37.86, -20.05) * mm});
            skLineSegment(sketch, "E1330", {"start": v(37.86, -20.05) * mm, "end": v(38.24, -20.45) * mm});
            skLineSegment(sketch, "E1331", {"start": v(38.24, -20.45) * mm, "end": v(38.36, -20.6) * mm});
            skLineSegment(sketch, "E1332", {"start": v(38.36, -20.6) * mm, "end": v(38.92, -21.27) * mm});
            skLineSegment(sketch, "E1333", {"start": v(38.92, -21.27) * mm, "end": v(39.15, -21.67) * mm});
            skLineSegment(sketch, "E1334", {"start": v(39.15, -21.67) * mm, "end": v(39.1, -21.92) * mm});
            skLineSegment(sketch, "E1335", {"start": v(39.1, -21.92) * mm, "end": v(38.9, -22.32) * mm});
            skLineSegment(sketch, "E1336", {"start": v(38.9, -22.32) * mm, "end": v(38.84, -22.42) * mm});
            skLineSegment(sketch, "E1337", {"start": v(38.84, -22.42) * mm, "end": v(38.78, -22.53) * mm});
            skLineSegment(sketch, "E1338", {"start": v(38.78, -22.53) * mm, "end": v(38.54, -22.9) * mm});
            skLineSegment(sketch, "E1339", {"start": v(38.54, -22.9) * mm, "end": v(38.34, -23.07) * mm});
            skLineSegment(sketch, "E1340", {"start": v(38.34, -23.07) * mm, "end": v(37.88, -23.07) * mm});
            skLineSegment(sketch, "E1341", {"start": v(37.88, -23.07) * mm, "end": v(37.01, -22.92) * mm});
            skLineSegment(sketch, "E1342", {"start": v(37.01, -22.92) * mm, "end": v(36.83, -22.89) * mm});
            skLineSegment(sketch, "E1343", {"start": v(36.83, -22.89) * mm, "end": v(36.3, -22.77) * mm});
            skLineSegment(sketch, "E1344", {"start": v(36.3, -22.77) * mm, "end": v(36.24, -22.75) * mm});
            skLineSegment(sketch, "E1345", {"start": v(36.24, -22.75) * mm, "end": v(35.85, -22.65) * mm});
            skLineSegment(sketch, "E1346", {"start": v(35.85, -22.65) * mm, "end": v(35.78, -22.61) * mm});
            skLineSegment(sketch, "E1347", {"start": v(35.78, -22.61) * mm, "end": v(35.56, -22.56) * mm});
            skLineSegment(sketch, "E1348", {"start": v(35.56, -22.56) * mm, "end": v(35.5, -22.54) * mm});
            skLineSegment(sketch, "E1349", {"start": v(35.5, -22.54) * mm, "end": v(35.38, -22.48) * mm});
            skLineSegment(sketch, "E1350", {"start": v(35.38, -22.48) * mm, "end": v(34.76, -22.3) * mm});
            skLineSegment(sketch, "E1351", {"start": v(34.76, -22.3) * mm, "end": v(34.66, -22.28) * mm});
            skLineSegment(sketch, "E1352", {"start": v(34.66, -22.28) * mm, "end": v(34.6, -22.29) * mm});
            skLineSegment(sketch, "E1353", {"start": v(34.6, -22.29) * mm, "end": v(34.55, -22.3) * mm});
            skLineSegment(sketch, "E1354", {"start": v(34.55, -22.3) * mm, "end": v(33.62, -23.68) * mm});
            skLineSegment(sketch, "E1355", {"start": v(33.62, -23.68) * mm, "end": v(33.63, -23.74) * mm});
            skLineSegment(sketch, "E1356", {"start": v(33.63, -23.74) * mm, "end": v(33.64, -23.79) * mm});
            skLineSegment(sketch, "E1357", {"start": v(33.64, -23.79) * mm, "end": v(33.7, -23.87) * mm});
            skLineSegment(sketch, "E1358", {"start": v(33.7, -23.87) * mm, "end": v(34.1, -24.39) * mm});
            skLineSegment(sketch, "E1359", {"start": v(34.1, -24.39) * mm, "end": v(34.2, -24.46) * mm});
            skLineSegment(sketch, "E1360", {"start": v(34.2, -24.46) * mm, "end": v(34.24, -24.52) * mm});
            skLineSegment(sketch, "E1361", {"start": v(34.24, -24.52) * mm, "end": v(34.37, -24.7) * mm});
            skLineSegment(sketch, "E1362", {"start": v(34.37, -24.7) * mm, "end": v(34.42, -24.75) * mm});
            skLineSegment(sketch, "E1363", {"start": v(34.42, -24.75) * mm, "end": v(34.67, -25.08) * mm});
            skLineSegment(sketch, "E1364", {"start": v(34.67, -25.08) * mm, "end": v(34.7, -25.12) * mm});
            skLineSegment(sketch, "E1365", {"start": v(34.7, -25.12) * mm, "end": v(35.02, -25.57) * mm});
            skLineSegment(sketch, "E1366", {"start": v(35.02, -25.57) * mm, "end": v(35.12, -25.73) * mm});
            skLineSegment(sketch, "E1367", {"start": v(35.12, -25.73) * mm, "end": v(35.58, -26.48) * mm});
            skLineSegment(sketch, "E1368", {"start": v(35.58, -26.48) * mm, "end": v(35.75, -26.91) * mm});
            skLineSegment(sketch, "E1369", {"start": v(35.75, -26.91) * mm, "end": v(35.68, -27.15) * mm});
            skLineSegment(sketch, "E1370", {"start": v(35.68, -27.15) * mm, "end": v(35.41, -27.51) * mm});
            skLineSegment(sketch, "E1371", {"start": v(35.41, -27.51) * mm, "end": v(35.34, -27.6) * mm});
            skLineSegment(sketch, "E1372", {"start": v(35.34, -27.6) * mm, "end": v(35.26, -27.7) * mm});
            skLineSegment(sketch, "E1373", {"start": v(35.26, -27.7) * mm, "end": v(34.98, -28.05) * mm});
            skLineSegment(sketch, "E1374", {"start": v(34.98, -28.05) * mm, "end": v(34.76, -28.18) * mm});
            skLineSegment(sketch, "E1375", {"start": v(34.76, -28.18) * mm, "end": v(34.3, -28.12) * mm});
            skLineSegment(sketch, "E1376", {"start": v(34.3, -28.12) * mm, "end": v(33.46, -27.85) * mm});
            skLineSegment(sketch, "E1377", {"start": v(33.46, -27.85) * mm, "end": v(33.28, -27.8) * mm});
            skLineSegment(sketch, "E1378", {"start": v(33.28, -27.8) * mm, "end": v(32.77, -27.6) * mm});
            skLineSegment(sketch, "E1379", {"start": v(32.77, -27.6) * mm, "end": v(32.72, -27.57) * mm});
            skLineSegment(sketch, "E1380", {"start": v(32.72, -27.57) * mm, "end": v(32.35, -27.41) * mm});
            skLineSegment(sketch, "E1381", {"start": v(32.35, -27.41) * mm, "end": v(32.28, -27.37) * mm});
            skLineSegment(sketch, "E1382", {"start": v(32.28, -27.37) * mm, "end": v(32.07, -27.29) * mm});
            skLineSegment(sketch, "E1383", {"start": v(32.07, -27.29) * mm, "end": v(32, -27.26) * mm});
            skLineSegment(sketch, "E1384", {"start": v(32, -27.26) * mm, "end": v(31.9, -27.19) * mm});
            skLineSegment(sketch, "E1385", {"start": v(31.9, -27.19) * mm, "end": v(31.32, -26.92) * mm});
            skLineSegment(sketch, "E1386", {"start": v(31.32, -26.92) * mm, "end": v(31.22, -26.9) * mm});
            skLineSegment(sketch, "E1387", {"start": v(31.22, -26.9) * mm, "end": v(31.17, -26.89) * mm});
            skLineSegment(sketch, "E1388", {"start": v(31.17, -26.89) * mm, "end": v(31.1, -26.9) * mm});
            skLineSegment(sketch, "E1389", {"start": v(31.1, -26.9) * mm, "end": v(30, -28.12) * mm});
            skLineSegment(sketch, "E1390", {"start": v(30, -28.12) * mm, "end": v(30, -28.19) * mm});
            skLineSegment(sketch, "E1391", {"start": v(30, -28.19) * mm, "end": v(30, -28.24) * mm});
            skLineSegment(sketch, "E1392", {"start": v(30, -28.24) * mm, "end": v(30.05, -28.33) * mm});
            skLineSegment(sketch, "E1393", {"start": v(30.05, -28.33) * mm, "end": v(30.37, -28.9) * mm});
            skLineSegment(sketch, "E1394", {"start": v(30.37, -28.9) * mm, "end": v(30.45, -28.98) * mm});
            skLineSegment(sketch, "E1395", {"start": v(30.45, -28.98) * mm, "end": v(30.5, -29.05) * mm});
            skLineSegment(sketch, "E1396", {"start": v(30.5, -29.05) * mm, "end": v(30.6, -29.25) * mm});
            skLineSegment(sketch, "E1397", {"start": v(30.6, -29.25) * mm, "end": v(30.64, -29.3) * mm});
            skLineSegment(sketch, "E1398", {"start": v(30.64, -29.3) * mm, "end": v(30.84, -29.66) * mm});
            skLineSegment(sketch, "E1399", {"start": v(30.84, -29.66) * mm, "end": v(30.87, -29.7) * mm});
            skLineSegment(sketch, "E1400", {"start": v(30.87, -29.7) * mm, "end": v(31.12, -30.2) * mm});
            skLineSegment(sketch, "E1401", {"start": v(31.12, -30.2) * mm, "end": v(31.2, -30.37) * mm});
            skLineSegment(sketch, "E1402", {"start": v(31.2, -30.37) * mm, "end": v(31.55, -31.17) * mm});
            skLineSegment(sketch, "E1403", {"start": v(31.55, -31.17) * mm, "end": v(31.66, -31.62) * mm});
            skLineSegment(sketch, "E1404", {"start": v(31.66, -31.62) * mm, "end": v(31.55, -31.85) * mm});
            skLineSegment(sketch, "E1405", {"start": v(31.55, -31.85) * mm, "end": v(31.24, -32.17) * mm});
            skLineSegment(sketch, "E1406", {"start": v(31.24, -32.17) * mm, "end": v(31.15, -32.26) * mm});
            skLineSegment(sketch, "E1407", {"start": v(31.15, -32.26) * mm, "end": v(31.06, -32.34) * mm});
            skLineSegment(sketch, "E1408", {"start": v(31.06, -32.34) * mm, "end": v(30.73, -32.64) * mm});
            skLineSegment(sketch, "E1409", {"start": v(30.73, -32.64) * mm, "end": v(30.5, -32.74) * mm});
            skLineSegment(sketch, "E1410", {"start": v(30.5, -32.74) * mm, "end": v(30.05, -32.62) * mm});
            skLineSegment(sketch, "E1411", {"start": v(30.05, -32.62) * mm, "end": v(29.26, -32.24) * mm});
            skLineSegment(sketch, "E1412", {"start": v(29.26, -32.24) * mm, "end": v(29.1, -32.15) * mm});
            skLineSegment(sketch, "E1413", {"start": v(29.1, -32.15) * mm, "end": v(28.61, -31.89) * mm});
            skLineSegment(sketch, "E1414", {"start": v(28.61, -31.89) * mm, "end": v(28.56, -31.86) * mm});
            skLineSegment(sketch, "E1415", {"start": v(28.56, -31.86) * mm, "end": v(28.22, -31.65) * mm});
            skLineSegment(sketch, "E1416", {"start": v(28.22, -31.65) * mm, "end": v(28.16, -31.6) * mm});
            skLineSegment(sketch, "E1417", {"start": v(28.16, -31.6) * mm, "end": v(27.96, -31.49) * mm});
            skLineSegment(sketch, "E1418", {"start": v(27.96, -31.49) * mm, "end": v(27.9, -31.45) * mm});
            skLineSegment(sketch, "E1419", {"start": v(27.9, -31.45) * mm, "end": v(27.82, -31.36) * mm});
            skLineSegment(sketch, "E1420", {"start": v(27.82, -31.36) * mm, "end": v(27.27, -31.02) * mm});
            skLineSegment(sketch, "E1421", {"start": v(27.27, -31.02) * mm, "end": v(27.17, -30.97) * mm});
            skLineSegment(sketch, "E1422", {"start": v(27.17, -30.97) * mm, "end": v(27.12, -30.97) * mm});
            skLineSegment(sketch, "E1423", {"start": v(27.12, -30.97) * mm, "end": v(27.06, -30.96) * mm});
            skLineSegment(sketch, "E1424", {"start": v(27.06, -30.96) * mm, "end": v(25.8, -32.03) * mm});
            skLineSegment(sketch, "E1425", {"start": v(25.8, -32.03) * mm, "end": v(25.78, -32.09) * mm});
            skLineSegment(sketch, "E1426", {"start": v(25.78, -32.09) * mm, "end": v(25.79, -32.14) * mm});
            skLineSegment(sketch, "E1427", {"start": v(25.79, -32.14) * mm, "end": v(25.81, -32.24) * mm});
            skLineSegment(sketch, "E1428", {"start": v(25.81, -32.24) * mm, "end": v(26.06, -32.84) * mm});
            skLineSegment(sketch, "E1429", {"start": v(26.06, -32.84) * mm, "end": v(26.12, -32.94) * mm});
            skLineSegment(sketch, "E1430", {"start": v(26.12, -32.94) * mm, "end": v(26.15, -33) * mm});
            skLineSegment(sketch, "E1431", {"start": v(26.15, -33) * mm, "end": v(26.23, -33.22) * mm});
            skLineSegment(sketch, "E1432", {"start": v(26.23, -33.22) * mm, "end": v(26.27, -33.28) * mm});
            skLineSegment(sketch, "E1433", {"start": v(26.27, -33.28) * mm, "end": v(26.41, -33.66) * mm});
            skLineSegment(sketch, "E1434", {"start": v(26.41, -33.66) * mm, "end": v(26.43, -33.71) * mm});
            skLineSegment(sketch, "E1435", {"start": v(26.43, -33.71) * mm, "end": v(26.61, -34.23) * mm});
            skLineSegment(sketch, "E1436", {"start": v(26.61, -34.23) * mm, "end": v(26.67, -34.41) * mm});
            skLineSegment(sketch, "E1437", {"start": v(26.67, -34.41) * mm, "end": v(26.9, -35.26) * mm});
            skLineSegment(sketch, "E1438", {"start": v(26.9, -35.26) * mm, "end": v(26.95, -35.72) * mm});
            skLineSegment(sketch, "E1439", {"start": v(26.95, -35.72) * mm, "end": v(26.81, -35.93) * mm});
            skLineSegment(sketch, "E1440", {"start": v(26.81, -35.93) * mm, "end": v(26.46, -36.2) * mm});
            skLineSegment(sketch, "E1441", {"start": v(26.46, -36.2) * mm, "end": v(26.36, -36.28) * mm});
            skLineSegment(sketch, "E1442", {"start": v(26.36, -36.28) * mm, "end": v(26.26, -36.35) * mm});
            skLineSegment(sketch, "E1443", {"start": v(26.26, -36.35) * mm, "end": v(25.89, -36.6) * mm});
            skLineSegment(sketch, "E1444", {"start": v(25.89, -36.6) * mm, "end": v(25.65, -36.67) * mm});
            skLineSegment(sketch, "E1445", {"start": v(25.65, -36.67) * mm, "end": v(25.22, -36.48) * mm});
            skLineSegment(sketch, "E1446", {"start": v(25.22, -36.48) * mm, "end": v(24.49, -36) * mm});
            skLineSegment(sketch, "E1447", {"start": v(24.49, -36) * mm, "end": v(24.33, -35.89) * mm});
            skLineSegment(sketch, "E1448", {"start": v(24.33, -35.89) * mm, "end": v(23.9, -35.56) * mm});
            skLineSegment(sketch, "E1449", {"start": v(23.9, -35.56) * mm, "end": v(23.85, -35.52) * mm});
            skLineSegment(sketch, "E1450", {"start": v(23.85, -35.52) * mm, "end": v(23.54, -35.27) * mm});
            skLineSegment(sketch, "E1451", {"start": v(23.54, -35.27) * mm, "end": v(23.49, -35.21) * mm});
            skLineSegment(sketch, "E1452", {"start": v(23.49, -35.21) * mm, "end": v(23.31, -35.07) * mm});
            skLineSegment(sketch, "E1453", {"start": v(23.31, -35.07) * mm, "end": v(23.26, -35.02) * mm});
            skLineSegment(sketch, "E1454", {"start": v(23.26, -35.02) * mm, "end": v(23.18, -34.93) * mm});
            skLineSegment(sketch, "E1455", {"start": v(23.18, -34.93) * mm, "end": v(22.68, -34.51) * mm});
            skLineSegment(sketch, "E1456", {"start": v(22.68, -34.51) * mm, "end": v(22.6, -34.45) * mm});
            skLineSegment(sketch, "E1457", {"start": v(22.6, -34.45) * mm, "end": v(22.55, -34.44) * mm});
            skLineSegment(sketch, "E1458", {"start": v(22.55, -34.44) * mm, "end": v(22.49, -34.43) * mm});
            skLineSegment(sketch, "E1459", {"start": v(22.49, -34.43) * mm, "end": v(21.08, -35.3) * mm});
            skLineSegment(sketch, "E1460", {"start": v(21.08, -35.3) * mm, "end": v(21.07, -35.36) * mm});
            skLineSegment(sketch, "E1461", {"start": v(21.07, -35.36) * mm, "end": v(21.06, -35.41) * mm});
            skLineSegment(sketch, "E1462", {"start": v(21.06, -35.41) * mm, "end": v(21.07, -35.52) * mm});
            skLineSegment(sketch, "E1463", {"start": v(21.07, -35.52) * mm, "end": v(21.23, -36.15) * mm});
            skLineSegment(sketch, "E1464", {"start": v(21.23, -36.15) * mm, "end": v(21.28, -36.25) * mm});
            skLineSegment(sketch, "E1465", {"start": v(21.28, -36.25) * mm, "end": v(21.3, -36.33) * mm});
            skLineSegment(sketch, "E1466", {"start": v(21.3, -36.33) * mm, "end": v(21.35, -36.55) * mm});
            skLineSegment(sketch, "E1467", {"start": v(21.35, -36.55) * mm, "end": v(21.38, -36.62) * mm});
            skLineSegment(sketch, "E1468", {"start": v(21.38, -36.62) * mm, "end": v(21.47, -37) * mm});
            skLineSegment(sketch, "E1469", {"start": v(21.47, -37) * mm, "end": v(21.48, -37.06) * mm});
            skLineSegment(sketch, "E1470", {"start": v(21.48, -37.06) * mm, "end": v(21.59, -37.6) * mm});
            skLineSegment(sketch, "E1471", {"start": v(21.59, -37.6) * mm, "end": v(21.62, -37.79) * mm});
            skLineSegment(sketch, "E1472", {"start": v(21.62, -37.79) * mm, "end": v(21.73, -38.66) * mm});
            skLineSegment(sketch, "E1473", {"start": v(21.73, -38.66) * mm, "end": v(21.72, -39.13) * mm});
            skLineSegment(sketch, "E1474", {"start": v(21.72, -39.13) * mm, "end": v(21.55, -39.31) * mm});
            skLineSegment(sketch, "E1475", {"start": v(21.55, -39.31) * mm, "end": v(21.16, -39.54) * mm});
            skLineSegment(sketch, "E1476", {"start": v(21.16, -39.54) * mm, "end": v(21.05, -39.6) * mm});
            skLineSegment(sketch, "E1477", {"start": v(21.05, -39.6) * mm, "end": v(20.95, -39.65) * mm});
            skLineSegment(sketch, "E1478", {"start": v(20.95, -39.65) * mm, "end": v(20.54, -39.85) * mm});
            skLineSegment(sketch, "E1479", {"start": v(20.54, -39.85) * mm, "end": v(20.3, -39.88) * mm});
            skLineSegment(sketch, "E1480", {"start": v(20.3, -39.88) * mm, "end": v(19.9, -39.64) * mm});
            skLineSegment(sketch, "E1481", {"start": v(19.9, -39.64) * mm, "end": v(19.24, -39.05) * mm});
            skLineSegment(sketch, "E1482", {"start": v(19.24, -39.05) * mm, "end": v(19.1, -38.93) * mm});
            skLineSegment(sketch, "E1483", {"start": v(19.1, -38.93) * mm, "end": v(18.71, -38.54) * mm});
            skLineSegment(sketch, "E1484", {"start": v(18.71, -38.54) * mm, "end": v(18.68, -38.5) * mm});
            skLineSegment(sketch, "E1485", {"start": v(18.68, -38.5) * mm, "end": v(18.4, -38.2) * mm});
            skLineSegment(sketch, "E1486", {"start": v(18.4, -38.2) * mm, "end": v(18.36, -38.14) * mm});
            skLineSegment(sketch, "E1487", {"start": v(18.36, -38.14) * mm, "end": v(18.2, -37.98) * mm});
            skLineSegment(sketch, "E1488", {"start": v(18.2, -37.98) * mm, "end": v(18.15, -37.92) * mm});
            skLineSegment(sketch, "E1489", {"start": v(18.15, -37.92) * mm, "end": v(18.1, -37.81) * mm});
            skLineSegment(sketch, "E1490", {"start": v(18.1, -37.81) * mm, "end": v(17.66, -37.33) * mm});
            skLineSegment(sketch, "E1491", {"start": v(17.66, -37.33) * mm, "end": v(17.58, -37.26) * mm});
            skLineSegment(sketch, "E1492", {"start": v(17.58, -37.26) * mm, "end": v(17.54, -37.24) * mm});
            skLineSegment(sketch, "E1493", {"start": v(17.54, -37.24) * mm, "end": v(17.48, -37.22) * mm});
            skLineSegment(sketch, "E1494", {"start": v(17.48, -37.22) * mm, "end": v(15.97, -37.9) * mm});
            skLineSegment(sketch, "E1495", {"start": v(15.97, -37.9) * mm, "end": v(15.94, -37.95) * mm});
            skLineSegment(sketch, "E1496", {"start": v(15.94, -37.95) * mm, "end": v(15.93, -38) * mm});
            skLineSegment(sketch, "E1497", {"start": v(15.93, -38) * mm, "end": v(15.93, -38.1) * mm});
            skLineSegment(sketch, "E1498", {"start": v(15.93, -38.1) * mm, "end": v(16, -38.75) * mm});
            skLineSegment(sketch, "E1499", {"start": v(16, -38.75) * mm, "end": v(16.03, -38.86) * mm});
            skLineSegment(sketch, "E1500", {"start": v(16.03, -38.86) * mm, "end": v(16.04, -38.94) * mm});
            skLineSegment(sketch, "E1501", {"start": v(16.04, -38.94) * mm, "end": v(16.06, -39.16) * mm});
            skLineSegment(sketch, "E1502", {"start": v(16.06, -39.16) * mm, "end": v(16.08, -39.23) * mm});
            skLineSegment(sketch, "E1503", {"start": v(16.08, -39.23) * mm, "end": v(16.11, -39.64) * mm});
            skLineSegment(sketch, "E1504", {"start": v(16.11, -39.64) * mm, "end": v(16.12, -39.7) * mm});
            skLineSegment(sketch, "E1505", {"start": v(16.12, -39.7) * mm, "end": v(16.15, -40.24) * mm});
            skLineSegment(sketch, "E1506", {"start": v(16.15, -40.24) * mm, "end": v(16.15, -40.43) * mm});
            skLineSegment(sketch, "E1507", {"start": v(16.15, -40.43) * mm, "end": v(16.14, -41.3) * mm});
            skLineSegment(sketch, "E1508", {"start": v(16.14, -41.3) * mm, "end": v(16.06, -41.77) * mm});
            skLineSegment(sketch, "E1509", {"start": v(16.06, -41.77) * mm, "end": v(15.87, -41.93) * mm});
            skLineSegment(sketch, "E1510", {"start": v(15.87, -41.93) * mm, "end": v(15.45, -42.1) * mm});
            skLineSegment(sketch, "E1511", {"start": v(15.45, -42.1) * mm, "end": v(15.34, -42.14) * mm});
            skLineSegment(sketch, "E1512", {"start": v(15.34, -42.14) * mm, "end": v(15.22, -42.18) * mm});
            skLineSegment(sketch, "E1513", {"start": v(15.22, -42.18) * mm, "end": v(14.8, -42.32) * mm});
            skLineSegment(sketch, "E1514", {"start": v(14.8, -42.32) * mm, "end": v(14.55, -42.32) * mm});
            skLineSegment(sketch, "E1515", {"start": v(14.55, -42.32) * mm, "end": v(14.19, -42.02) * mm});
            skLineSegment(sketch, "E1516", {"start": v(14.19, -42.02) * mm, "end": v(13.62, -41.35) * mm});
            skLineSegment(sketch, "E1517", {"start": v(13.62, -41.35) * mm, "end": v(13.5, -41.2) * mm});
            skLineSegment(sketch, "E1518", {"start": v(13.5, -41.2) * mm, "end": v(13.17, -40.77) * mm});
            skLineSegment(sketch, "E1519", {"start": v(13.17, -40.77) * mm, "end": v(13.14, -40.72) * mm});
            skLineSegment(sketch, "E1520", {"start": v(13.14, -40.72) * mm, "end": v(12.9, -40.39) * mm});
            skLineSegment(sketch, "E1521", {"start": v(12.9, -40.39) * mm, "end": v(12.87, -40.32) * mm});
            skLineSegment(sketch, "E1522", {"start": v(12.87, -40.32) * mm, "end": v(12.74, -40.14) * mm});
            skLineSegment(sketch, "E1523", {"start": v(12.74, -40.14) * mm, "end": v(12.7, -40.08) * mm});
            skLineSegment(sketch, "E1524", {"start": v(12.7, -40.08) * mm, "end": v(12.65, -39.97) * mm});
            skLineSegment(sketch, "E1525", {"start": v(12.65, -39.97) * mm, "end": v(12.3, -39.43) * mm});
            skLineSegment(sketch, "E1526", {"start": v(12.3, -39.43) * mm, "end": v(12.23, -39.35) * mm});
            skLineSegment(sketch, "E1527", {"start": v(12.23, -39.35) * mm, "end": v(12.18, -39.32) * mm});
            skLineSegment(sketch, "E1528", {"start": v(12.18, -39.32) * mm, "end": v(12.13, -39.3) * mm});
            skLineSegment(sketch, "E1529", {"start": v(12.13, -39.3) * mm, "end": v(10.54, -39.75) * mm});
            skLineSegment(sketch, "E1530", {"start": v(10.54, -39.75) * mm, "end": v(10.5, -39.8) * mm});
            skLineSegment(sketch, "E1531", {"start": v(10.5, -39.8) * mm, "end": v(10.48, -39.85) * mm});
            skLineSegment(sketch, "E1532", {"start": v(10.48, -39.85) * mm, "end": v(10.47, -39.95) * mm});
            skLineSegment(sketch, "E1533", {"start": v(10.47, -39.95) * mm, "end": v(10.45, -40.6) * mm});
            skLineSegment(sketch, "E1534", {"start": v(10.45, -40.6) * mm, "end": v(10.47, -40.72) * mm});
            skLineSegment(sketch, "E1535", {"start": v(10.47, -40.72) * mm, "end": v(10.47, -40.8) * mm});
            skLineSegment(sketch, "E1536", {"start": v(10.47, -40.8) * mm, "end": v(10.45, -41.02) * mm});
            skLineSegment(sketch, "E1537", {"start": v(10.45, -41.02) * mm, "end": v(10.46, -41.1) * mm});
            skLineSegment(sketch, "E1538", {"start": v(10.46, -41.1) * mm, "end": v(10.44, -41.5) * mm});
            skLineSegment(sketch, "E1539", {"start": v(10.44, -41.5) * mm, "end": v(10.44, -41.55) * mm});
            skLineSegment(sketch, "E1540", {"start": v(10.44, -41.55) * mm, "end": v(10.39, -42.1) * mm});
            skLineSegment(sketch, "E1541", {"start": v(10.39, -42.1) * mm, "end": v(10.36, -42.28) * mm});
            skLineSegment(sketch, "E1542", {"start": v(10.36, -42.28) * mm, "end": v(10.24, -43.15) * mm});
            skLineSegment(sketch, "E1543", {"start": v(10.24, -43.15) * mm, "end": v(10.1, -43.6) * mm});
            skLineSegment(sketch, "E1544", {"start": v(10.1, -43.6) * mm, "end": v(9.88, -43.73) * mm});
            skLineSegment(sketch, "E1545", {"start": v(9.88, -43.73) * mm, "end": v(9.44, -43.84) * mm});
            skLineSegment(sketch, "E1546", {"start": v(9.44, -43.84) * mm, "end": v(9.32, -43.86) * mm});
            skLineSegment(sketch, "E1547", {"start": v(9.32, -43.86) * mm, "end": v(9.2, -43.9) * mm});
            skLineSegment(sketch, "E1548", {"start": v(9.2, -43.9) * mm, "end": v(8.76, -43.97) * mm});
            skLineSegment(sketch, "E1549", {"start": v(8.76, -43.97) * mm, "end": v(8.51, -43.93) * mm});
            skLineSegment(sketch, "E1550", {"start": v(8.51, -43.93) * mm, "end": v(8.2, -43.59) * mm});
            skLineSegment(sketch, "E1551", {"start": v(8.2, -43.59) * mm, "end": v(7.73, -42.84) * mm});
            skLineSegment(sketch, "E1552", {"start": v(7.73, -42.84) * mm, "end": v(7.63, -42.68) * mm});
            skLineSegment(sketch, "E1553", {"start": v(7.63, -42.68) * mm, "end": v(7.37, -42.2) * mm});
            skLineSegment(sketch, "E1554", {"start": v(7.37, -42.2) * mm, "end": v(7.34, -42.15) * mm});
            skLineSegment(sketch, "E1555", {"start": v(7.34, -42.15) * mm, "end": v(7.16, -41.8) * mm});
            skLineSegment(sketch, "E1556", {"start": v(7.16, -41.8) * mm, "end": v(7.14, -41.72) * mm});
            skLineSegment(sketch, "E1557", {"start": v(7.14, -41.72) * mm, "end": v(7.03, -41.52) * mm});
            skLineSegment(sketch, "E1558", {"start": v(7.03, -41.52) * mm, "end": v(7, -41.45) * mm});
            skLineSegment(sketch, "E1559", {"start": v(7, -41.45) * mm, "end": v(6.97, -41.34) * mm});
            skLineSegment(sketch, "E1560", {"start": v(6.97, -41.34) * mm, "end": v(6.69, -40.75) * mm});
            skLineSegment(sketch, "E1561", {"start": v(6.69, -40.75) * mm, "end": v(6.63, -40.67) * mm});
            skLineSegment(sketch, "E1562", {"start": v(6.63, -40.67) * mm, "end": v(6.6, -40.63) * mm});
            skLineSegment(sketch, "E1563", {"start": v(6.6, -40.63) * mm, "end": v(6.54, -40.6) * mm});
            skLineSegment(sketch, "E1564", {"start": v(6.54, -40.6) * mm, "end": v(4.9, -40.83) * mm});
            skLineSegment(sketch, "E1565", {"start": v(4.9, -40.83) * mm, "end": v(4.86, -40.88) * mm});
            skLineSegment(sketch, "E1566", {"start": v(4.86, -40.88) * mm, "end": v(4.84, -40.92) * mm});
            skLineSegment(sketch, "E1567", {"start": v(4.84, -40.92) * mm, "end": v(4.8, -41.02) * mm});
            skLineSegment(sketch, "E1568", {"start": v(4.8, -41.02) * mm, "end": v(4.7, -41.66) * mm});
            skLineSegment(sketch, "E1569", {"start": v(4.7, -41.66) * mm, "end": v(4.7, -41.78) * mm});
            skLineSegment(sketch, "E1570", {"start": v(4.7, -41.78) * mm, "end": v(4.69, -41.85) * mm});
            skLineSegment(sketch, "E1571", {"start": v(4.69, -41.85) * mm, "end": v(4.64, -42.07) * mm});
            skLineSegment(sketch, "E1572", {"start": v(4.64, -42.07) * mm, "end": v(4.64, -42.15) * mm});
            skLineSegment(sketch, "E1573", {"start": v(4.64, -42.15) * mm, "end": v(4.56, -42.54) * mm});
            skLineSegment(sketch, "E1574", {"start": v(4.56, -42.54) * mm, "end": v(4.55, -42.6) * mm});
            skLineSegment(sketch, "E1575", {"start": v(4.55, -42.6) * mm, "end": v(4.43, -43.13) * mm});
            skLineSegment(sketch, "E1576", {"start": v(4.43, -43.13) * mm, "end": v(4.38, -43.31) * mm});
            skLineSegment(sketch, "E1577", {"start": v(4.38, -43.31) * mm, "end": v(4.13, -44.16) * mm});
            skLineSegment(sketch, "E1578", {"start": v(4.13, -44.16) * mm, "end": v(3.92, -44.58) * mm});
            skLineSegment(sketch, "E1579", {"start": v(3.92, -44.58) * mm, "end": v(3.7, -44.68) * mm});
            skLineSegment(sketch, "E1580", {"start": v(3.7, -44.68) * mm, "end": v(3.25, -44.73) * mm});
            skLineSegment(sketch, "E1581", {"start": v(3.25, -44.73) * mm, "end": v(3.13, -44.73) * mm});
            skLineSegment(sketch, "E1582", {"start": v(3.13, -44.73) * mm, "end": v(3, -44.75) * mm});
            skLineSegment(sketch, "E1583", {"start": v(3, -44.75) * mm, "end": v(2.56, -44.76) * mm});
            skLineSegment(sketch, "E1584", {"start": v(2.56, -44.76) * mm, "end": v(2.32, -44.69) * mm});
            skLineSegment(sketch, "E1585", {"start": v(2.32, -44.69) * mm, "end": v(2.06, -44.3) * mm});
            skLineSegment(sketch, "E1586", {"start": v(2.06, -44.3) * mm, "end": v(1.7, -43.5) * mm});
            skLineSegment(sketch, "E1587", {"start": v(1.7, -43.5) * mm, "end": v(1.62, -43.33) * mm});
            skLineSegment(sketch, "E1588", {"start": v(1.62, -43.33) * mm, "end": v(1.42, -42.82) * mm});
            skLineSegment(sketch, "E1589", {"start": v(1.42, -42.82) * mm, "end": v(1.4, -42.76) * mm});
            skLineSegment(sketch, "E1590", {"start": v(1.4, -42.76) * mm, "end": v(1.27, -42.38) * mm});
            skLineSegment(sketch, "E1591", {"start": v(1.27, -42.38) * mm, "end": v(1.26, -42.3) * mm});
            skLineSegment(sketch, "E1592", {"start": v(1.26, -42.3) * mm, "end": v(1.18, -42.1) * mm});
            skLineSegment(sketch, "E1593", {"start": v(1.18, -42.1) * mm, "end": v(1.16, -42.03) * mm});
            skLineSegment(sketch, "E1594", {"start": v(1.16, -42.03) * mm, "end": v(1.15, -41.9) * mm});
            skLineSegment(sketch, "E1595", {"start": v(1.15, -41.9) * mm, "end": v(0.95, -41.29) * mm});
            skLineSegment(sketch, "E1596", {"start": v(0.95, -41.29) * mm, "end": v(0.9, -41.2) * mm});
            skLineSegment(sketch, "E1597", {"start": v(0.9, -41.2) * mm, "end": v(0.87, -41.15) * mm});
            skLineSegment(sketch, "E1598", {"start": v(0.87, -41.15) * mm, "end": v(0.83, -41.11) * mm});
            skLineSegment(sketch, "E1599", {"start": v(0.83, -41.11) * mm, "end": v(-0.83, -41.11) * mm});
            skLineSegment(sketch, "E1600", {"start": v(-0.83, -41.11) * mm, "end": v(-0.87, -41.15) * mm});
            skLineSegment(sketch, "E1601", {"start": v(-0.87, -41.15) * mm, "end": v(-0.9, -41.2) * mm});
            skLineSegment(sketch, "E1602", {"start": v(-0.9, -41.2) * mm, "end": v(-0.95, -41.29) * mm});
            skLineSegment(sketch, "E1603", {"start": v(-0.95, -41.29) * mm, "end": v(-1.15, -41.9) * mm});
            skLineSegment(sketch, "E1604", {"start": v(-1.15, -41.9) * mm, "end": v(-1.16, -42.03) * mm});
            skLineSegment(sketch, "E1605", {"start": v(-1.16, -42.03) * mm, "end": v(-1.18, -42.1) * mm});
            skLineSegment(sketch, "E1606", {"start": v(-1.18, -42.1) * mm, "end": v(-1.26, -42.3) * mm});
            skLineSegment(sketch, "E1607", {"start": v(-1.26, -42.3) * mm, "end": v(-1.27, -42.38) * mm});
            skLineSegment(sketch, "E1608", {"start": v(-1.27, -42.38) * mm, "end": v(-1.4, -42.76) * mm});
            skLineSegment(sketch, "E1609", {"start": v(-1.4, -42.76) * mm, "end": v(-1.42, -42.82) * mm});
            skLineSegment(sketch, "E1610", {"start": v(-1.42, -42.82) * mm, "end": v(-1.62, -43.33) * mm});
            skLineSegment(sketch, "E1611", {"start": v(-1.62, -43.33) * mm, "end": v(-1.7, -43.5) * mm});
            skLineSegment(sketch, "E1612", {"start": v(-1.7, -43.5) * mm, "end": v(-2.06, -44.3) * mm});
            skLineSegment(sketch, "E1613", {"start": v(-2.06, -44.3) * mm, "end": v(-2.32, -44.69) * mm});
            skLineSegment(sketch, "E1614", {"start": v(-2.32, -44.69) * mm, "end": v(-2.56, -44.76) * mm});
            skLineSegment(sketch, "E1615", {"start": v(-2.56, -44.76) * mm, "end": v(-3, -44.75) * mm});
            skSolve(sketch);
        }
        {
            var Q0;
            Q0=qCreatedBy(makeId("Front.planeOp"),FACE);
            var sketch = newSketch(context, id + "F4", { "sketchPlane" : qUnion([Q0])});
            skCircle(sketch, "E1616.0", {"center": v(0, 0) * mm, "radius": 92.71 * mm});
            skCircle(sketch, "E1616.2", {"center": v(0, 60.96) * mm, "radius": 7.94 * mm});
            skCircle(sketch, "E1616.11", {"center": v(-52.8, 30.48) * mm, "radius": 7.94 * mm});
            skCircle(sketch, "E1616.12", {"center": v(-52.8, -30.48) * mm, "radius": 7.94 * mm});
            skCircle(sketch, "E1616.13", {"center": v(0, -60.96) * mm, "radius": 7.94 * mm});
            skCircle(sketch, "E1616.14", {"center": v(52.8, -30.48) * mm, "radius": 7.94 * mm});
            skCircle(sketch, "E1616.15", {"center": v(52.8, 30.48) * mm, "radius": 7.94 * mm});
            skCircle(sketch, "E1617", {"center": v(0, 0) * mm, "radius": 40.32 * mm, "construction": true});
            skLineSegment(sketch, "E1618.0", {"start": v(39.07, 35.18) * mm, "end": v(30.9, 42.53) * mm});
            skLineSegment(sketch, "E1618.1", {"start": v(30.9, 42.53) * mm, "end": v(21.38, 48.03) * mm});
            skLineSegment(sketch, "E1618.2", {"start": v(21.38, 48.03) * mm, "end": v(10.93, 51.42) * mm});
            skLineSegment(sketch, "E1618.3", {"start": v(10.93, 51.42) * mm, "end": v(0, 52.57) * mm});
            skLineSegment(sketch, "E1618.4", {"start": v(0, 52.57) * mm, "end": v(-10.93, 51.42) * mm});
            skLineSegment(sketch, "E1618.5", {"start": v(-10.93, 51.42) * mm, "end": v(-21.38, 48.03) * mm});
            skLineSegment(sketch, "E1618.6", {"start": v(-21.38, 48.03) * mm, "end": v(-30.9, 42.53) * mm});
            skLineSegment(sketch, "E1618.7", {"start": v(-30.9, 42.53) * mm, "end": v(-39.07, 35.18) * mm});
            skLineSegment(sketch, "E1618.8", {"start": v(-39.07, 35.18) * mm, "end": v(-45.53, 26.29) * mm});
            skLineSegment(sketch, "E1618.9", {"start": v(-45.53, 26.29) * mm, "end": v(-50, 16.25) * mm});
            skLineSegment(sketch, "E1618.10", {"start": v(-50, 16.25) * mm, "end": v(-52.28, 5.5) * mm});
            skLineSegment(sketch, "E1618.11", {"start": v(-52.28, 5.5) * mm, "end": v(-52.28, -5.5) * mm});
            skLineSegment(sketch, "E1618.12", {"start": v(-52.28, -5.5) * mm, "end": v(-50, -16.25) * mm});
            skLineSegment(sketch, "E1618.13", {"start": v(-50, -16.25) * mm, "end": v(-45.53, -26.29) * mm});
            skLineSegment(sketch, "E1618.14", {"start": v(-45.53, -26.29) * mm, "end": v(-39.07, -35.18) * mm});
            skLineSegment(sketch, "E1618.15", {"start": v(-39.07, -35.18) * mm, "end": v(-30.9, -42.53) * mm});
            skLineSegment(sketch, "E1618.16", {"start": v(-30.9, -42.53) * mm, "end": v(-21.38, -48.03) * mm});
            skLineSegment(sketch, "E1618.17", {"start": v(-21.38, -48.03) * mm, "end": v(-10.93, -51.42) * mm});
            skLineSegment(sketch, "E1618.18", {"start": v(-10.93, -51.42) * mm, "end": v(0, -52.57) * mm});
            skLineSegment(sketch, "E1618.19", {"start": v(0, -52.57) * mm, "end": v(10.93, -51.42) * mm});
            skLineSegment(sketch, "E1618.20", {"start": v(10.93, -51.42) * mm, "end": v(21.38, -48.03) * mm});
            skLineSegment(sketch, "E1618.21", {"start": v(21.38, -48.03) * mm, "end": v(30.9, -42.53) * mm});
            skLineSegment(sketch, "E1618.22", {"start": v(30.9, -42.53) * mm, "end": v(39.07, -35.18) * mm});
            skLineSegment(sketch, "E1618.23", {"start": v(39.07, -35.18) * mm, "end": v(45.53, -26.29) * mm});
            skLineSegment(sketch, "E1618.24", {"start": v(45.53, -26.29) * mm, "end": v(50, -16.25) * mm});
            skLineSegment(sketch, "E1618.25", {"start": v(50, -16.25) * mm, "end": v(52.28, -5.5) * mm});
            skLineSegment(sketch, "E1618.26", {"start": v(52.28, -5.5) * mm, "end": v(52.28, 5.5) * mm});
            skLineSegment(sketch, "E1618.27", {"start": v(52.28, 5.5) * mm, "end": v(50, 16.25) * mm});
            skLineSegment(sketch, "E1618.28", {"start": v(50, 16.25) * mm, "end": v(45.53, 26.29) * mm});
            skLineSegment(sketch, "E1618.29", {"start": v(45.53, 26.29) * mm, "end": v(39.07, 35.18) * mm});
            skSolve(sketch);
        }
        {
            var Q0;
            Q0 = qSketchRegion(id + "F4", true);
            extrude(context, id + "F5", {"entities" : qUnion([Q0]), "oppositeDirection" : true, "depth" : 6 * mm});
        }
        {
            var Q0;
            Q0 = qSketchRegion(id + "F3", true);
            var Q1;
            Q1=makeQuery(id+"F5.opExtrude","CAP_FACE",FACE,{"disambiguationData":[OSD([sQuery(id+"F4.wireOp",EDGE,"E1616.0"),sQuery(id+"F4.wireOp",EDGE,"E1616.2"),sQuery(id+"F4.wireOp",EDGE,"E1616.11"),sQuery(id+"F4.wireOp",EDGE,"E1616.12"),sQuery(id+"F4.wireOp",EDGE,"E1616.13"),sQuery(id+"F4.wireOp",EDGE,"E1616.14"),sQuery(id+"F4.wireOp",EDGE,"E1616.15"),sQuery(id+"F4.wireOp",EDGE,"E1618.0"),sQuery(id+"F4.wireOp",EDGE,"E1618.1"),sQuery(id+"F4.wireOp",EDGE,"E1618.2"),sQuery(id+"F4.wireOp",EDGE,"E1618.3"),sQuery(id+"F4.wireOp",EDGE,"E1618.4"),sQuery(id+"F4.wireOp",EDGE,"E1618.5"),sQuery(id+"F4.wireOp",EDGE,"E1618.6"),sQuery(id+"F4.wireOp",EDGE,"E1618.7"),sQuery(id+"F4.wireOp",EDGE,"E1618.8"),sQuery(id+"F4.wireOp",EDGE,"E1618.9"),sQuery(id+"F4.wireOp",EDGE,"E1618.10"),sQuery(id+"F4.wireOp",EDGE,"E1618.11"),sQuery(id+"F4.wireOp",EDGE,"E1618.12"),sQuery(id+"F4.wireOp",EDGE,"E1618.13"),sQuery(id+"F4.wireOp",EDGE,"E1618.14"),sQuery(id+"F4.wireOp",EDGE,"E1618.15"),sQuery(id+"F4.wireOp",EDGE,"E1618.16"),sQuery(id+"F4.wireOp",EDGE,"E1618.17"),sQuery(id+"F4.wireOp",EDGE,"E1618.18"),sQuery(id+"F4.wireOp",EDGE,"E1618.19"),sQuery(id+"F4.wireOp",EDGE,"E1618.20"),sQuery(id+"F4.wireOp",EDGE,"E1618.21"),sQuery(id+"F4.wireOp",EDGE,"E1618.22"),sQuery(id+"F4.wireOp",EDGE,"E1618.23"),sQuery(id+"F4.wireOp",EDGE,"E1618.24"),sQuery(id+"F4.wireOp",EDGE,"E1618.25"),sQuery(id+"F4.wireOp",EDGE,"E1618.26"),sQuery(id+"F4.wireOp",EDGE,"E1618.27"),sQuery(id+"F4.wireOp",EDGE,"E1618.28"),sQuery(id+"F4.wireOp",EDGE,"E1618.29")])],"isStart":false});
            extrude(context, id + "F6", {"entities" : qUnion([Q0]), "operationType" : NewBodyOperationType.ADD, "endBound" : BoundingType.UP_TO_SURFACE, "oppositeDirection" : true, "endBoundEntityFace" : qUnion([Q1]), "depth" : 6 * mm});
        }
        {
            var Q0;
            Q0=makeQuery(id+"F2.opExtrude","CAP_FACE",FACE,{"disambiguationData":[OSD([sQuery(id+"F1.wireOp",EDGE,"E7.0"),sQuery(id+"F1.wireOp",EDGE,"E8.0"),sQuery(id+"F1.wireOp",EDGE,"E9.0"),sQuery(id+"F1.wireOp",EDGE,"E10.0"),sQuery(id+"F1.wireOp",EDGE,"E10.1"),sQuery(id+"F1.wireOp",EDGE,"E10.2"),sQuery(id+"F1.wireOp",EDGE,"E10.3"),sQuery(id+"F1.wireOp",EDGE,"E10.4")])],"isStart":true});
            var sketch = newSketch(context, id + "F7", { "sketchPlane" : qUnion([Q0])});
            skLineSegment(sketch, "E1619", {"start": v(-4.05, -44.21) * mm, "end": v(-3.46, -44.43) * mm});
            skLineSegment(sketch, "E1620", {"start": v(-3.46, -44.43) * mm, "end": v(-2.84, -44.54) * mm});
            skLineSegment(sketch, "E1621", {"start": v(-2.84, -44.54) * mm, "end": v(-2.46, -44.2) * mm});
            skLineSegment(sketch, "E1622", {"start": v(-2.46, -44.2) * mm, "end": v(-1.8, -43.38) * mm});
            skLineSegment(sketch, "E1623", {"start": v(-1.8, -43.38) * mm, "end": v(-1.45, -42.74) * mm});
            skLineSegment(sketch, "E1624", {"start": v(-1.45, -42.74) * mm, "end": v(-1.32, -42.37) * mm});
            skLineSegment(sketch, "E1625", {"start": v(-1.32, -42.37) * mm, "end": v(-1.31, -42.3) * mm});
            skLineSegment(sketch, "E1626", {"start": v(-1.31, -42.3) * mm, "end": v(-1.31, -42.1) * mm});
            skLineSegment(sketch, "E1627", {"start": v(-1.31, -42.1) * mm, "end": v(-1.16, -41.36) * mm});
            skLineSegment(sketch, "E1628", {"start": v(-1.16, -41.36) * mm, "end": v(-0.86, -41.01) * mm});
            skLineSegment(sketch, "E1629", {"start": v(-0.86, -41.01) * mm, "end": v(0.86, -41.01) * mm});
            skLineSegment(sketch, "E1630", {"start": v(0.86, -41.01) * mm, "end": v(1.16, -41.36) * mm});
            skLineSegment(sketch, "E1631", {"start": v(1.16, -41.36) * mm, "end": v(1.31, -42.1) * mm});
            skLineSegment(sketch, "E1632", {"start": v(1.31, -42.1) * mm, "end": v(1.31, -42.3) * mm});
            skLineSegment(sketch, "E1633", {"start": v(1.31, -42.3) * mm, "end": v(1.32, -42.37) * mm});
            skLineSegment(sketch, "E1634", {"start": v(1.32, -42.37) * mm, "end": v(1.45, -42.74) * mm});
            skLineSegment(sketch, "E1635", {"start": v(1.45, -42.74) * mm, "end": v(1.8, -43.38) * mm});
            skLineSegment(sketch, "E1636", {"start": v(1.8, -43.38) * mm, "end": v(2.46, -44.2) * mm});
            skLineSegment(sketch, "E1637", {"start": v(2.46, -44.2) * mm, "end": v(2.84, -44.54) * mm});
            skLineSegment(sketch, "E1638", {"start": v(2.84, -44.54) * mm, "end": v(3.46, -44.43) * mm});
            skLineSegment(sketch, "E1639", {"start": v(3.46, -44.43) * mm, "end": v(4.05, -44.21) * mm});
            skLineSegment(sketch, "E1640", {"start": v(4.05, -44.21) * mm, "end": v(4.21, -43.74) * mm});
            skLineSegment(sketch, "E1641", {"start": v(4.21, -43.74) * mm, "end": v(4.38, -42.7) * mm});
            skLineSegment(sketch, "E1642", {"start": v(4.38, -42.7) * mm, "end": v(4.36, -41.96) * mm});
            skLineSegment(sketch, "E1643", {"start": v(4.36, -41.96) * mm, "end": v(4.28, -41.57) * mm});
            skLineSegment(sketch, "E1644", {"start": v(4.28, -41.57) * mm, "end": v(4.26, -41.51) * mm});
            skLineSegment(sketch, "E1645", {"start": v(4.26, -41.51) * mm, "end": v(4.16, -41.34) * mm});
            skLineSegment(sketch, "E1646", {"start": v(4.16, -41.34) * mm, "end": v(3.92, -40.63) * mm});
            skLineSegment(sketch, "E1647", {"start": v(3.92, -40.63) * mm, "end": v(4, -40.17) * mm});
            skLineSegment(sketch, "E1648", {"start": v(4, -40.17) * mm, "end": v(5.5, -39.31) * mm});
            skLineSegment(sketch, "E1649", {"start": v(5.5, -39.31) * mm, "end": v(5.93, -39.46) * mm});
            skLineSegment(sketch, "E1650", {"start": v(5.93, -39.46) * mm, "end": v(6.43, -40.02) * mm});
            skLineSegment(sketch, "E1651", {"start": v(6.43, -40.02) * mm, "end": v(6.53, -40.2) * mm});
            skLineSegment(sketch, "E1652", {"start": v(6.53, -40.2) * mm, "end": v(6.57, -40.25) * mm});
            skLineSegment(sketch, "E1653", {"start": v(6.57, -40.25) * mm, "end": v(6.87, -40.51) * mm});
            skLineSegment(sketch, "E1654", {"start": v(6.87, -40.51) * mm, "end": v(7.5, -40.9) * mm});
            skLineSegment(sketch, "E1655", {"start": v(7.5, -40.9) * mm, "end": v(8.48, -41.27) * mm});
            skLineSegment(sketch, "E1656", {"start": v(8.48, -41.27) * mm, "end": v(8.97, -41.37) * mm});
            skLineSegment(sketch, "E1657", {"start": v(8.97, -41.37) * mm, "end": v(9.45, -40.97) * mm});
            skLineSegment(sketch, "E1658", {"start": v(9.45, -40.97) * mm, "end": v(9.86, -40.49) * mm});
            skLineSegment(sketch, "E1659", {"start": v(9.86, -40.49) * mm, "end": v(9.76, -40) * mm});
            skLineSegment(sketch, "E1660", {"start": v(9.76, -40) * mm, "end": v(9.38, -39) * mm});
            skLineSegment(sketch, "E1661", {"start": v(9.38, -39) * mm, "end": v(9, -38.38) * mm});
            skLineSegment(sketch, "E1662", {"start": v(9, -38.38) * mm, "end": v(8.74, -38.08) * mm});
            skLineSegment(sketch, "E1663", {"start": v(8.74, -38.08) * mm, "end": v(8.7, -38.04) * mm});
            skLineSegment(sketch, "E1664", {"start": v(8.7, -38.04) * mm, "end": v(8.51, -37.94) * mm});
            skLineSegment(sketch, "E1665", {"start": v(8.51, -37.94) * mm, "end": v(7.95, -37.45) * mm});
            skLineSegment(sketch, "E1666", {"start": v(7.95, -37.45) * mm, "end": v(7.8, -37) * mm});
            skLineSegment(sketch, "E1667", {"start": v(7.8, -37) * mm, "end": v(8.65, -35.52) * mm});
            skLineSegment(sketch, "E1668", {"start": v(8.65, -35.52) * mm, "end": v(9.11, -35.43) * mm});
            skLineSegment(sketch, "E1669", {"start": v(9.11, -35.43) * mm, "end": v(9.83, -35.67) * mm});
            skLineSegment(sketch, "E1670", {"start": v(9.83, -35.67) * mm, "end": v(10, -35.77) * mm});
            skLineSegment(sketch, "E1671", {"start": v(10, -35.77) * mm, "end": v(10.06, -35.8) * mm});
            skLineSegment(sketch, "E1672", {"start": v(10.06, -35.8) * mm, "end": v(10.45, -35.87) * mm});
            skLineSegment(sketch, "E1673", {"start": v(10.45, -35.87) * mm, "end": v(11.18, -35.89) * mm});
            skLineSegment(sketch, "E1674", {"start": v(11.18, -35.89) * mm, "end": v(12.22, -35.72) * mm});
            skLineSegment(sketch, "E1675", {"start": v(12.22, -35.72) * mm, "end": v(12.7, -35.56) * mm});
            skLineSegment(sketch, "E1676", {"start": v(12.7, -35.56) * mm, "end": v(12.91, -34.97) * mm});
            skLineSegment(sketch, "E1677", {"start": v(12.91, -34.97) * mm, "end": v(13.02, -34.36) * mm});
            skLineSegment(sketch, "E1678", {"start": v(13.02, -34.36) * mm, "end": v(12.7, -33.98) * mm});
            skLineSegment(sketch, "E1679", {"start": v(12.7, -33.98) * mm, "end": v(11.87, -33.31) * mm});
            skLineSegment(sketch, "E1680", {"start": v(11.87, -33.31) * mm, "end": v(11.23, -32.96) * mm});
            skLineSegment(sketch, "E1681", {"start": v(11.23, -32.96) * mm, "end": v(10.86, -32.83) * mm});
            skLineSegment(sketch, "E1682", {"start": v(10.86, -32.83) * mm, "end": v(10.8, -32.82) * mm});
            skLineSegment(sketch, "E1683", {"start": v(10.8, -32.82) * mm, "end": v(10.59, -32.83) * mm});
            skLineSegment(sketch, "E1684", {"start": v(10.59, -32.83) * mm, "end": v(9.85, -32.68) * mm});
            skLineSegment(sketch, "E1685", {"start": v(9.85, -32.68) * mm, "end": v(9.5, -32.37) * mm});
            skLineSegment(sketch, "E1686", {"start": v(9.5, -32.37) * mm, "end": v(9.5, -30.66) * mm});
            skLineSegment(sketch, "E1687", {"start": v(9.5, -30.66) * mm, "end": v(9.85, -30.35) * mm});
            skLineSegment(sketch, "E1688", {"start": v(9.85, -30.35) * mm, "end": v(10.59, -30.2) * mm});
            skLineSegment(sketch, "E1689", {"start": v(10.59, -30.2) * mm, "end": v(10.8, -30.2) * mm});
            skLineSegment(sketch, "E1690", {"start": v(10.8, -30.2) * mm, "end": v(10.86, -30.2) * mm});
            skLineSegment(sketch, "E1691", {"start": v(10.86, -30.2) * mm, "end": v(11.23, -30.06) * mm});
            skLineSegment(sketch, "E1692", {"start": v(11.23, -30.06) * mm, "end": v(11.87, -29.71) * mm});
            skLineSegment(sketch, "E1693", {"start": v(11.87, -29.71) * mm, "end": v(12.7, -29.05) * mm});
            skLineSegment(sketch, "E1694", {"start": v(12.7, -29.05) * mm, "end": v(13.02, -28.67) * mm});
            skLineSegment(sketch, "E1695", {"start": v(13.02, -28.67) * mm, "end": v(12.91, -28.05) * mm});
            skLineSegment(sketch, "E1696", {"start": v(12.91, -28.05) * mm, "end": v(12.7, -27.46) * mm});
            skLineSegment(sketch, "E1697", {"start": v(12.7, -27.46) * mm, "end": v(12.22, -27.3) * mm});
            skLineSegment(sketch, "E1698", {"start": v(12.22, -27.3) * mm, "end": v(11.18, -27.14) * mm});
            skLineSegment(sketch, "E1699", {"start": v(11.18, -27.14) * mm, "end": v(10.45, -27.15) * mm});
            skLineSegment(sketch, "E1700", {"start": v(10.45, -27.15) * mm, "end": v(10.06, -27.23) * mm});
            skLineSegment(sketch, "E1701", {"start": v(10.06, -27.23) * mm, "end": v(10, -27.25) * mm});
            skLineSegment(sketch, "E1702", {"start": v(10, -27.25) * mm, "end": v(9.83, -27.36) * mm});
            skLineSegment(sketch, "E1703", {"start": v(9.83, -27.36) * mm, "end": v(9.11, -27.6) * mm});
            skLineSegment(sketch, "E1704", {"start": v(9.11, -27.6) * mm, "end": v(8.65, -27.5) * mm});
            skLineSegment(sketch, "E1705", {"start": v(8.65, -27.5) * mm, "end": v(7.8, -26.02) * mm});
            skLineSegment(sketch, "E1706", {"start": v(7.8, -26.02) * mm, "end": v(7.95, -25.58) * mm});
            skLineSegment(sketch, "E1707", {"start": v(7.95, -25.58) * mm, "end": v(8.51, -25.08) * mm});
            skLineSegment(sketch, "E1708", {"start": v(8.51, -25.08) * mm, "end": v(8.7, -24.98) * mm});
            skLineSegment(sketch, "E1709", {"start": v(8.7, -24.98) * mm, "end": v(8.74, -24.94) * mm});
            skLineSegment(sketch, "E1710", {"start": v(8.74, -24.94) * mm, "end": v(9, -24.64) * mm});
            skLineSegment(sketch, "E1711", {"start": v(9, -24.64) * mm, "end": v(9.38, -24.02) * mm});
            skLineSegment(sketch, "E1712", {"start": v(9.38, -24.02) * mm, "end": v(9.76, -23.03) * mm});
            skLineSegment(sketch, "E1713", {"start": v(9.76, -23.03) * mm, "end": v(9.86, -22.54) * mm});
            skLineSegment(sketch, "E1714", {"start": v(9.86, -22.54) * mm, "end": v(9.45, -22.06) * mm});
            skLineSegment(sketch, "E1715", {"start": v(9.45, -22.06) * mm, "end": v(8.97, -21.66) * mm});
            skLineSegment(sketch, "E1716", {"start": v(8.97, -21.66) * mm, "end": v(8.48, -21.75) * mm});
            skLineSegment(sketch, "E1717", {"start": v(8.48, -21.75) * mm, "end": v(7.5, -22.13) * mm});
            skLineSegment(sketch, "E1718", {"start": v(7.5, -22.13) * mm, "end": v(6.87, -22.51) * mm});
            skLineSegment(sketch, "E1719", {"start": v(6.87, -22.51) * mm, "end": v(6.57, -22.77) * mm});
            skLineSegment(sketch, "E1720", {"start": v(6.57, -22.77) * mm, "end": v(6.53, -22.82) * mm});
            skLineSegment(sketch, "E1721", {"start": v(6.53, -22.82) * mm, "end": v(6.43, -23) * mm});
            skLineSegment(sketch, "E1722", {"start": v(6.43, -23) * mm, "end": v(5.93, -23.56) * mm});
            skLineSegment(sketch, "E1723", {"start": v(5.93, -23.56) * mm, "end": v(5.5, -23.71) * mm});
            skLineSegment(sketch, "E1724", {"start": v(5.5, -23.71) * mm, "end": v(4, -22.86) * mm});
            skLineSegment(sketch, "E1725", {"start": v(4, -22.86) * mm, "end": v(3.92, -22.4) * mm});
            skLineSegment(sketch, "E1726", {"start": v(3.92, -22.4) * mm, "end": v(4.16, -21.69) * mm});
            skLineSegment(sketch, "E1727", {"start": v(4.16, -21.69) * mm, "end": v(4.26, -21.51) * mm});
            skLineSegment(sketch, "E1728", {"start": v(4.26, -21.51) * mm, "end": v(4.28, -21.45) * mm});
            skLineSegment(sketch, "E1729", {"start": v(4.28, -21.45) * mm, "end": v(4.36, -21.06) * mm});
            skLineSegment(sketch, "E1730", {"start": v(4.36, -21.06) * mm, "end": v(4.38, -20.33) * mm});
            skLineSegment(sketch, "E1731", {"start": v(4.38, -20.33) * mm, "end": v(4.21, -19.29) * mm});
            skLineSegment(sketch, "E1732", {"start": v(4.21, -19.29) * mm, "end": v(4.05, -18.81) * mm});
            skLineSegment(sketch, "E1733", {"start": v(4.05, -18.81) * mm, "end": v(3.46, -18.6) * mm});
            skLineSegment(sketch, "E1734", {"start": v(3.46, -18.6) * mm, "end": v(2.84, -18.5) * mm});
            skLineSegment(sketch, "E1735", {"start": v(2.84, -18.5) * mm, "end": v(2.46, -18.82) * mm});
            skLineSegment(sketch, "E1736", {"start": v(2.46, -18.82) * mm, "end": v(1.8, -19.64) * mm});
            skLineSegment(sketch, "E1737", {"start": v(1.8, -19.64) * mm, "end": v(1.45, -20.28) * mm});
            skLineSegment(sketch, "E1738", {"start": v(1.45, -20.28) * mm, "end": v(1.32, -20.66) * mm});
            skLineSegment(sketch, "E1739", {"start": v(1.32, -20.66) * mm, "end": v(1.31, -20.72) * mm});
            skLineSegment(sketch, "E1740", {"start": v(1.31, -20.72) * mm, "end": v(1.31, -20.93) * mm});
            skLineSegment(sketch, "E1741", {"start": v(1.31, -20.93) * mm, "end": v(1.16, -21.66) * mm});
            skLineSegment(sketch, "E1742", {"start": v(1.16, -21.66) * mm, "end": v(0.86, -22.01) * mm});
            skLineSegment(sketch, "E1743", {"start": v(0.86, -22.01) * mm, "end": v(-0.86, -22.01) * mm});
            skLineSegment(sketch, "E1744", {"start": v(-0.86, -22.01) * mm, "end": v(-1.16, -21.66) * mm});
            skLineSegment(sketch, "E1745", {"start": v(-1.16, -21.66) * mm, "end": v(-1.31, -20.93) * mm});
            skLineSegment(sketch, "E1746", {"start": v(-1.31, -20.93) * mm, "end": v(-1.31, -20.72) * mm});
            skLineSegment(sketch, "E1747", {"start": v(-1.31, -20.72) * mm, "end": v(-1.32, -20.66) * mm});
            skLineSegment(sketch, "E1748", {"start": v(-1.32, -20.66) * mm, "end": v(-1.45, -20.28) * mm});
            skLineSegment(sketch, "E1749", {"start": v(-1.45, -20.28) * mm, "end": v(-1.8, -19.64) * mm});
            skLineSegment(sketch, "E1750", {"start": v(-1.8, -19.64) * mm, "end": v(-2.46, -18.82) * mm});
            skLineSegment(sketch, "E1751", {"start": v(-2.46, -18.82) * mm, "end": v(-2.84, -18.5) * mm});
            skLineSegment(sketch, "E1752", {"start": v(-2.84, -18.5) * mm, "end": v(-3.46, -18.6) * mm});
            skLineSegment(sketch, "E1753", {"start": v(-3.46, -18.6) * mm, "end": v(-4.05, -18.81) * mm});
            skLineSegment(sketch, "E1754", {"start": v(-4.05, -18.81) * mm, "end": v(-4.21, -19.29) * mm});
            skLineSegment(sketch, "E1755", {"start": v(-4.21, -19.29) * mm, "end": v(-4.38, -20.33) * mm});
            skLineSegment(sketch, "E1756", {"start": v(-4.38, -20.33) * mm, "end": v(-4.36, -21.06) * mm});
            skLineSegment(sketch, "E1757", {"start": v(-4.36, -21.06) * mm, "end": v(-4.28, -21.45) * mm});
            skLineSegment(sketch, "E1758", {"start": v(-4.28, -21.45) * mm, "end": v(-4.26, -21.51) * mm});
            skLineSegment(sketch, "E1759", {"start": v(-4.26, -21.51) * mm, "end": v(-4.16, -21.69) * mm});
            skLineSegment(sketch, "E1760", {"start": v(-4.16, -21.69) * mm, "end": v(-3.92, -22.4) * mm});
            skLineSegment(sketch, "E1761", {"start": v(-3.92, -22.4) * mm, "end": v(-4, -22.86) * mm});
            skLineSegment(sketch, "E1762", {"start": v(-4, -22.86) * mm, "end": v(-5.5, -23.71) * mm});
            skLineSegment(sketch, "E1763", {"start": v(-5.5, -23.71) * mm, "end": v(-5.93, -23.56) * mm});
            skLineSegment(sketch, "E1764", {"start": v(-5.93, -23.56) * mm, "end": v(-6.43, -23) * mm});
            skLineSegment(sketch, "E1765", {"start": v(-6.43, -23) * mm, "end": v(-6.53, -22.82) * mm});
            skLineSegment(sketch, "E1766", {"start": v(-6.53, -22.82) * mm, "end": v(-6.57, -22.77) * mm});
            skLineSegment(sketch, "E1767", {"start": v(-6.57, -22.77) * mm, "end": v(-6.87, -22.51) * mm});
            skLineSegment(sketch, "E1768", {"start": v(-6.87, -22.51) * mm, "end": v(-7.5, -22.13) * mm});
            skLineSegment(sketch, "E1769", {"start": v(-7.5, -22.13) * mm, "end": v(-8.48, -21.75) * mm});
            skLineSegment(sketch, "E1770", {"start": v(-8.48, -21.75) * mm, "end": v(-8.97, -21.66) * mm});
            skLineSegment(sketch, "E1771", {"start": v(-8.97, -21.66) * mm, "end": v(-9.45, -22.06) * mm});
            skLineSegment(sketch, "E1772", {"start": v(-9.45, -22.06) * mm, "end": v(-9.86, -22.54) * mm});
            skLineSegment(sketch, "E1773", {"start": v(-9.86, -22.54) * mm, "end": v(-9.76, -23.03) * mm});
            skLineSegment(sketch, "E1774", {"start": v(-9.76, -23.03) * mm, "end": v(-9.38, -24.02) * mm});
            skLineSegment(sketch, "E1775", {"start": v(-9.38, -24.02) * mm, "end": v(-9, -24.64) * mm});
            skLineSegment(sketch, "E1776", {"start": v(-9, -24.64) * mm, "end": v(-8.74, -24.94) * mm});
            skLineSegment(sketch, "E1777", {"start": v(-8.74, -24.94) * mm, "end": v(-8.7, -24.98) * mm});
            skLineSegment(sketch, "E1778", {"start": v(-8.7, -24.98) * mm, "end": v(-8.51, -25.08) * mm});
            skLineSegment(sketch, "E1779", {"start": v(-8.51, -25.08) * mm, "end": v(-7.95, -25.58) * mm});
            skLineSegment(sketch, "E1780", {"start": v(-7.95, -25.58) * mm, "end": v(-7.8, -26.02) * mm});
            skLineSegment(sketch, "E1781", {"start": v(-7.8, -26.02) * mm, "end": v(-8.65, -27.5) * mm});
            skLineSegment(sketch, "E1782", {"start": v(-8.65, -27.5) * mm, "end": v(-9.11, -27.6) * mm});
            skLineSegment(sketch, "E1783", {"start": v(-9.11, -27.6) * mm, "end": v(-9.83, -27.36) * mm});
            skLineSegment(sketch, "E1784", {"start": v(-9.83, -27.36) * mm, "end": v(-10, -27.25) * mm});
            skLineSegment(sketch, "E1785", {"start": v(-10, -27.25) * mm, "end": v(-10.06, -27.23) * mm});
            skLineSegment(sketch, "E1786", {"start": v(-10.06, -27.23) * mm, "end": v(-10.45, -27.15) * mm});
            skLineSegment(sketch, "E1787", {"start": v(-10.45, -27.15) * mm, "end": v(-11.18, -27.14) * mm});
            skLineSegment(sketch, "E1788", {"start": v(-11.18, -27.14) * mm, "end": v(-12.22, -27.3) * mm});
            skLineSegment(sketch, "E1789", {"start": v(-12.22, -27.3) * mm, "end": v(-12.7, -27.46) * mm});
            skLineSegment(sketch, "E1790", {"start": v(-12.7, -27.46) * mm, "end": v(-12.91, -28.05) * mm});
            skLineSegment(sketch, "E1791", {"start": v(-12.91, -28.05) * mm, "end": v(-13.02, -28.67) * mm});
            skLineSegment(sketch, "E1792", {"start": v(-13.02, -28.67) * mm, "end": v(-12.7, -29.05) * mm});
            skLineSegment(sketch, "E1793", {"start": v(-12.7, -29.05) * mm, "end": v(-11.87, -29.71) * mm});
            skLineSegment(sketch, "E1794", {"start": v(-11.87, -29.71) * mm, "end": v(-11.23, -30.06) * mm});
            skLineSegment(sketch, "E1795", {"start": v(-11.23, -30.06) * mm, "end": v(-10.86, -30.2) * mm});
            skLineSegment(sketch, "E1796", {"start": v(-10.86, -30.2) * mm, "end": v(-10.8, -30.2) * mm});
            skLineSegment(sketch, "E1797", {"start": v(-10.8, -30.2) * mm, "end": v(-10.59, -30.2) * mm});
            skLineSegment(sketch, "E1798", {"start": v(-10.59, -30.2) * mm, "end": v(-9.85, -30.35) * mm});
            skLineSegment(sketch, "E1799", {"start": v(-9.85, -30.35) * mm, "end": v(-9.5, -30.66) * mm});
            skLineSegment(sketch, "E1800", {"start": v(-9.5, -30.66) * mm, "end": v(-9.5, -32.37) * mm});
            skLineSegment(sketch, "E1801", {"start": v(-9.5, -32.37) * mm, "end": v(-9.85, -32.68) * mm});
            skLineSegment(sketch, "E1802", {"start": v(-9.85, -32.68) * mm, "end": v(-10.59, -32.83) * mm});
            skLineSegment(sketch, "E1803", {"start": v(-10.59, -32.83) * mm, "end": v(-10.8, -32.82) * mm});
            skLineSegment(sketch, "E1804", {"start": v(-10.8, -32.82) * mm, "end": v(-10.86, -32.83) * mm});
            skLineSegment(sketch, "E1805", {"start": v(-10.86, -32.83) * mm, "end": v(-11.23, -32.96) * mm});
            skLineSegment(sketch, "E1806", {"start": v(-11.23, -32.96) * mm, "end": v(-11.87, -33.31) * mm});
            skLineSegment(sketch, "E1807", {"start": v(-11.87, -33.31) * mm, "end": v(-12.7, -33.98) * mm});
            skLineSegment(sketch, "E1808", {"start": v(-12.7, -33.98) * mm, "end": v(-13.02, -34.36) * mm});
            skLineSegment(sketch, "E1809", {"start": v(-13.02, -34.36) * mm, "end": v(-12.91, -34.97) * mm});
            skLineSegment(sketch, "E1810", {"start": v(-12.91, -34.97) * mm, "end": v(-12.7, -35.56) * mm});
            skLineSegment(sketch, "E1811", {"start": v(-12.7, -35.56) * mm, "end": v(-12.22, -35.72) * mm});
            skLineSegment(sketch, "E1812", {"start": v(-12.22, -35.72) * mm, "end": v(-11.18, -35.89) * mm});
            skLineSegment(sketch, "E1813", {"start": v(-11.18, -35.89) * mm, "end": v(-10.45, -35.87) * mm});
            skLineSegment(sketch, "E1814", {"start": v(-10.45, -35.87) * mm, "end": v(-10.06, -35.8) * mm});
            skLineSegment(sketch, "E1815", {"start": v(-10.06, -35.8) * mm, "end": v(-10, -35.77) * mm});
            skLineSegment(sketch, "E1816", {"start": v(-10, -35.77) * mm, "end": v(-9.83, -35.67) * mm});
            skLineSegment(sketch, "E1817", {"start": v(-9.83, -35.67) * mm, "end": v(-9.11, -35.43) * mm});
            skLineSegment(sketch, "E1818", {"start": v(-9.11, -35.43) * mm, "end": v(-8.65, -35.52) * mm});
            skLineSegment(sketch, "E1819", {"start": v(-8.65, -35.52) * mm, "end": v(-7.8, -37) * mm});
            skLineSegment(sketch, "E1820", {"start": v(-7.8, -37) * mm, "end": v(-7.95, -37.45) * mm});
            skLineSegment(sketch, "E1821", {"start": v(-7.95, -37.45) * mm, "end": v(-8.51, -37.94) * mm});
            skLineSegment(sketch, "E1822", {"start": v(-8.51, -37.94) * mm, "end": v(-8.7, -38.04) * mm});
            skLineSegment(sketch, "E1823", {"start": v(-8.7, -38.04) * mm, "end": v(-8.74, -38.08) * mm});
            skLineSegment(sketch, "E1824", {"start": v(-8.74, -38.08) * mm, "end": v(-9, -38.38) * mm});
            skLineSegment(sketch, "E1825", {"start": v(-9, -38.38) * mm, "end": v(-9.38, -39) * mm});
            skLineSegment(sketch, "E1826", {"start": v(-9.38, -39) * mm, "end": v(-9.76, -40) * mm});
            skLineSegment(sketch, "E1827", {"start": v(-9.76, -40) * mm, "end": v(-9.86, -40.49) * mm});
            skLineSegment(sketch, "E1828", {"start": v(-9.86, -40.49) * mm, "end": v(-9.45, -40.97) * mm});
            skLineSegment(sketch, "E1829", {"start": v(-9.45, -40.97) * mm, "end": v(-8.97, -41.37) * mm});
            skLineSegment(sketch, "E1830", {"start": v(-8.97, -41.37) * mm, "end": v(-8.48, -41.27) * mm});
            skLineSegment(sketch, "E1831", {"start": v(-8.48, -41.27) * mm, "end": v(-7.5, -40.9) * mm});
            skLineSegment(sketch, "E1832", {"start": v(-7.5, -40.9) * mm, "end": v(-6.87, -40.51) * mm});
            skLineSegment(sketch, "E1833", {"start": v(-6.87, -40.51) * mm, "end": v(-6.57, -40.25) * mm});
            skLineSegment(sketch, "E1834", {"start": v(-6.57, -40.25) * mm, "end": v(-6.53, -40.2) * mm});
            skLineSegment(sketch, "E1835", {"start": v(-6.53, -40.2) * mm, "end": v(-6.43, -40.02) * mm});
            skLineSegment(sketch, "E1836", {"start": v(-6.43, -40.02) * mm, "end": v(-5.93, -39.46) * mm});
            skLineSegment(sketch, "E1837", {"start": v(-5.93, -39.46) * mm, "end": v(-5.5, -39.31) * mm});
            skLineSegment(sketch, "E1838", {"start": v(-5.5, -39.31) * mm, "end": v(-4, -40.17) * mm});
            skLineSegment(sketch, "E1839", {"start": v(-4, -40.17) * mm, "end": v(-3.92, -40.63) * mm});
            skLineSegment(sketch, "E1840", {"start": v(-3.92, -40.63) * mm, "end": v(-4.16, -41.34) * mm});
            skLineSegment(sketch, "E1841", {"start": v(-4.16, -41.34) * mm, "end": v(-4.26, -41.51) * mm});
            skLineSegment(sketch, "E1842", {"start": v(-4.26, -41.51) * mm, "end": v(-4.28, -41.57) * mm});
            skLineSegment(sketch, "E1843", {"start": v(-4.28, -41.57) * mm, "end": v(-4.36, -41.96) * mm});
            skLineSegment(sketch, "E1844", {"start": v(-4.36, -41.96) * mm, "end": v(-4.38, -42.7) * mm});
            skLineSegment(sketch, "E1845", {"start": v(-4.38, -42.7) * mm, "end": v(-4.21, -43.74) * mm});
            skLineSegment(sketch, "E1846", {"start": v(-4.21, -43.74) * mm, "end": v(-4.05, -44.21) * mm});
            skLineSegment(sketch, "E1847", {"start": v(-1.78, -32.42) * mm, "end": v(-1.93, -32.03) * mm});
            skLineSegment(sketch, "E1848", {"start": v(-1.93, -32.03) * mm, "end": v(-2, -31.62) * mm});
            skLineSegment(sketch, "E1849", {"start": v(-2, -31.62) * mm, "end": v(-1.98, -31.2) * mm});
            skLineSegment(sketch, "E1850", {"start": v(-1.98, -31.2) * mm, "end": v(-1.87, -30.8) * mm});
            skLineSegment(sketch, "E1851", {"start": v(-1.87, -30.8) * mm, "end": v(-1.68, -30.42) * mm});
            skLineSegment(sketch, "E1852", {"start": v(-1.68, -30.42) * mm, "end": v(-1.41, -30.1) * mm});
            skLineSegment(sketch, "E1853", {"start": v(-1.41, -30.1) * mm, "end": v(-1.09, -29.84) * mm});
            skLineSegment(sketch, "E1854", {"start": v(-1.09, -29.84) * mm, "end": v(-0.72, -29.65) * mm});
            skLineSegment(sketch, "E1855", {"start": v(-0.72, -29.65) * mm, "end": v(-0.31, -29.54) * mm});
            skLineSegment(sketch, "E1856", {"start": v(-0.31, -29.54) * mm, "end": v(0.1, -29.52) * mm});
            skLineSegment(sketch, "E1857", {"start": v(0.1, -29.52) * mm, "end": v(0.52, -29.58) * mm});
            skLineSegment(sketch, "E1858", {"start": v(0.52, -29.58) * mm, "end": v(0.9, -29.73) * mm});
            skLineSegment(sketch, "E1859", {"start": v(0.9, -29.73) * mm, "end": v(1.26, -29.96) * mm});
            skLineSegment(sketch, "E1860", {"start": v(1.26, -29.96) * mm, "end": v(1.55, -30.25) * mm});
            skLineSegment(sketch, "E1861", {"start": v(1.55, -30.25) * mm, "end": v(1.78, -30.6) * mm});
            skLineSegment(sketch, "E1862", {"start": v(1.78, -30.6) * mm, "end": v(1.93, -31) * mm});
            skLineSegment(sketch, "E1863", {"start": v(1.93, -31) * mm, "end": v(2, -31.4) * mm});
            skLineSegment(sketch, "E1864", {"start": v(2, -31.4) * mm, "end": v(1.98, -31.83) * mm});
            skLineSegment(sketch, "E1865", {"start": v(1.98, -31.83) * mm, "end": v(1.87, -32.23) * mm});
            skLineSegment(sketch, "E1866", {"start": v(1.87, -32.23) * mm, "end": v(1.68, -32.6) * mm});
            skLineSegment(sketch, "E1867", {"start": v(1.68, -32.6) * mm, "end": v(1.41, -32.93) * mm});
            skLineSegment(sketch, "E1868", {"start": v(1.41, -32.93) * mm, "end": v(1.09, -33.2) * mm});
            skLineSegment(sketch, "E1869", {"start": v(1.09, -33.2) * mm, "end": v(0.72, -33.38) * mm});
            skLineSegment(sketch, "E1870", {"start": v(0.72, -33.38) * mm, "end": v(0.31, -33.49) * mm});
            skLineSegment(sketch, "E1871", {"start": v(0.31, -33.49) * mm, "end": v(-0.1, -33.5) * mm});
            skLineSegment(sketch, "E1872", {"start": v(-0.1, -33.5) * mm, "end": v(-0.52, -33.44) * mm});
            skLineSegment(sketch, "E1873", {"start": v(-0.52, -33.44) * mm, "end": v(-0.9, -33.3) * mm});
            skLineSegment(sketch, "E1874", {"start": v(-0.9, -33.3) * mm, "end": v(-1.26, -33.07) * mm});
            skLineSegment(sketch, "E1875", {"start": v(-1.26, -33.07) * mm, "end": v(-1.55, -32.77) * mm});
            skLineSegment(sketch, "E1876", {"start": v(-1.55, -32.77) * mm, "end": v(-1.78, -32.42) * mm});
            skSolve(sketch);
        }
        {
            var Q0;
            Q0 = qSketchRegion(id + "F7", true);
            extrude(context, id + "F8", {"entities" : qUnion([Q0]), "depth" : 6 * mm});
        }
        {
            var Q0;
            Q0=qCreatedBy(makeId("Front.planeOp"),FACE);
            var sketch = newSketch(context, id + "F9", { "sketchPlane" : qUnion([Q0])});
            skCircle(sketch, "E1877.2", {"center": v(0, 60.96) * mm, "radius": 7.94 * mm});
            skPoint(sketch, "E1877.9", {"position": v(0, 0) * mm});
            skCircle(sketch, "E1877.11", {"center": v(-52.8, 30.48) * mm, "radius": 7.94 * mm});
            skCircle(sketch, "E1877.12", {"center": v(-52.8, -30.48) * mm, "radius": 7.94 * mm});
            skCircle(sketch, "E1877.13", {"center": v(0, -60.96) * mm, "radius": 7.94 * mm});
            skCircle(sketch, "E1877.14", {"center": v(52.8, -30.48) * mm, "radius": 7.94 * mm});
            skCircle(sketch, "E1877.15", {"center": v(52.8, 30.48) * mm, "radius": 7.94 * mm});
            skPoint(sketch, "E1877.16", {"position": v(0, 0) * mm});
            skCircle(sketch, "E1878", {"center": v(0, 60.96) * mm, "radius": 4.94 * mm});
            skCircle(sketch, "E1879.1.0", {"center": v(-52.8, 30.48) * mm, "radius": 4.94 * mm});
            skCircle(sketch, "E1879.2.0", {"center": v(-52.8, -30.48) * mm, "radius": 4.94 * mm});
            skCircle(sketch, "E1879.3.0", {"center": v(0, -60.96) * mm, "radius": 4.94 * mm});
            skCircle(sketch, "E1879.4.0", {"center": v(52.8, -30.48) * mm, "radius": 4.94 * mm});
            skCircle(sketch, "E1879.5.0", {"center": v(52.8, 30.48) * mm, "radius": 4.94 * mm});
            skSolve(sketch);
        }
        {
            var Q0;
            Q0 = qSketchRegion(id + "F9", true);
            var Q1;
            {var subQ0=sQuery(id+"F4.wireOp",EDGE,"E1617");var subQ1=sQuery(id+"F4.wireOp",EDGE,"E1616.15");var subQ2=sQuery(id+"F4.wireOp",EDGE,"E1616.14");var subQ3=sQuery(id+"F4.wireOp",EDGE,"E1616.13");var subQ4=sQuery(id+"F4.wireOp",EDGE,"E1616.12");var subQ5=sQuery(id+"F4.wireOp",EDGE,"E1616.11");var subQ6=sQuery(id+"F4.wireOp",EDGE,"E1616.2");var subQ7=sQuery(id+"F4.wireOp",EDGE,"E1616.0");Q1=makeQuery(id+"F6.boolean.opBoolean","MERGE",FACE,{"derivedFrom":[makeQuery(id+"F5.opExtrude","CAP_FACE",FACE,{"disambiguationData":[OSD([subQ7,subQ6,subQ5,subQ4,subQ3,subQ2,subQ1,subQ0])],"isStart":false}),makeQuery(id+"F6.opExtrude","CAP_FACE",FACE,{"disambiguationData":[OSD([subQ7,subQ6,subQ5,subQ4,subQ3,subQ2,subQ1,subQ0])],"isStart":false})]});}
            extrude(context, id + "F10", {"entities" : qUnion([Q0]), "depth" : 76.2 * mm, "hasSecondDirection" : true, "secondDirectionBound" : SecondDirectionBoundingType.UP_TO_SURFACE, "secondDirectionOppositeDirection" : true, "secondDirectionBoundEntityFace" : qUnion([Q1]), "secondDirectionDepth" : 25.4 * mm});
        }
        {
            var Q0;
            Q0=makeQuery(id+"F2.opExtrude","CAP_FACE",FACE,{"disambiguationData":[OSD([sQuery(id+"F1.wireOp",EDGE,"E7.0"),sQuery(id+"F1.wireOp",EDGE,"E8.0"),sQuery(id+"F1.wireOp",EDGE,"E9.0"),sQuery(id+"F1.wireOp",EDGE,"E10.0"),sQuery(id+"F1.wireOp",EDGE,"E10.1"),sQuery(id+"F1.wireOp",EDGE,"E10.2"),sQuery(id+"F1.wireOp",EDGE,"E10.3"),sQuery(id+"F1.wireOp",EDGE,"E10.4")])],"isStart":false});
            var sketch = newSketch(context, id + "F11", { "sketchPlane" : qUnion([Q0])});
            skCircle(sketch, "E1880", {"center": v(0, 60.96) * mm, "radius": 26 * mm});
            skCircle(sketch, "E1881", {"center": v(0, 60.96) * mm, "radius": 30.16 * mm});
            skCircle(sketch, "E1882.1.0", {"center": v(-52.8, 30.48) * mm, "radius": 30.16 * mm});
            skCircle(sketch, "E1882.1.1", {"center": v(-52.8, 30.48) * mm, "radius": 26 * mm});
            skCircle(sketch, "E1882.2.0", {"center": v(-52.8, -30.48) * mm, "radius": 30.16 * mm});
            skCircle(sketch, "E1882.2.1", {"center": v(-52.8, -30.48) * mm, "radius": 26 * mm});
            skCircle(sketch, "E1882.3.0", {"center": v(0, -60.96) * mm, "radius": 30.16 * mm});
            skCircle(sketch, "E1882.3.1", {"center": v(0, -60.96) * mm, "radius": 26 * mm});
            skCircle(sketch, "E1882.4.0", {"center": v(52.8, -30.48) * mm, "radius": 30.16 * mm});
            skCircle(sketch, "E1882.4.1", {"center": v(52.8, -30.48) * mm, "radius": 26 * mm});
            skCircle(sketch, "E1882.5.0", {"center": v(52.8, 30.48) * mm, "radius": 30.16 * mm});
            skCircle(sketch, "E1882.5.1", {"center": v(52.8, 30.48) * mm, "radius": 26 * mm});
            skPoint(sketch, "E1882.center", {"position": v(0, 0) * mm});
            skSolve(sketch);
        }
        {
            var Q0;
            Q0 = qSketchRegion(id + "F11", true);
            var Q1;
            Q1=makeQuery(id+"F10.opExtrude","CAP_FACE",FACE,{"disambiguationData":[OSD([sQuery(id+"F9.wireOp",EDGE,"E1877.2"),sQuery(id+"F9.wireOp",EDGE,"E1878")])],"isStart":false});
            extrude(context, id + "F12", {"entities" : qUnion([Q0]), "operationType" : NewBodyOperationType.ADD, "endBound" : BoundingType.UP_TO_SURFACE, "endBoundEntityFace" : qUnion([Q1]), "depth" : 25.4 * mm});
        }
        {
            var Q0;
            Q0=makeQuery(id+"F10.opExtrude","CAP_FACE",FACE,{"disambiguationData":[OSD([sQuery(id+"F9.wireOp",EDGE,"E1877.2"),sQuery(id+"F9.wireOp",EDGE,"E1878")])],"isStart":false});
            var sketch = newSketch(context, id + "F13", { "sketchPlane" : qUnion([Q0])});
            skArc(sketch, "E1883.0", {"start": v(26.21, 75.88) * mm, "mid": v(0, 91.12) * mm, "end": v(-26.21, 75.88) * mm});
            skArc(sketch, "E1883.1", {"start": v(78.82, 15.24) * mm, "mid": v(78.91, 45.56) * mm, "end": v(52.6, 60.64) * mm});
            skArc(sketch, "E1883.2", {"start": v(52.6, -60.64) * mm, "mid": v(78.91, -45.56) * mm, "end": v(78.82, -15.24) * mm});
            skArc(sketch, "E1883.3", {"start": v(-26.21, -75.88) * mm, "mid": v(0, -91.12) * mm, "end": v(26.21, -75.88) * mm});
            skArc(sketch, "E1883.4", {"start": v(-78.82, -15.24) * mm, "mid": v(-78.91, -45.56) * mm, "end": v(-52.6, -60.64) * mm});
            skArc(sketch, "E1883.5", {"start": v(-52.6, 60.64) * mm, "mid": v(-78.91, 45.56) * mm, "end": v(-78.82, 15.24) * mm});
            skArc(sketch, "E1884", {"start": v(-52.6, 60.64) * mm, "mid": v(-37.34, 64.68) * mm, "end": v(-26.21, 75.88) * mm});
            skCircle(sketch, "E1885.0", {"center": v(0, 0) * mm, "radius": 6.35 * mm});
            skArc(sketch, "E1886", {"start": v(26.21, 75.88) * mm, "mid": v(37.34, 64.68) * mm, "end": v(52.6, 60.64) * mm});
            skArc(sketch, "E1887", {"start": v(78.82, 15.24) * mm, "mid": v(74.69, 0) * mm, "end": v(78.82, -15.24) * mm});
            skArc(sketch, "E1888", {"start": v(52.6, -60.64) * mm, "mid": v(37.34, -64.68) * mm, "end": v(26.21, -75.88) * mm});
            skArc(sketch, "E1889", {"start": v(-26.21, -75.88) * mm, "mid": v(-37.34, -64.68) * mm, "end": v(-52.6, -60.64) * mm});
            skArc(sketch, "E1890", {"start": v(-78.82, -15.24) * mm, "mid": v(-74.69, 0) * mm, "end": v(-78.82, 15.24) * mm});
            skCircle(sketch, "E1891.0", {"center": v(0, 60.96) * mm, "radius": 26 * mm});
            skCircle(sketch, "E1891.1", {"center": v(52.8, 30.48) * mm, "radius": 26 * mm});
            skCircle(sketch, "E1891.2", {"center": v(52.8, -30.48) * mm, "radius": 26 * mm});
            skCircle(sketch, "E1891.3", {"center": v(0, -60.96) * mm, "radius": 26 * mm});
            skCircle(sketch, "E1891.4", {"center": v(-52.8, -30.48) * mm, "radius": 26 * mm});
            skCircle(sketch, "E1891.5", {"center": v(-52.8, 30.48) * mm, "radius": 26 * mm});
            skSolve(sketch);
        }
        {
            var Q0;
            Q0 = qSketchRegion(id + "F13", true);
            extrude(context, id + "F14", {"entities" : qUnion([Q0]), "depth" : 3 * mm});
        }
        {
            var Q0;
            {var subQ0=sQuery(id+"F4.wireOp",EDGE,"E1617");var subQ1=sQuery(id+"F4.wireOp",EDGE,"E1616.15");var subQ2=sQuery(id+"F4.wireOp",EDGE,"E1616.14");var subQ3=sQuery(id+"F4.wireOp",EDGE,"E1616.13");var subQ4=sQuery(id+"F4.wireOp",EDGE,"E1616.12");var subQ5=sQuery(id+"F4.wireOp",EDGE,"E1616.11");var subQ6=sQuery(id+"F4.wireOp",EDGE,"E1616.2");var subQ7=sQuery(id+"F4.wireOp",EDGE,"E1616.0");Q0=makeQuery(id+"F6.boolean.opBoolean","MERGE",FACE,{"derivedFrom":[makeQuery(id+"F5.opExtrude","CAP_FACE",FACE,{"disambiguationData":[OSD([subQ7,subQ6,subQ5,subQ4,subQ3,subQ2,subQ1,subQ0])],"isStart":false}),makeQuery(id+"F6.opExtrude","CAP_FACE",FACE,{"disambiguationData":[OSD([subQ7,subQ6,subQ5,subQ4,subQ3,subQ2,subQ1,subQ0])],"isStart":false})]});}
            var sketch = newSketch(context, id + "F15", { "sketchPlane" : qUnion([Q0])});
            skCircle(sketch, "E1892.0", {"center": v(0, 0) * mm, "radius": 92.71 * mm});
            skCircle(sketch, "E1892.1", {"center": v(0, 60.96) * mm, "radius": 7.94 * mm});
            skCircle(sketch, "E1892.7", {"center": v(0, 0) * mm, "radius": 40.32 * mm, "construction": true});
            skCircle(sketch, "E1893", {"center": v(0, 0) * mm, "radius": 42.86 * mm});
            skSolve(sketch);
        }
        {
            var Q0;
            Q0 = qSketchRegion(id + "F15", true);
            var Q1;
            Q1=sQuery(id+"F15.wireOp",EDGE,"E1892.7");
            extrude(context, id + "F16", {"entities" : qUnion([Q0]), "surfaceEntities" : qUnion([Q1]), "depth" : 6 * mm});
        }
        {
            var Q0;
            Q0=makeQuery(id+"F16.opExtrude","CAP_FACE",FACE,{"disambiguationData":[OSD([sQuery(id+"F15.wireOp",EDGE,"E1892.0"),sQuery(id+"F15.wireOp",EDGE,"E1892.1"),sQuery(id+"F15.wireOp",EDGE,"E1893")])],"isStart":false});
            var sketch = newSketch(context, id + "F17", { "sketchPlane" : qUnion([Q0])});
            skPoint(sketch, "E1894.middle", {"position": v(0, 0) * mm});
            skLineSegment(sketch, "E1895.bottom", {"start": v(52.86, -92.7) * mm, "end": v(-52.86, -92.7) * mm});
            skLineSegment(sketch, "E1895.top", {"start": v(52.86, 92.7) * mm, "end": v(-52.86, 92.7) * mm});
            skLineSegment(sketch, "E1895.left", {"start": v(52.86, -92.7) * mm, "end": v(52.86, 92.71) * mm});
            skLineSegment(sketch, "E1895.right", {"start": v(-52.86, -92.71) * mm, "end": v(-52.86, 92.7) * mm});
            skSolve(sketch);
        }
        {
            var Q0;
            {var subQ0=sQuery(id+"F17.wireOp",EDGE,"E1895.right");var subQ1=makeQuery(id+"F16.opExtrude","CAP_EDGE",EDGE,{"disambiguationData":[OSD([sQuery(id+"F15.wireOp",EDGE,"E1892.0")])],"isStart":false});var subQ2=makeQuery(id+"F17.imprint","INTERSECT",VERTEX,{"disambiguationData":[OD(0.0)],"derivedFrom":[subQ1,subQ0]});Q0=makeQuery(id+"F17.imprint","IMPRINT",FACE,{"disambiguationData":[TD([[makeQuery(id+"F17.imprint","IMPRINT",EDGE,{"disambiguationData":[TD([[subQ2,-1.0]])],"derivedFrom":subQ0}),1.0]])]});}
            var sketch = newSketch(context, id + "F18", { "sketchPlane" : qUnion([Q0])});
            skLineSegment(sketch, "E1896.bottom", {"start": v(-52.86, 92.7) * mm, "end": v(-46.86, 92.7) * mm});
            skLineSegment(sketch, "E1896.top", {"start": v(-52.86, -92.71) * mm, "end": v(-46.86, -92.71) * mm});
            skLineSegment(sketch, "E1896.left", {"start": v(-52.86, 92.7) * mm, "end": v(-52.86, -92.71) * mm});
            skLineSegment(sketch, "E1896.right", {"start": v(-46.86, 92.7) * mm, "end": v(-46.86, -92.71) * mm});
            skLineSegment(sketch, "E1897.bottom", {"start": v(52.86, 92.7) * mm, "end": v(46.86, 92.7) * mm});
            skLineSegment(sketch, "E1897.top", {"start": v(52.86, -92.71) * mm, "end": v(46.86, -92.71) * mm});
            skLineSegment(sketch, "E1897.left", {"start": v(52.86, 92.71) * mm, "end": v(52.86, -92.71) * mm});
            skLineSegment(sketch, "E1897.right", {"start": v(46.86, 92.7) * mm, "end": v(46.86, -92.71) * mm});
            skSolve(sketch);
        }
        {
            var Q0;
            Q0 = qSketchRegion(id + "F18", true);
            extrude(context, id + "F19", {"entities" : qUnion([Q0]), "depth" : 406.4 * mm});
        }
    });
